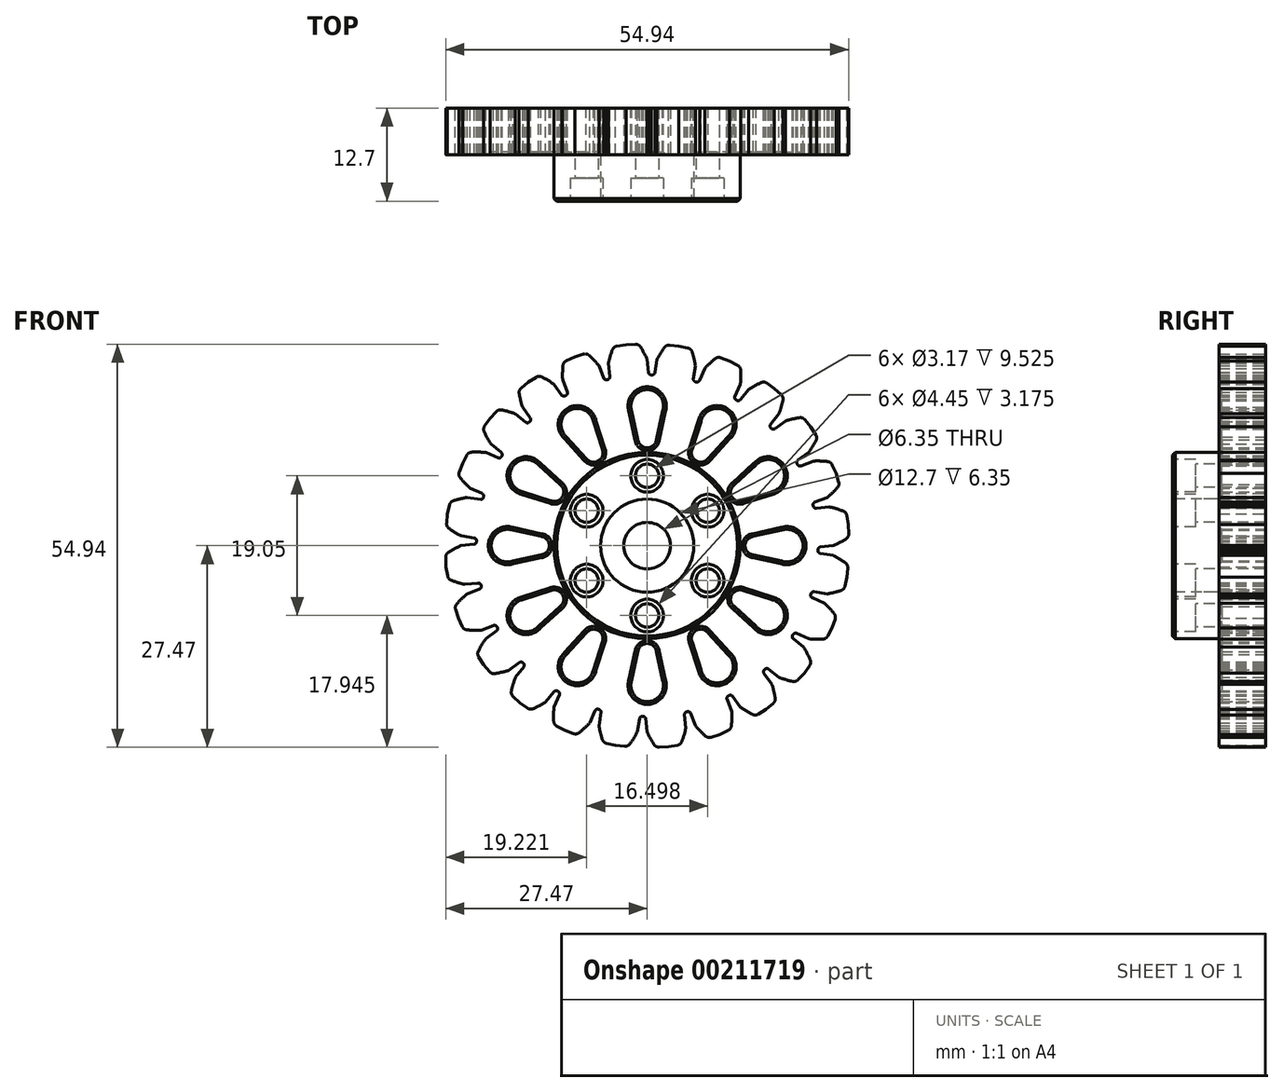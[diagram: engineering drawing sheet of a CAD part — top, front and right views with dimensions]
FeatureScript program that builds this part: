
annotation { "Feature Type Name" : "Feature", "Feature Type Description" : "" }
export const myFeature = defineFeature(function(context is Context, id is Id, definition is map)
    precondition{}
    {
        {
            var Q0;
            Q0=qCreatedBy(makeId("Front.planeOp"),FACE);
            var sketch = newSketch(context, id + "F0", { "sketchPlane" : qUnion([Q0])});
            skArc(sketch, "E0", {"start": v(-5.32, 22.67) * mm, "mid": v(-5.42, 22.64) * mm, "end": v(-5.5, 22.62) * mm});
            skArc(sketch, "E1", {"start": v(0, 25.4) * mm, "mid": v(-0.43, 26.27) * mm, "end": v(-0.93, 27.11) * mm});
            skLineSegment(sketch, "E2", {"start": v(0, 25.4) * mm, "end": v(0.2, 23.55) * mm});
            skLineSegment(sketch, "E3", {"start": v(-1.63, 27.47) * mm, "end": v(-2.88, 27.42) * mm});
            skLineSegment(sketch, "E4.MirrorCS", {"start": v(-4.11, 27.21) * mm, "end": v(-2.88, 27.42) * mm});
            skArc(sketch, "E5.MirrorCS", {"start": v(-5.28, 24.84) * mm, "mid": v(-5.04, 25.79) * mm, "end": v(-4.72, 26.71) * mm});
            skLineSegment(sketch, "E6.MirrorCS", {"start": v(-5.28, 24.84) * mm, "end": v(-5.1, 23.05) * mm});
            skPoint(sketch, "E7.orphan", {"position": v(-4.77, 20.03) * mm});
            skPoint(sketch, "E8.orphan", {"position": v(0.5, 20.58) * mm});
            skPoint(sketch, "E9.visualSharp", {"position": v(-1.19, 27.5) * mm});
            skArc(sketch, "E9.filletArc", {"start": v(-0.93, 27.11) * mm, "mid": v(-1.23, 27.38) * mm, "end": v(-1.63, 27.47) * mm});
            skPoint(sketch, "E10.visualSharp", {"position": v(-4.55, 27.14) * mm});
            skArc(sketch, "E10.filletArc", {"start": v(-4.11, 27.21) * mm, "mid": v(-4.49, 27.04) * mm, "end": v(-4.72, 26.71) * mm});
            skArc(sketch, "E11", {"start": v(-5.47, 22.63) * mm, "mid": v(-5.18, 22.78) * mm, "end": v(-5.1, 23.1) * mm});
            skArc(sketch, "E12", {"start": v(0.18, 23.7) * mm, "mid": v(0.29, 23.4) * mm, "end": v(0.6, 23.28) * mm});
            skArc(sketch, "E13.1.0", {"start": v(-11.14, 20.44) * mm, "mid": v(-10.9, 20.66) * mm, "end": v(-10.9, 20.99) * mm});
            skLineSegment(sketch, "E13.1.1", {"start": v(-11.53, 22.63) * mm, "end": v(-10.88, 20.94) * mm});
            skPoint(sketch, "E13.1.2", {"position": v(-11.42, 25.03) * mm});
            skArc(sketch, "E13.1.3", {"start": v(-11.02, 25.22) * mm, "mid": v(-11.33, 24.96) * mm, "end": v(-11.48, 24.58) * mm});
            skArc(sketch, "E13.1.4", {"start": v(-11.53, 22.63) * mm, "mid": v(-11.54, 23.6) * mm, "end": v(-11.48, 24.58) * mm});
            skLineSegment(sketch, "E13.1.5", {"start": v(-11.02, 25.22) * mm, "end": v(-9.88, 25.74) * mm});
            skLineSegment(sketch, "E13.1.6", {"start": v(-8.69, 26.11) * mm, "end": v(-9.88, 25.74) * mm});
            skArc(sketch, "E13.1.7", {"start": v(-7.92, 25.95) * mm, "mid": v(-8.28, 26.13) * mm, "end": v(-8.69, 26.11) * mm});
            skArc(sketch, "E13.1.8", {"start": v(-6.57, 24.53) * mm, "mid": v(-7.22, 25.27) * mm, "end": v(-7.92, 25.95) * mm});
            skLineSegment(sketch, "E13.1.9", {"start": v(-6.57, 24.53) * mm, "end": v(-5.9, 22.8) * mm});
            skArc(sketch, "E13.1.10", {"start": v(-5.96, 22.95) * mm, "mid": v(-5.78, 22.67) * mm, "end": v(-5.45, 22.64) * mm});
            skArc(sketch, "E13.2.0", {"start": v(-16.06, 16.86) * mm, "mid": v(-15.88, 17.13) * mm, "end": v(-15.96, 17.45) * mm});
            skLineSegment(sketch, "E13.2.1", {"start": v(-17, 18.88) * mm, "end": v(-15.93, 17.41) * mm});
            skPoint(sketch, "E13.2.2", {"position": v(-17.51, 21.23) * mm});
            skArc(sketch, "E13.2.3", {"start": v(-17.17, 21.5) * mm, "mid": v(-17.4, 21.18) * mm, "end": v(-17.45, 20.77) * mm});
            skArc(sketch, "E13.2.4", {"start": v(-17, 18.88) * mm, "mid": v(-17.26, 19.81) * mm, "end": v(-17.45, 20.77) * mm});
            skLineSegment(sketch, "E13.2.5", {"start": v(-17.17, 21.5) * mm, "end": v(-16.2, 22.3) * mm});
            skLineSegment(sketch, "E13.2.6", {"start": v(-15.15, 22.98) * mm, "end": v(-16.2, 22.3) * mm});
            skArc(sketch, "E13.2.7", {"start": v(-14.36, 23.01) * mm, "mid": v(-14.76, 23.1) * mm, "end": v(-15.15, 22.98) * mm});
            skArc(sketch, "E13.2.8", {"start": v(-12.7, 22) * mm, "mid": v(-13.51, 22.54) * mm, "end": v(-14.36, 23.01) * mm});
            skLineSegment(sketch, "E13.2.9", {"start": v(-12.7, 22) * mm, "end": v(-11.6, 20.5) * mm});
            skArc(sketch, "E13.2.10", {"start": v(-11.7, 20.62) * mm, "mid": v(-11.45, 20.4) * mm, "end": v(-11.13, 20.45) * mm});
            skArc(sketch, "E13.3.0", {"start": v(-19.87, 12.13) * mm, "mid": v(-19.77, 12.44) * mm, "end": v(-19.93, 12.72) * mm});
            skLineSegment(sketch, "E13.3.1", {"start": v(-21.3, 13.83) * mm, "end": v(-19.9, 12.7) * mm});
            skPoint(sketch, "E13.3.2", {"position": v(-22.4, 15.97) * mm});
            skArc(sketch, "E13.3.3", {"start": v(-22.15, 16.33) * mm, "mid": v(-22.3, 15.95) * mm, "end": v(-22.23, 15.55) * mm});
            skArc(sketch, "E13.3.4", {"start": v(-21.3, 13.83) * mm, "mid": v(-21.8, 14.67) * mm, "end": v(-22.23, 15.55) * mm});
            skLineSegment(sketch, "E13.3.5", {"start": v(-22.15, 16.33) * mm, "end": v(-21.42, 17.35) * mm});
            skLineSegment(sketch, "E13.3.6", {"start": v(-20.58, 18.27) * mm, "end": v(-21.42, 17.35) * mm});
            skArc(sketch, "E13.3.7", {"start": v(-19.83, 18.51) * mm, "mid": v(-20.24, 18.5) * mm, "end": v(-20.58, 18.27) * mm});
            skArc(sketch, "E13.3.8", {"start": v(-17.96, 17.96) * mm, "mid": v(-18.88, 18.27) * mm, "end": v(-19.83, 18.51) * mm});
            skLineSegment(sketch, "E13.3.9", {"start": v(-17.96, 17.96) * mm, "end": v(-16.52, 16.8) * mm});
            skArc(sketch, "E13.3.10", {"start": v(-16.64, 16.9) * mm, "mid": v(-16.34, 16.75) * mm, "end": v(-16.04, 16.88) * mm});
            skArc(sketch, "E13.4.0", {"start": v(-22.34, 6.58) * mm, "mid": v(-22.32, 6.9) * mm, "end": v(-22.55, 7.13) * mm});
            skLineSegment(sketch, "E13.4.1", {"start": v(-24.16, 7.85) * mm, "end": v(-22.5, 7.11) * mm});
            skPoint(sketch, "E13.4.2", {"position": v(-25.78, 9.63) * mm});
            skArc(sketch, "E13.4.3", {"start": v(-25.62, 10.04) * mm, "mid": v(-25.66, 9.64) * mm, "end": v(-25.5, 9.26) * mm});
            skArc(sketch, "E13.4.4", {"start": v(-24.16, 7.85) * mm, "mid": v(-24.85, 8.53) * mm, "end": v(-25.5, 9.26) * mm});
            skLineSegment(sketch, "E13.4.5", {"start": v(-25.62, 10.04) * mm, "end": v(-25.19, 11.21) * mm});
            skLineSegment(sketch, "E13.4.6", {"start": v(-24.6, 12.32) * mm, "end": v(-25.19, 11.21) * mm});
            skArc(sketch, "E13.4.7", {"start": v(-23.94, 12.75) * mm, "mid": v(-24.33, 12.62) * mm, "end": v(-24.6, 12.32) * mm});
            skArc(sketch, "E13.4.8", {"start": v(-22, 12.7) * mm, "mid": v(-22.97, 12.76) * mm, "end": v(-23.94, 12.75) * mm});
            skLineSegment(sketch, "E13.4.9", {"start": v(-22, 12.7) * mm, "end": v(-20.3, 11.94) * mm});
            skArc(sketch, "E13.4.10", {"start": v(-20.44, 12) * mm, "mid": v(-20.12, 11.95) * mm, "end": v(-19.86, 12.15) * mm});
            skArc(sketch, "E13.5.0", {"start": v(-23.28, 0.57) * mm, "mid": v(-23.34, 0.9) * mm, "end": v(-23.62, 1.05) * mm});
            skLineSegment(sketch, "E13.5.1", {"start": v(-25.37, 1.33) * mm, "end": v(-23.58, 1.05) * mm});
            skPoint(sketch, "E13.5.2", {"position": v(-27.4, 2.63) * mm});
            skArc(sketch, "E13.5.3", {"start": v(-27.35, 3.07) * mm, "mid": v(-27.28, 2.67) * mm, "end": v(-27.02, 2.35) * mm});
            skArc(sketch, "E13.5.4", {"start": v(-25.37, 1.33) * mm, "mid": v(-26.21, 1.8) * mm, "end": v(-27.02, 2.35) * mm});
            skLineSegment(sketch, "E13.5.5", {"start": v(-27.35, 3.07) * mm, "end": v(-27.23, 4.31) * mm});
            skLineSegment(sketch, "E13.5.6", {"start": v(-26.96, 5.53) * mm, "end": v(-27.23, 4.31) * mm});
            skArc(sketch, "E13.5.7", {"start": v(-26.43, 6.12) * mm, "mid": v(-26.77, 5.9) * mm, "end": v(-26.96, 5.53) * mm});
            skArc(sketch, "E13.5.8", {"start": v(-24.53, 6.57) * mm, "mid": v(-25.5, 6.38) * mm, "end": v(-26.43, 6.12) * mm});
            skLineSegment(sketch, "E13.5.9", {"start": v(-24.53, 6.57) * mm, "end": v(-22.7, 6.28) * mm});
            skArc(sketch, "E13.5.10", {"start": v(-22.86, 6.3) * mm, "mid": v(-22.53, 6.33) * mm, "end": v(-22.33, 6.6) * mm});
            skArc(sketch, "E13.6.0", {"start": v(-22.63, -5.47) * mm, "mid": v(-22.78, -5.18) * mm, "end": v(-23.1, -5.1) * mm});
            skLineSegment(sketch, "E13.6.1", {"start": v(-24.84, -5.28) * mm, "end": v(-23.05, -5.1) * mm});
            skPoint(sketch, "E13.6.2", {"position": v(-27.14, -4.55) * mm});
            skArc(sketch, "E13.6.3", {"start": v(-27.21, -4.11) * mm, "mid": v(-27.04, -4.49) * mm, "end": v(-26.71, -4.72) * mm});
            skArc(sketch, "E13.6.4", {"start": v(-24.84, -5.28) * mm, "mid": v(-25.79, -5.04) * mm, "end": v(-26.71, -4.72) * mm});
            skLineSegment(sketch, "E13.6.5", {"start": v(-27.21, -4.11) * mm, "end": v(-27.42, -2.88) * mm});
            skLineSegment(sketch, "E13.6.6", {"start": v(-27.47, -1.63) * mm, "end": v(-27.42, -2.88) * mm});
            skArc(sketch, "E13.6.7", {"start": v(-27.11, -0.93) * mm, "mid": v(-27.38, -1.23) * mm, "end": v(-27.47, -1.63) * mm});
            skArc(sketch, "E13.6.8", {"start": v(-25.4, 0) * mm, "mid": v(-26.27, -0.43) * mm, "end": v(-27.11, -0.93) * mm});
            skLineSegment(sketch, "E13.6.9", {"start": v(-25.4, 0) * mm, "end": v(-23.55, 0.2) * mm});
            skArc(sketch, "E13.6.10", {"start": v(-23.7, 0.18) * mm, "mid": v(-23.4, 0.29) * mm, "end": v(-23.28, 0.6) * mm});
            skArc(sketch, "E13.7.0", {"start": v(-20.44, -11.14) * mm, "mid": v(-20.66, -10.9) * mm, "end": v(-20.99, -10.9) * mm});
            skLineSegment(sketch, "E13.7.1", {"start": v(-22.63, -11.53) * mm, "end": v(-20.94, -10.88) * mm});
            skPoint(sketch, "E13.7.2", {"position": v(-25.03, -11.42) * mm});
            skArc(sketch, "E13.7.3", {"start": v(-25.22, -11.02) * mm, "mid": v(-24.96, -11.33) * mm, "end": v(-24.58, -11.48) * mm});
            skArc(sketch, "E13.7.4", {"start": v(-22.63, -11.53) * mm, "mid": v(-23.6, -11.54) * mm, "end": v(-24.58, -11.48) * mm});
            skLineSegment(sketch, "E13.7.5", {"start": v(-25.22, -11.02) * mm, "end": v(-25.74, -9.88) * mm});
            skLineSegment(sketch, "E13.7.6", {"start": v(-26.11, -8.69) * mm, "end": v(-25.74, -9.88) * mm});
            skArc(sketch, "E13.7.7", {"start": v(-25.95, -7.92) * mm, "mid": v(-26.13, -8.28) * mm, "end": v(-26.11, -8.69) * mm});
            skArc(sketch, "E13.7.8", {"start": v(-24.53, -6.57) * mm, "mid": v(-25.27, -7.22) * mm, "end": v(-25.95, -7.92) * mm});
            skLineSegment(sketch, "E13.7.9", {"start": v(-24.53, -6.57) * mm, "end": v(-22.8, -5.9) * mm});
            skArc(sketch, "E13.7.10", {"start": v(-22.95, -5.96) * mm, "mid": v(-22.67, -5.78) * mm, "end": v(-22.64, -5.45) * mm});
            skArc(sketch, "E13.8.0", {"start": v(-16.86, -16.06) * mm, "mid": v(-17.13, -15.88) * mm, "end": v(-17.45, -15.96) * mm});
            skLineSegment(sketch, "E13.8.1", {"start": v(-18.88, -17) * mm, "end": v(-17.41, -15.93) * mm});
            skPoint(sketch, "E13.8.2", {"position": v(-21.23, -17.51) * mm});
            skArc(sketch, "E13.8.3", {"start": v(-21.5, -17.17) * mm, "mid": v(-21.18, -17.4) * mm, "end": v(-20.77, -17.45) * mm});
            skArc(sketch, "E13.8.4", {"start": v(-18.88, -17) * mm, "mid": v(-19.81, -17.26) * mm, "end": v(-20.77, -17.45) * mm});
            skLineSegment(sketch, "E13.8.5", {"start": v(-21.5, -17.17) * mm, "end": v(-22.3, -16.2) * mm});
            skLineSegment(sketch, "E13.8.6", {"start": v(-22.98, -15.15) * mm, "end": v(-22.3, -16.2) * mm});
            skArc(sketch, "E13.8.7", {"start": v(-23.01, -14.36) * mm, "mid": v(-23.1, -14.76) * mm, "end": v(-22.98, -15.15) * mm});
            skArc(sketch, "E13.8.8", {"start": v(-22, -12.7) * mm, "mid": v(-22.54, -13.51) * mm, "end": v(-23.01, -14.36) * mm});
            skLineSegment(sketch, "E13.8.9", {"start": v(-22, -12.7) * mm, "end": v(-20.5, -11.6) * mm});
            skArc(sketch, "E13.8.10", {"start": v(-20.62, -11.7) * mm, "mid": v(-20.4, -11.45) * mm, "end": v(-20.45, -11.13) * mm});
            skArc(sketch, "E13.9.0", {"start": v(-12.13, -19.87) * mm, "mid": v(-12.44, -19.77) * mm, "end": v(-12.72, -19.93) * mm});
            skLineSegment(sketch, "E13.9.1", {"start": v(-13.83, -21.3) * mm, "end": v(-12.7, -19.9) * mm});
            skPoint(sketch, "E13.9.2", {"position": v(-15.97, -22.4) * mm});
            skArc(sketch, "E13.9.3", {"start": v(-16.33, -22.15) * mm, "mid": v(-15.95, -22.3) * mm, "end": v(-15.55, -22.23) * mm});
            skArc(sketch, "E13.9.4", {"start": v(-13.83, -21.3) * mm, "mid": v(-14.67, -21.8) * mm, "end": v(-15.55, -22.23) * mm});
            skLineSegment(sketch, "E13.9.5", {"start": v(-16.33, -22.15) * mm, "end": v(-17.35, -21.42) * mm});
            skLineSegment(sketch, "E13.9.6", {"start": v(-18.27, -20.58) * mm, "end": v(-17.35, -21.42) * mm});
            skArc(sketch, "E13.9.7", {"start": v(-18.51, -19.83) * mm, "mid": v(-18.5, -20.24) * mm, "end": v(-18.27, -20.58) * mm});
            skArc(sketch, "E13.9.8", {"start": v(-17.96, -17.96) * mm, "mid": v(-18.27, -18.88) * mm, "end": v(-18.51, -19.83) * mm});
            skLineSegment(sketch, "E13.9.9", {"start": v(-17.96, -17.96) * mm, "end": v(-16.8, -16.52) * mm});
            skArc(sketch, "E13.9.10", {"start": v(-16.9, -16.64) * mm, "mid": v(-16.75, -16.34) * mm, "end": v(-16.88, -16.04) * mm});
            skArc(sketch, "E13.10.0", {"start": v(-6.58, -22.34) * mm, "mid": v(-6.9, -22.32) * mm, "end": v(-7.13, -22.55) * mm});
            skLineSegment(sketch, "E13.10.1", {"start": v(-7.85, -24.16) * mm, "end": v(-7.11, -22.5) * mm});
            skPoint(sketch, "E13.10.2", {"position": v(-9.63, -25.78) * mm});
            skArc(sketch, "E13.10.3", {"start": v(-10.04, -25.62) * mm, "mid": v(-9.64, -25.66) * mm, "end": v(-9.26, -25.5) * mm});
            skArc(sketch, "E13.10.4", {"start": v(-7.85, -24.16) * mm, "mid": v(-8.53, -24.85) * mm, "end": v(-9.26, -25.5) * mm});
            skLineSegment(sketch, "E13.10.5", {"start": v(-10.04, -25.62) * mm, "end": v(-11.21, -25.19) * mm});
            skLineSegment(sketch, "E13.10.6", {"start": v(-12.32, -24.6) * mm, "end": v(-11.21, -25.19) * mm});
            skArc(sketch, "E13.10.7", {"start": v(-12.75, -23.94) * mm, "mid": v(-12.62, -24.33) * mm, "end": v(-12.32, -24.6) * mm});
            skArc(sketch, "E13.10.8", {"start": v(-12.7, -22) * mm, "mid": v(-12.76, -22.97) * mm, "end": v(-12.75, -23.94) * mm});
            skLineSegment(sketch, "E13.10.9", {"start": v(-12.7, -22) * mm, "end": v(-11.94, -20.3) * mm});
            skArc(sketch, "E13.10.10", {"start": v(-12, -20.44) * mm, "mid": v(-11.95, -20.12) * mm, "end": v(-12.15, -19.86) * mm});
            skArc(sketch, "E13.11.0", {"start": v(-0.57, -23.28) * mm, "mid": v(-0.9, -23.34) * mm, "end": v(-1.05, -23.62) * mm});
            skLineSegment(sketch, "E13.11.1", {"start": v(-1.33, -25.37) * mm, "end": v(-1.05, -23.58) * mm});
            skPoint(sketch, "E13.11.2", {"position": v(-2.63, -27.4) * mm});
            skArc(sketch, "E13.11.3", {"start": v(-3.07, -27.35) * mm, "mid": v(-2.67, -27.28) * mm, "end": v(-2.35, -27.02) * mm});
            skArc(sketch, "E13.11.4", {"start": v(-1.33, -25.37) * mm, "mid": v(-1.8, -26.21) * mm, "end": v(-2.35, -27.02) * mm});
            skLineSegment(sketch, "E13.11.5", {"start": v(-3.07, -27.35) * mm, "end": v(-4.31, -27.23) * mm});
            skLineSegment(sketch, "E13.11.6", {"start": v(-5.53, -26.96) * mm, "end": v(-4.31, -27.23) * mm});
            skArc(sketch, "E13.11.7", {"start": v(-6.12, -26.43) * mm, "mid": v(-5.9, -26.77) * mm, "end": v(-5.53, -26.96) * mm});
            skArc(sketch, "E13.11.8", {"start": v(-6.57, -24.53) * mm, "mid": v(-6.38, -25.5) * mm, "end": v(-6.12, -26.43) * mm});
            skLineSegment(sketch, "E13.11.9", {"start": v(-6.57, -24.53) * mm, "end": v(-6.28, -22.7) * mm});
            skArc(sketch, "E13.11.10", {"start": v(-6.3, -22.86) * mm, "mid": v(-6.33, -22.53) * mm, "end": v(-6.6, -22.33) * mm});
            skArc(sketch, "E13.12.0", {"start": v(5.47, -22.63) * mm, "mid": v(5.18, -22.78) * mm, "end": v(5.1, -23.1) * mm});
            skLineSegment(sketch, "E13.12.1", {"start": v(5.28, -24.84) * mm, "end": v(5.1, -23.05) * mm});
            skPoint(sketch, "E13.12.2", {"position": v(4.55, -27.14) * mm});
            skArc(sketch, "E13.12.3", {"start": v(4.11, -27.21) * mm, "mid": v(4.49, -27.04) * mm, "end": v(4.72, -26.71) * mm});
            skArc(sketch, "E13.12.4", {"start": v(5.28, -24.84) * mm, "mid": v(5.04, -25.79) * mm, "end": v(4.72, -26.71) * mm});
            skLineSegment(sketch, "E13.12.5", {"start": v(4.11, -27.21) * mm, "end": v(2.88, -27.42) * mm});
            skLineSegment(sketch, "E13.12.6", {"start": v(1.63, -27.47) * mm, "end": v(2.88, -27.42) * mm});
            skArc(sketch, "E13.12.7", {"start": v(0.93, -27.11) * mm, "mid": v(1.23, -27.38) * mm, "end": v(1.63, -27.47) * mm});
            skArc(sketch, "E13.12.8", {"start": v(0, -25.4) * mm, "mid": v(0.43, -26.27) * mm, "end": v(0.93, -27.11) * mm});
            skLineSegment(sketch, "E13.12.9", {"start": v(0, -25.4) * mm, "end": v(-0.2, -23.55) * mm});
            skArc(sketch, "E13.12.10", {"start": v(-0.18, -23.7) * mm, "mid": v(-0.29, -23.4) * mm, "end": v(-0.6, -23.28) * mm});
            skArc(sketch, "E13.13.0", {"start": v(11.14, -20.44) * mm, "mid": v(10.9, -20.66) * mm, "end": v(10.9, -20.99) * mm});
            skLineSegment(sketch, "E13.13.1", {"start": v(11.53, -22.63) * mm, "end": v(10.88, -20.94) * mm});
            skPoint(sketch, "E13.13.2", {"position": v(11.42, -25.03) * mm});
            skArc(sketch, "E13.13.3", {"start": v(11.02, -25.22) * mm, "mid": v(11.33, -24.96) * mm, "end": v(11.48, -24.58) * mm});
            skArc(sketch, "E13.13.4", {"start": v(11.53, -22.63) * mm, "mid": v(11.54, -23.6) * mm, "end": v(11.48, -24.58) * mm});
            skLineSegment(sketch, "E13.13.5", {"start": v(11.02, -25.22) * mm, "end": v(9.88, -25.74) * mm});
            skLineSegment(sketch, "E13.13.6", {"start": v(8.69, -26.11) * mm, "end": v(9.88, -25.74) * mm});
            skArc(sketch, "E13.13.7", {"start": v(7.92, -25.95) * mm, "mid": v(8.28, -26.13) * mm, "end": v(8.69, -26.11) * mm});
            skArc(sketch, "E13.13.8", {"start": v(6.57, -24.53) * mm, "mid": v(7.22, -25.27) * mm, "end": v(7.92, -25.95) * mm});
            skLineSegment(sketch, "E13.13.9", {"start": v(6.57, -24.53) * mm, "end": v(5.9, -22.8) * mm});
            skArc(sketch, "E13.13.10", {"start": v(5.96, -22.95) * mm, "mid": v(5.78, -22.67) * mm, "end": v(5.45, -22.64) * mm});
            skArc(sketch, "E13.14.0", {"start": v(16.06, -16.86) * mm, "mid": v(15.88, -17.13) * mm, "end": v(15.96, -17.45) * mm});
            skLineSegment(sketch, "E13.14.1", {"start": v(17, -18.88) * mm, "end": v(15.93, -17.41) * mm});
            skPoint(sketch, "E13.14.2", {"position": v(17.51, -21.23) * mm});
            skArc(sketch, "E13.14.3", {"start": v(17.17, -21.5) * mm, "mid": v(17.4, -21.18) * mm, "end": v(17.45, -20.77) * mm});
            skArc(sketch, "E13.14.4", {"start": v(17, -18.88) * mm, "mid": v(17.26, -19.81) * mm, "end": v(17.45, -20.77) * mm});
            skLineSegment(sketch, "E13.14.5", {"start": v(17.17, -21.5) * mm, "end": v(16.2, -22.3) * mm});
            skLineSegment(sketch, "E13.14.6", {"start": v(15.15, -22.98) * mm, "end": v(16.2, -22.3) * mm});
            skArc(sketch, "E13.14.7", {"start": v(14.36, -23.01) * mm, "mid": v(14.76, -23.1) * mm, "end": v(15.15, -22.98) * mm});
            skArc(sketch, "E13.14.8", {"start": v(12.7, -22) * mm, "mid": v(13.51, -22.54) * mm, "end": v(14.36, -23.01) * mm});
            skLineSegment(sketch, "E13.14.9", {"start": v(12.7, -22) * mm, "end": v(11.6, -20.5) * mm});
            skArc(sketch, "E13.14.10", {"start": v(11.7, -20.62) * mm, "mid": v(11.45, -20.4) * mm, "end": v(11.13, -20.45) * mm});
            skArc(sketch, "E13.15.0", {"start": v(19.87, -12.13) * mm, "mid": v(19.77, -12.44) * mm, "end": v(19.93, -12.72) * mm});
            skLineSegment(sketch, "E13.15.1", {"start": v(21.3, -13.83) * mm, "end": v(19.9, -12.7) * mm});
            skPoint(sketch, "E13.15.2", {"position": v(22.4, -15.97) * mm});
            skArc(sketch, "E13.15.3", {"start": v(22.15, -16.33) * mm, "mid": v(22.3, -15.95) * mm, "end": v(22.23, -15.55) * mm});
            skArc(sketch, "E13.15.4", {"start": v(21.3, -13.83) * mm, "mid": v(21.8, -14.67) * mm, "end": v(22.23, -15.55) * mm});
            skLineSegment(sketch, "E13.15.5", {"start": v(22.15, -16.33) * mm, "end": v(21.42, -17.35) * mm});
            skLineSegment(sketch, "E13.15.6", {"start": v(20.58, -18.27) * mm, "end": v(21.42, -17.35) * mm});
            skArc(sketch, "E13.15.7", {"start": v(19.83, -18.51) * mm, "mid": v(20.24, -18.5) * mm, "end": v(20.58, -18.27) * mm});
            skArc(sketch, "E13.15.8", {"start": v(17.96, -17.96) * mm, "mid": v(18.88, -18.27) * mm, "end": v(19.83, -18.51) * mm});
            skLineSegment(sketch, "E13.15.9", {"start": v(17.96, -17.96) * mm, "end": v(16.52, -16.8) * mm});
            skArc(sketch, "E13.15.10", {"start": v(16.64, -16.9) * mm, "mid": v(16.34, -16.75) * mm, "end": v(16.04, -16.88) * mm});
            skArc(sketch, "E13.16.0", {"start": v(22.34, -6.58) * mm, "mid": v(22.32, -6.9) * mm, "end": v(22.55, -7.13) * mm});
            skLineSegment(sketch, "E13.16.1", {"start": v(24.16, -7.85) * mm, "end": v(22.5, -7.11) * mm});
            skPoint(sketch, "E13.16.2", {"position": v(25.78, -9.63) * mm});
            skArc(sketch, "E13.16.3", {"start": v(25.62, -10.04) * mm, "mid": v(25.66, -9.64) * mm, "end": v(25.5, -9.26) * mm});
            skArc(sketch, "E13.16.4", {"start": v(24.16, -7.85) * mm, "mid": v(24.85, -8.53) * mm, "end": v(25.5, -9.26) * mm});
            skLineSegment(sketch, "E13.16.5", {"start": v(25.62, -10.04) * mm, "end": v(25.19, -11.21) * mm});
            skLineSegment(sketch, "E13.16.6", {"start": v(24.6, -12.32) * mm, "end": v(25.19, -11.21) * mm});
            skArc(sketch, "E13.16.7", {"start": v(23.94, -12.75) * mm, "mid": v(24.33, -12.62) * mm, "end": v(24.6, -12.32) * mm});
            skArc(sketch, "E13.16.8", {"start": v(22, -12.7) * mm, "mid": v(22.97, -12.76) * mm, "end": v(23.94, -12.75) * mm});
            skLineSegment(sketch, "E13.16.9", {"start": v(22, -12.7) * mm, "end": v(20.3, -11.94) * mm});
            skArc(sketch, "E13.16.10", {"start": v(20.44, -12) * mm, "mid": v(20.12, -11.95) * mm, "end": v(19.86, -12.15) * mm});
            skArc(sketch, "E13.17.0", {"start": v(23.28, -0.57) * mm, "mid": v(23.34, -0.9) * mm, "end": v(23.62, -1.05) * mm});
            skLineSegment(sketch, "E13.17.1", {"start": v(25.37, -1.33) * mm, "end": v(23.58, -1.05) * mm});
            skPoint(sketch, "E13.17.2", {"position": v(27.4, -2.63) * mm});
            skArc(sketch, "E13.17.3", {"start": v(27.35, -3.07) * mm, "mid": v(27.28, -2.67) * mm, "end": v(27.02, -2.35) * mm});
            skArc(sketch, "E13.17.4", {"start": v(25.37, -1.33) * mm, "mid": v(26.21, -1.8) * mm, "end": v(27.02, -2.35) * mm});
            skLineSegment(sketch, "E13.17.5", {"start": v(27.35, -3.07) * mm, "end": v(27.23, -4.31) * mm});
            skLineSegment(sketch, "E13.17.6", {"start": v(26.96, -5.53) * mm, "end": v(27.23, -4.31) * mm});
            skArc(sketch, "E13.17.7", {"start": v(26.43, -6.12) * mm, "mid": v(26.77, -5.9) * mm, "end": v(26.96, -5.53) * mm});
            skArc(sketch, "E13.17.8", {"start": v(24.53, -6.57) * mm, "mid": v(25.5, -6.38) * mm, "end": v(26.43, -6.12) * mm});
            skLineSegment(sketch, "E13.17.9", {"start": v(24.53, -6.57) * mm, "end": v(22.7, -6.28) * mm});
            skArc(sketch, "E13.17.10", {"start": v(22.86, -6.3) * mm, "mid": v(22.53, -6.33) * mm, "end": v(22.33, -6.6) * mm});
            skArc(sketch, "E13.18.0", {"start": v(22.63, 5.47) * mm, "mid": v(22.78, 5.18) * mm, "end": v(23.1, 5.1) * mm});
            skLineSegment(sketch, "E13.18.1", {"start": v(24.84, 5.28) * mm, "end": v(23.05, 5.1) * mm});
            skPoint(sketch, "E13.18.2", {"position": v(27.14, 4.55) * mm});
            skArc(sketch, "E13.18.3", {"start": v(27.21, 4.11) * mm, "mid": v(27.04, 4.49) * mm, "end": v(26.71, 4.72) * mm});
            skArc(sketch, "E13.18.4", {"start": v(24.84, 5.28) * mm, "mid": v(25.79, 5.04) * mm, "end": v(26.71, 4.72) * mm});
            skLineSegment(sketch, "E13.18.5", {"start": v(27.21, 4.11) * mm, "end": v(27.42, 2.88) * mm});
            skLineSegment(sketch, "E13.18.6", {"start": v(27.47, 1.63) * mm, "end": v(27.42, 2.88) * mm});
            skArc(sketch, "E13.18.7", {"start": v(27.11, 0.93) * mm, "mid": v(27.38, 1.23) * mm, "end": v(27.47, 1.63) * mm});
            skArc(sketch, "E13.18.8", {"start": v(25.4, 0) * mm, "mid": v(26.27, 0.43) * mm, "end": v(27.11, 0.93) * mm});
            skLineSegment(sketch, "E13.18.9", {"start": v(25.4, 0) * mm, "end": v(23.55, -0.2) * mm});
            skArc(sketch, "E13.18.10", {"start": v(23.7, -0.18) * mm, "mid": v(23.4, -0.29) * mm, "end": v(23.28, -0.6) * mm});
            skArc(sketch, "E13.19.0", {"start": v(20.44, 11.14) * mm, "mid": v(20.66, 10.9) * mm, "end": v(20.99, 10.9) * mm});
            skLineSegment(sketch, "E13.19.1", {"start": v(22.63, 11.53) * mm, "end": v(20.94, 10.88) * mm});
            skPoint(sketch, "E13.19.2", {"position": v(25.03, 11.42) * mm});
            skArc(sketch, "E13.19.3", {"start": v(25.22, 11.02) * mm, "mid": v(24.96, 11.33) * mm, "end": v(24.58, 11.48) * mm});
            skArc(sketch, "E13.19.4", {"start": v(22.63, 11.53) * mm, "mid": v(23.6, 11.54) * mm, "end": v(24.58, 11.48) * mm});
            skLineSegment(sketch, "E13.19.5", {"start": v(25.22, 11.02) * mm, "end": v(25.74, 9.88) * mm});
            skLineSegment(sketch, "E13.19.6", {"start": v(26.11, 8.69) * mm, "end": v(25.74, 9.88) * mm});
            skArc(sketch, "E13.19.7", {"start": v(25.95, 7.92) * mm, "mid": v(26.13, 8.28) * mm, "end": v(26.11, 8.69) * mm});
            skArc(sketch, "E13.19.8", {"start": v(24.53, 6.57) * mm, "mid": v(25.27, 7.22) * mm, "end": v(25.95, 7.92) * mm});
            skLineSegment(sketch, "E13.19.9", {"start": v(24.53, 6.57) * mm, "end": v(22.8, 5.9) * mm});
            skArc(sketch, "E13.19.10", {"start": v(22.95, 5.96) * mm, "mid": v(22.67, 5.78) * mm, "end": v(22.64, 5.45) * mm});
            skArc(sketch, "E13.20.0", {"start": v(16.86, 16.06) * mm, "mid": v(17.13, 15.88) * mm, "end": v(17.45, 15.96) * mm});
            skLineSegment(sketch, "E13.20.1", {"start": v(18.88, 17) * mm, "end": v(17.41, 15.93) * mm});
            skPoint(sketch, "E13.20.2", {"position": v(21.23, 17.51) * mm});
            skArc(sketch, "E13.20.3", {"start": v(21.5, 17.17) * mm, "mid": v(21.18, 17.4) * mm, "end": v(20.77, 17.45) * mm});
            skArc(sketch, "E13.20.4", {"start": v(18.88, 17) * mm, "mid": v(19.81, 17.26) * mm, "end": v(20.77, 17.45) * mm});
            skLineSegment(sketch, "E13.20.5", {"start": v(21.5, 17.17) * mm, "end": v(22.3, 16.2) * mm});
            skLineSegment(sketch, "E13.20.6", {"start": v(22.98, 15.15) * mm, "end": v(22.3, 16.2) * mm});
            skArc(sketch, "E13.20.7", {"start": v(23.01, 14.36) * mm, "mid": v(23.1, 14.76) * mm, "end": v(22.98, 15.15) * mm});
            skArc(sketch, "E13.20.8", {"start": v(22, 12.7) * mm, "mid": v(22.54, 13.51) * mm, "end": v(23.01, 14.36) * mm});
            skLineSegment(sketch, "E13.20.9", {"start": v(22, 12.7) * mm, "end": v(20.5, 11.6) * mm});
            skArc(sketch, "E13.20.10", {"start": v(20.62, 11.7) * mm, "mid": v(20.4, 11.45) * mm, "end": v(20.45, 11.13) * mm});
            skArc(sketch, "E13.21.0", {"start": v(12.13, 19.87) * mm, "mid": v(12.44, 19.77) * mm, "end": v(12.72, 19.93) * mm});
            skLineSegment(sketch, "E13.21.1", {"start": v(13.83, 21.3) * mm, "end": v(12.7, 19.9) * mm});
            skPoint(sketch, "E13.21.2", {"position": v(15.97, 22.4) * mm});
            skArc(sketch, "E13.21.3", {"start": v(16.33, 22.15) * mm, "mid": v(15.95, 22.3) * mm, "end": v(15.55, 22.23) * mm});
            skArc(sketch, "E13.21.4", {"start": v(13.83, 21.3) * mm, "mid": v(14.67, 21.8) * mm, "end": v(15.55, 22.23) * mm});
            skLineSegment(sketch, "E13.21.5", {"start": v(16.33, 22.15) * mm, "end": v(17.35, 21.42) * mm});
            skLineSegment(sketch, "E13.21.6", {"start": v(18.27, 20.58) * mm, "end": v(17.35, 21.42) * mm});
            skArc(sketch, "E13.21.7", {"start": v(18.51, 19.83) * mm, "mid": v(18.5, 20.24) * mm, "end": v(18.27, 20.58) * mm});
            skArc(sketch, "E13.21.8", {"start": v(17.96, 17.96) * mm, "mid": v(18.27, 18.88) * mm, "end": v(18.51, 19.83) * mm});
            skLineSegment(sketch, "E13.21.9", {"start": v(17.96, 17.96) * mm, "end": v(16.8, 16.52) * mm});
            skArc(sketch, "E13.21.10", {"start": v(16.9, 16.64) * mm, "mid": v(16.75, 16.34) * mm, "end": v(16.88, 16.04) * mm});
            skArc(sketch, "E13.22.0", {"start": v(6.58, 22.34) * mm, "mid": v(6.9, 22.32) * mm, "end": v(7.13, 22.55) * mm});
            skLineSegment(sketch, "E13.22.1", {"start": v(7.85, 24.16) * mm, "end": v(7.11, 22.5) * mm});
            skPoint(sketch, "E13.22.2", {"position": v(9.63, 25.78) * mm});
            skArc(sketch, "E13.22.3", {"start": v(10.04, 25.62) * mm, "mid": v(9.64, 25.66) * mm, "end": v(9.26, 25.5) * mm});
            skArc(sketch, "E13.22.4", {"start": v(7.85, 24.16) * mm, "mid": v(8.53, 24.85) * mm, "end": v(9.26, 25.5) * mm});
            skLineSegment(sketch, "E13.22.5", {"start": v(10.04, 25.62) * mm, "end": v(11.21, 25.19) * mm});
            skLineSegment(sketch, "E13.22.6", {"start": v(12.32, 24.6) * mm, "end": v(11.21, 25.19) * mm});
            skArc(sketch, "E13.22.7", {"start": v(12.75, 23.94) * mm, "mid": v(12.62, 24.33) * mm, "end": v(12.32, 24.6) * mm});
            skArc(sketch, "E13.22.8", {"start": v(12.7, 22) * mm, "mid": v(12.76, 22.97) * mm, "end": v(12.75, 23.94) * mm});
            skLineSegment(sketch, "E13.22.9", {"start": v(12.7, 22) * mm, "end": v(11.94, 20.3) * mm});
            skArc(sketch, "E13.22.10", {"start": v(12, 20.44) * mm, "mid": v(11.95, 20.12) * mm, "end": v(12.15, 19.86) * mm});
            skArc(sketch, "E13.23.0", {"start": v(0.57, 23.28) * mm, "mid": v(0.9, 23.34) * mm, "end": v(1.05, 23.62) * mm});
            skLineSegment(sketch, "E13.23.1", {"start": v(1.33, 25.37) * mm, "end": v(1.05, 23.58) * mm});
            skPoint(sketch, "E13.23.2", {"position": v(2.63, 27.4) * mm});
            skArc(sketch, "E13.23.3", {"start": v(3.07, 27.35) * mm, "mid": v(2.67, 27.28) * mm, "end": v(2.35, 27.02) * mm});
            skArc(sketch, "E13.23.4", {"start": v(1.33, 25.37) * mm, "mid": v(1.8, 26.21) * mm, "end": v(2.35, 27.02) * mm});
            skLineSegment(sketch, "E13.23.5", {"start": v(3.07, 27.35) * mm, "end": v(4.31, 27.23) * mm});
            skLineSegment(sketch, "E13.23.6", {"start": v(5.53, 26.96) * mm, "end": v(4.31, 27.23) * mm});
            skArc(sketch, "E13.23.7", {"start": v(6.12, 26.43) * mm, "mid": v(5.9, 26.77) * mm, "end": v(5.53, 26.96) * mm});
            skArc(sketch, "E13.23.8", {"start": v(6.57, 24.53) * mm, "mid": v(6.38, 25.5) * mm, "end": v(6.12, 26.43) * mm});
            skLineSegment(sketch, "E13.23.9", {"start": v(6.57, 24.53) * mm, "end": v(6.28, 22.7) * mm});
            skArc(sketch, "E13.23.10", {"start": v(6.3, 22.86) * mm, "mid": v(6.33, 22.53) * mm, "end": v(6.6, 22.33) * mm});
            skArc(sketch, "E14.trimOffspring", {"start": v(-11, 20.52) * mm, "mid": v(-11.1, 20.47) * mm, "end": v(-11.18, 20.43) * mm});
            skArc(sketch, "E15.trimOffspring", {"start": v(-19.8, 12.26) * mm, "mid": v(-19.84, 12.18) * mm, "end": v(-19.9, 12.1) * mm});
            skArc(sketch, "E16.trimOffspring", {"start": v(-15.94, 16.97) * mm, "mid": v(-16.01, 16.9) * mm, "end": v(-16.08, 16.84) * mm});
            skArc(sketch, "E17.trimOffspring", {"start": v(0.73, 23.27) * mm, "mid": v(0.63, 23.27) * mm, "end": v(0.53, 23.28) * mm});
            skArc(sketch, "E18.trimOffspring", {"start": v(6.72, 22.3) * mm, "mid": v(6.63, 22.32) * mm, "end": v(6.54, 22.35) * mm});
            skArc(sketch, "E19.trimOffspring", {"start": v(12.26, 19.8) * mm, "mid": v(12.18, 19.84) * mm, "end": v(12.1, 19.9) * mm});
            skArc(sketch, "E20.trimOffspring", {"start": v(16.97, 15.94) * mm, "mid": v(16.9, 16.01) * mm, "end": v(16.84, 16.08) * mm});
            skArc(sketch, "E21.trimOffspring", {"start": v(22.67, 5.32) * mm, "mid": v(22.64, 5.42) * mm, "end": v(22.62, 5.5) * mm});
            skArc(sketch, "E22.trimOffspring", {"start": v(20.52, 11) * mm, "mid": v(20.47, 11.1) * mm, "end": v(20.43, 11.18) * mm});
            skArc(sketch, "E23.trimOffspring", {"start": v(23.27, -0.73) * mm, "mid": v(23.27, -0.63) * mm, "end": v(23.28, -0.53) * mm});
            skArc(sketch, "E24.trimOffspring", {"start": v(22.3, -6.72) * mm, "mid": v(22.32, -6.63) * mm, "end": v(22.35, -6.54) * mm});
            skArc(sketch, "E25.trimOffspring", {"start": v(19.8, -12.26) * mm, "mid": v(19.84, -12.18) * mm, "end": v(19.9, -12.1) * mm});
            skArc(sketch, "E26.trimOffspring", {"start": v(15.94, -16.97) * mm, "mid": v(16.01, -16.9) * mm, "end": v(16.08, -16.84) * mm});
            skArc(sketch, "E27.trimOffspring", {"start": v(11, -20.52) * mm, "mid": v(11.1, -20.47) * mm, "end": v(11.18, -20.43) * mm});
            skArc(sketch, "E28.trimOffspring", {"start": v(5.32, -22.67) * mm, "mid": v(5.42, -22.64) * mm, "end": v(5.5, -22.62) * mm});
            skArc(sketch, "E29.trimOffspring", {"start": v(-0.73, -23.27) * mm, "mid": v(-0.63, -23.27) * mm, "end": v(-0.53, -23.28) * mm});
            skArc(sketch, "E30.trimOffspring", {"start": v(-6.72, -22.3) * mm, "mid": v(-6.63, -22.32) * mm, "end": v(-6.54, -22.35) * mm});
            skArc(sketch, "E31.trimOffspring", {"start": v(-12.26, -19.8) * mm, "mid": v(-12.18, -19.84) * mm, "end": v(-12.1, -19.9) * mm});
            skArc(sketch, "E32.trimOffspring", {"start": v(-16.97, -15.94) * mm, "mid": v(-16.9, -16.01) * mm, "end": v(-16.84, -16.08) * mm});
            skArc(sketch, "E33.trimOffspring", {"start": v(-20.52, -11) * mm, "mid": v(-20.47, -11.1) * mm, "end": v(-20.43, -11.18) * mm});
            skArc(sketch, "E34.trimOffspring", {"start": v(-22.67, -5.32) * mm, "mid": v(-22.64, -5.42) * mm, "end": v(-22.62, -5.5) * mm});
            skArc(sketch, "E35.trimOffspring", {"start": v(-23.27, 0.73) * mm, "mid": v(-23.27, 0.63) * mm, "end": v(-23.28, 0.53) * mm});
            skArc(sketch, "E36.trimOffspring", {"start": v(-22.3, 6.72) * mm, "mid": v(-22.32, 6.63) * mm, "end": v(-22.35, 6.54) * mm});
            skArc(sketch, "E37", {"start": v(2.1, 18.32) * mm, "mid": v(0, 21.27) * mm, "end": v(-2.1, 18.32) * mm});
            skArc(sketch, "E38", {"start": v(-1.26, 14.46) * mm, "mid": v(0, 13.33) * mm, "end": v(1.26, 14.46) * mm});
            skLineSegment(sketch, "E39", {"start": v(2.21, 18.85) * mm, "end": v(1.2, 14.21) * mm});
            skLineSegment(sketch, "E40.MirrorCS", {"start": v(-2.21, 18.85) * mm, "end": v(-1.2, 14.21) * mm});
            skArc(sketch, "E41.1.0", {"start": v(-7.34, 16.91) * mm, "mid": v(-10.64, 18.42) * mm, "end": v(-10.98, 14.82) * mm});
            skLineSegment(sketch, "E41.1.1", {"start": v(-11.34, 15.21) * mm, "end": v(-8.15, 11.7) * mm});
            skArc(sketch, "E41.1.2", {"start": v(-8.32, 11.9) * mm, "mid": v(-6.67, 11.55) * mm, "end": v(-6.14, 13.16) * mm});
            skLineSegment(sketch, "E41.1.3", {"start": v(-7.5, 17.43) * mm, "end": v(-6.06, 12.91) * mm});
            skArc(sketch, "E41.2.0", {"start": v(-14.82, 10.98) * mm, "mid": v(-18.42, 10.64) * mm, "end": v(-16.91, 7.34) * mm});
            skLineSegment(sketch, "E41.2.1", {"start": v(-17.43, 7.5) * mm, "end": v(-12.91, 6.06) * mm});
            skArc(sketch, "E41.2.2", {"start": v(-13.16, 6.14) * mm, "mid": v(-11.55, 6.67) * mm, "end": v(-11.9, 8.32) * mm});
            skLineSegment(sketch, "E41.2.3", {"start": v(-15.21, 11.34) * mm, "end": v(-11.7, 8.15) * mm});
            skArc(sketch, "E41.3.0", {"start": v(-18.32, 2.1) * mm, "mid": v(-21.27, 0) * mm, "end": v(-18.32, -2.1) * mm});
            skLineSegment(sketch, "E41.3.1", {"start": v(-18.85, -2.21) * mm, "end": v(-14.21, -1.2) * mm});
            skArc(sketch, "E41.3.2", {"start": v(-14.46, -1.26) * mm, "mid": v(-13.33, 0) * mm, "end": v(-14.46, 1.26) * mm});
            skLineSegment(sketch, "E41.3.3", {"start": v(-18.85, 2.21) * mm, "end": v(-14.21, 1.2) * mm});
            skArc(sketch, "E41.4.0", {"start": v(-16.91, -7.34) * mm, "mid": v(-18.42, -10.64) * mm, "end": v(-14.82, -10.98) * mm});
            skLineSegment(sketch, "E41.4.1", {"start": v(-15.21, -11.34) * mm, "end": v(-11.7, -8.15) * mm});
            skArc(sketch, "E41.4.2", {"start": v(-11.9, -8.32) * mm, "mid": v(-11.55, -6.67) * mm, "end": v(-13.16, -6.14) * mm});
            skLineSegment(sketch, "E41.4.3", {"start": v(-17.43, -7.5) * mm, "end": v(-12.91, -6.06) * mm});
            skArc(sketch, "E41.5.0", {"start": v(-10.98, -14.82) * mm, "mid": v(-10.64, -18.42) * mm, "end": v(-7.34, -16.91) * mm});
            skLineSegment(sketch, "E41.5.1", {"start": v(-7.5, -17.43) * mm, "end": v(-6.06, -12.91) * mm});
            skArc(sketch, "E41.5.2", {"start": v(-6.14, -13.16) * mm, "mid": v(-6.67, -11.55) * mm, "end": v(-8.32, -11.9) * mm});
            skLineSegment(sketch, "E41.5.3", {"start": v(-11.34, -15.21) * mm, "end": v(-8.15, -11.7) * mm});
            skArc(sketch, "E41.6.0", {"start": v(-2.1, -18.32) * mm, "mid": v(0, -21.27) * mm, "end": v(2.1, -18.32) * mm});
            skLineSegment(sketch, "E41.6.1", {"start": v(2.21, -18.85) * mm, "end": v(1.2, -14.21) * mm});
            skArc(sketch, "E41.6.2", {"start": v(1.26, -14.46) * mm, "mid": v(0, -13.33) * mm, "end": v(-1.26, -14.46) * mm});
            skLineSegment(sketch, "E41.6.3", {"start": v(-2.21, -18.85) * mm, "end": v(-1.2, -14.21) * mm});
            skArc(sketch, "E41.7.0", {"start": v(7.34, -16.91) * mm, "mid": v(10.64, -18.42) * mm, "end": v(10.98, -14.82) * mm});
            skLineSegment(sketch, "E41.7.1", {"start": v(11.34, -15.21) * mm, "end": v(8.15, -11.7) * mm});
            skArc(sketch, "E41.7.2", {"start": v(8.32, -11.9) * mm, "mid": v(6.67, -11.55) * mm, "end": v(6.14, -13.16) * mm});
            skLineSegment(sketch, "E41.7.3", {"start": v(7.5, -17.43) * mm, "end": v(6.06, -12.91) * mm});
            skArc(sketch, "E41.8.0", {"start": v(14.82, -10.98) * mm, "mid": v(18.42, -10.64) * mm, "end": v(16.91, -7.34) * mm});
            skLineSegment(sketch, "E41.8.1", {"start": v(17.43, -7.5) * mm, "end": v(12.91, -6.06) * mm});
            skArc(sketch, "E41.8.2", {"start": v(13.16, -6.14) * mm, "mid": v(11.55, -6.67) * mm, "end": v(11.9, -8.32) * mm});
            skLineSegment(sketch, "E41.8.3", {"start": v(15.21, -11.34) * mm, "end": v(11.7, -8.15) * mm});
            skArc(sketch, "E41.9.0", {"start": v(18.32, -2.1) * mm, "mid": v(21.27, 0) * mm, "end": v(18.32, 2.1) * mm});
            skLineSegment(sketch, "E41.9.1", {"start": v(18.85, 2.21) * mm, "end": v(14.21, 1.2) * mm});
            skArc(sketch, "E41.9.2", {"start": v(14.46, 1.26) * mm, "mid": v(13.33, 0) * mm, "end": v(14.46, -1.26) * mm});
            skLineSegment(sketch, "E41.9.3", {"start": v(18.85, -2.21) * mm, "end": v(14.21, -1.2) * mm});
            skArc(sketch, "E41.10.0", {"start": v(16.91, 7.34) * mm, "mid": v(18.42, 10.64) * mm, "end": v(14.82, 10.98) * mm});
            skLineSegment(sketch, "E41.10.1", {"start": v(15.21, 11.34) * mm, "end": v(11.7, 8.15) * mm});
            skArc(sketch, "E41.10.2", {"start": v(11.9, 8.32) * mm, "mid": v(11.55, 6.67) * mm, "end": v(13.16, 6.14) * mm});
            skLineSegment(sketch, "E41.10.3", {"start": v(17.43, 7.5) * mm, "end": v(12.91, 6.06) * mm});
            skArc(sketch, "E41.11.0", {"start": v(10.98, 14.82) * mm, "mid": v(10.64, 18.42) * mm, "end": v(7.34, 16.91) * mm});
            skLineSegment(sketch, "E41.11.1", {"start": v(7.5, 17.43) * mm, "end": v(6.06, 12.91) * mm});
            skArc(sketch, "E41.11.2", {"start": v(6.14, 13.16) * mm, "mid": v(6.67, 11.55) * mm, "end": v(8.32, 11.9) * mm});
            skLineSegment(sketch, "E41.11.3", {"start": v(11.34, 15.21) * mm, "end": v(8.15, 11.7) * mm});
            skSolve(sketch);
        }
        {
            var Q0;
            {var subQ0=sQuery(id+"F0.wireOp",EDGE,"E12");var subQ1=sQuery(id+"F0.wireOp",EDGE,"E2");var subQ2=makeQuery(id+"F0.imprint","INTERSECT",VERTEX,{"disambiguationData":[OD(0.0)],"derivedFrom":[subQ1,subQ0]});Q0=makeQuery(id+"F0.imprint","IMPRINT",FACE,{"disambiguationData":[TD([[makeQuery(id+"F0.imprint","IMPRINT",EDGE,{"disambiguationData":[TD([[subQ2,1.0]])],"derivedFrom":subQ1}),-1.0]])]});}
            var Q1;
            {var subQ0=sQuery(id+"F0.wireOp",EDGE,"E11");var subQ1=sQuery(id+"F0.wireOp",EDGE,"E6.MirrorCS");var subQ2=makeQuery(id+"F0.imprint","INTERSECT",VERTEX,{"disambiguationData":[OD(0.0)],"derivedFrom":[subQ1,subQ0]});Q1=makeQuery(id+"F0.imprint","IMPRINT",FACE,{"disambiguationData":[TD([[makeQuery(id+"F0.imprint","IMPRINT",EDGE,{"disambiguationData":[TD([[subQ2,1.0]])],"derivedFrom":subQ1}),1.0]])]});}
            var Q2;
            {var subQ0=sQuery(id+"F0.wireOp",EDGE,"E13.1.1");var subQ1=sQuery(id+"F0.wireOp",EDGE,"E13.1.0");var subQ2=makeQuery(id+"F0.imprint","INTERSECT",VERTEX,{"disambiguationData":[OD(0.0)],"derivedFrom":[subQ1,subQ0]});Q2=makeQuery(id+"F0.imprint","IMPRINT",FACE,{"disambiguationData":[TD([[makeQuery(id+"F0.imprint","IMPRINT",EDGE,{"disambiguationData":[TD([[subQ2,1.0]])],"derivedFrom":subQ1}),1.0]])]});}
            var Q3;
            {var subQ0=sQuery(id+"F0.wireOp",EDGE,"E13.1.10");var subQ1=sQuery(id+"F0.wireOp",EDGE,"E13.1.9");var subQ2=makeQuery(id+"F0.imprint","INTERSECT",VERTEX,{"disambiguationData":[OD(0.0)],"derivedFrom":[subQ1,subQ0]});Q3=makeQuery(id+"F0.imprint","IMPRINT",FACE,{"disambiguationData":[TD([[makeQuery(id+"F0.imprint","IMPRINT",EDGE,{"disambiguationData":[TD([[subQ2,1.0]])],"derivedFrom":subQ1}),-1.0]])]});}
            var Q4;
            {var subQ0=sQuery(id+"F0.wireOp",EDGE,"E13.2.1");var subQ1=sQuery(id+"F0.wireOp",EDGE,"E13.2.0");var subQ2=makeQuery(id+"F0.imprint","INTERSECT",VERTEX,{"disambiguationData":[OD(0.0)],"derivedFrom":[subQ1,subQ0]});Q4=makeQuery(id+"F0.imprint","IMPRINT",FACE,{"disambiguationData":[TD([[makeQuery(id+"F0.imprint","IMPRINT",EDGE,{"disambiguationData":[TD([[subQ2,1.0]])],"derivedFrom":subQ1}),1.0]])]});}
            var Q5;
            {var subQ0=sQuery(id+"F0.wireOp",EDGE,"E13.2.10");var subQ1=sQuery(id+"F0.wireOp",EDGE,"E13.2.9");var subQ2=makeQuery(id+"F0.imprint","INTERSECT",VERTEX,{"disambiguationData":[OD(0.0)],"derivedFrom":[subQ1,subQ0]});Q5=makeQuery(id+"F0.imprint","IMPRINT",FACE,{"disambiguationData":[TD([[makeQuery(id+"F0.imprint","IMPRINT",EDGE,{"disambiguationData":[TD([[subQ2,1.0]])],"derivedFrom":subQ1}),-1.0]])]});}
            var Q6;
            {var subQ0=sQuery(id+"F0.wireOp",EDGE,"E13.3.1");var subQ1=sQuery(id+"F0.wireOp",EDGE,"E13.3.0");var subQ2=makeQuery(id+"F0.imprint","INTERSECT",VERTEX,{"disambiguationData":[OD(0.0)],"derivedFrom":[subQ1,subQ0]});Q6=makeQuery(id+"F0.imprint","IMPRINT",FACE,{"disambiguationData":[TD([[makeQuery(id+"F0.imprint","IMPRINT",EDGE,{"disambiguationData":[TD([[subQ2,1.0]])],"derivedFrom":subQ1}),1.0]])]});}
            var Q7;
            {var subQ0=sQuery(id+"F0.wireOp",EDGE,"E13.3.10");var subQ1=sQuery(id+"F0.wireOp",EDGE,"E13.3.9");var subQ2=makeQuery(id+"F0.imprint","INTERSECT",VERTEX,{"disambiguationData":[OD(0.0)],"derivedFrom":[subQ1,subQ0]});Q7=makeQuery(id+"F0.imprint","IMPRINT",FACE,{"disambiguationData":[TD([[makeQuery(id+"F0.imprint","IMPRINT",EDGE,{"disambiguationData":[TD([[subQ2,1.0]])],"derivedFrom":subQ1}),-1.0]])]});}
            var Q8;
            {var subQ0=sQuery(id+"F0.wireOp",EDGE,"E13.4.1");var subQ1=sQuery(id+"F0.wireOp",EDGE,"E13.4.0");var subQ2=makeQuery(id+"F0.imprint","INTERSECT",VERTEX,{"disambiguationData":[OD(0.0)],"derivedFrom":[subQ1,subQ0]});Q8=makeQuery(id+"F0.imprint","IMPRINT",FACE,{"disambiguationData":[TD([[makeQuery(id+"F0.imprint","IMPRINT",EDGE,{"disambiguationData":[TD([[subQ2,1.0]])],"derivedFrom":subQ1}),1.0]])]});}
            var Q9;
            {var subQ0=sQuery(id+"F0.wireOp",EDGE,"E13.4.10");var subQ1=sQuery(id+"F0.wireOp",EDGE,"E13.4.9");var subQ2=makeQuery(id+"F0.imprint","INTERSECT",VERTEX,{"disambiguationData":[OD(0.0)],"derivedFrom":[subQ1,subQ0]});Q9=makeQuery(id+"F0.imprint","IMPRINT",FACE,{"disambiguationData":[TD([[makeQuery(id+"F0.imprint","IMPRINT",EDGE,{"disambiguationData":[TD([[subQ2,1.0]])],"derivedFrom":subQ1}),-1.0]])]});}
            var Q10;
            {var subQ0=sQuery(id+"F0.wireOp",EDGE,"E13.5.1");var subQ1=sQuery(id+"F0.wireOp",EDGE,"E13.5.0");var subQ2=makeQuery(id+"F0.imprint","INTERSECT",VERTEX,{"disambiguationData":[OD(0.0)],"derivedFrom":[subQ1,subQ0]});Q10=makeQuery(id+"F0.imprint","IMPRINT",FACE,{"disambiguationData":[TD([[makeQuery(id+"F0.imprint","IMPRINT",EDGE,{"disambiguationData":[TD([[subQ2,1.0]])],"derivedFrom":subQ1}),1.0]])]});}
            var Q11;
            {var subQ0=sQuery(id+"F0.wireOp",EDGE,"E13.5.10");var subQ1=sQuery(id+"F0.wireOp",EDGE,"E13.5.9");var subQ2=makeQuery(id+"F0.imprint","INTERSECT",VERTEX,{"disambiguationData":[OD(0.0)],"derivedFrom":[subQ1,subQ0]});Q11=makeQuery(id+"F0.imprint","IMPRINT",FACE,{"disambiguationData":[TD([[makeQuery(id+"F0.imprint","IMPRINT",EDGE,{"disambiguationData":[TD([[subQ2,1.0]])],"derivedFrom":subQ1}),-1.0]])]});}
            var Q12;
            {var subQ0=sQuery(id+"F0.wireOp",EDGE,"E13.6.1");var subQ1=sQuery(id+"F0.wireOp",EDGE,"E13.6.0");var subQ2=makeQuery(id+"F0.imprint","INTERSECT",VERTEX,{"disambiguationData":[OD(0.0)],"derivedFrom":[subQ1,subQ0]});Q12=makeQuery(id+"F0.imprint","IMPRINT",FACE,{"disambiguationData":[TD([[makeQuery(id+"F0.imprint","IMPRINT",EDGE,{"disambiguationData":[TD([[subQ2,1.0]])],"derivedFrom":subQ1}),1.0]])]});}
            var Q13;
            {var subQ0=sQuery(id+"F0.wireOp",EDGE,"E13.6.10");var subQ1=sQuery(id+"F0.wireOp",EDGE,"E13.6.9");var subQ2=makeQuery(id+"F0.imprint","INTERSECT",VERTEX,{"disambiguationData":[OD(0.0)],"derivedFrom":[subQ1,subQ0]});Q13=makeQuery(id+"F0.imprint","IMPRINT",FACE,{"disambiguationData":[TD([[makeQuery(id+"F0.imprint","IMPRINT",EDGE,{"disambiguationData":[TD([[subQ2,1.0]])],"derivedFrom":subQ1}),-1.0]])]});}
            var Q14;
            {var subQ0=sQuery(id+"F0.wireOp",EDGE,"E13.7.1");var subQ1=sQuery(id+"F0.wireOp",EDGE,"E13.7.0");var subQ2=makeQuery(id+"F0.imprint","INTERSECT",VERTEX,{"disambiguationData":[OD(0.0)],"derivedFrom":[subQ1,subQ0]});Q14=makeQuery(id+"F0.imprint","IMPRINT",FACE,{"disambiguationData":[TD([[makeQuery(id+"F0.imprint","IMPRINT",EDGE,{"disambiguationData":[TD([[subQ2,1.0]])],"derivedFrom":subQ1}),1.0]])]});}
            var Q15;
            {var subQ0=sQuery(id+"F0.wireOp",EDGE,"E13.7.10");var subQ1=sQuery(id+"F0.wireOp",EDGE,"E13.7.9");var subQ2=makeQuery(id+"F0.imprint","INTERSECT",VERTEX,{"disambiguationData":[OD(0.0)],"derivedFrom":[subQ1,subQ0]});Q15=makeQuery(id+"F0.imprint","IMPRINT",FACE,{"disambiguationData":[TD([[makeQuery(id+"F0.imprint","IMPRINT",EDGE,{"disambiguationData":[TD([[subQ2,1.0]])],"derivedFrom":subQ1}),-1.0]])]});}
            var Q16;
            {var subQ0=sQuery(id+"F0.wireOp",EDGE,"E13.8.1");var subQ1=sQuery(id+"F0.wireOp",EDGE,"E13.8.0");var subQ2=makeQuery(id+"F0.imprint","INTERSECT",VERTEX,{"disambiguationData":[OD(0.0)],"derivedFrom":[subQ1,subQ0]});Q16=makeQuery(id+"F0.imprint","IMPRINT",FACE,{"disambiguationData":[TD([[makeQuery(id+"F0.imprint","IMPRINT",EDGE,{"disambiguationData":[TD([[subQ2,1.0]])],"derivedFrom":subQ1}),1.0]])]});}
            var Q17;
            {var subQ0=sQuery(id+"F0.wireOp",EDGE,"E13.8.10");var subQ1=sQuery(id+"F0.wireOp",EDGE,"E13.8.9");var subQ2=makeQuery(id+"F0.imprint","INTERSECT",VERTEX,{"disambiguationData":[OD(0.0)],"derivedFrom":[subQ1,subQ0]});Q17=makeQuery(id+"F0.imprint","IMPRINT",FACE,{"disambiguationData":[TD([[makeQuery(id+"F0.imprint","IMPRINT",EDGE,{"disambiguationData":[TD([[subQ2,1.0]])],"derivedFrom":subQ1}),-1.0]])]});}
            var Q18;
            {var subQ0=sQuery(id+"F0.wireOp",EDGE,"E13.9.1");var subQ1=sQuery(id+"F0.wireOp",EDGE,"E13.9.0");var subQ2=makeQuery(id+"F0.imprint","INTERSECT",VERTEX,{"disambiguationData":[OD(0.0)],"derivedFrom":[subQ1,subQ0]});Q18=makeQuery(id+"F0.imprint","IMPRINT",FACE,{"disambiguationData":[TD([[makeQuery(id+"F0.imprint","IMPRINT",EDGE,{"disambiguationData":[TD([[subQ2,1.0]])],"derivedFrom":subQ1}),1.0]])]});}
            var Q19;
            {var subQ0=sQuery(id+"F0.wireOp",EDGE,"E13.9.10");var subQ1=sQuery(id+"F0.wireOp",EDGE,"E13.9.9");var subQ2=makeQuery(id+"F0.imprint","INTERSECT",VERTEX,{"disambiguationData":[OD(0.0)],"derivedFrom":[subQ1,subQ0]});Q19=makeQuery(id+"F0.imprint","IMPRINT",FACE,{"disambiguationData":[TD([[makeQuery(id+"F0.imprint","IMPRINT",EDGE,{"disambiguationData":[TD([[subQ2,1.0]])],"derivedFrom":subQ1}),-1.0]])]});}
            var Q20;
            {var subQ0=sQuery(id+"F0.wireOp",EDGE,"E13.10.1");var subQ1=sQuery(id+"F0.wireOp",EDGE,"E13.10.0");var subQ2=makeQuery(id+"F0.imprint","INTERSECT",VERTEX,{"disambiguationData":[OD(0.0)],"derivedFrom":[subQ1,subQ0]});Q20=makeQuery(id+"F0.imprint","IMPRINT",FACE,{"disambiguationData":[TD([[makeQuery(id+"F0.imprint","IMPRINT",EDGE,{"disambiguationData":[TD([[subQ2,1.0]])],"derivedFrom":subQ1}),1.0]])]});}
            var Q21;
            {var subQ0=sQuery(id+"F0.wireOp",EDGE,"E13.10.10");var subQ1=sQuery(id+"F0.wireOp",EDGE,"E13.10.9");var subQ2=makeQuery(id+"F0.imprint","INTERSECT",VERTEX,{"disambiguationData":[OD(0.0)],"derivedFrom":[subQ1,subQ0]});Q21=makeQuery(id+"F0.imprint","IMPRINT",FACE,{"disambiguationData":[TD([[makeQuery(id+"F0.imprint","IMPRINT",EDGE,{"disambiguationData":[TD([[subQ2,1.0]])],"derivedFrom":subQ1}),-1.0]])]});}
            var Q22;
            {var subQ0=sQuery(id+"F0.wireOp",EDGE,"E13.11.1");var subQ1=sQuery(id+"F0.wireOp",EDGE,"E13.11.0");var subQ2=makeQuery(id+"F0.imprint","INTERSECT",VERTEX,{"disambiguationData":[OD(0.0)],"derivedFrom":[subQ1,subQ0]});Q22=makeQuery(id+"F0.imprint","IMPRINT",FACE,{"disambiguationData":[TD([[makeQuery(id+"F0.imprint","IMPRINT",EDGE,{"disambiguationData":[TD([[subQ2,1.0]])],"derivedFrom":subQ1}),1.0]])]});}
            var Q23;
            {var subQ0=sQuery(id+"F0.wireOp",EDGE,"E13.11.10");var subQ1=sQuery(id+"F0.wireOp",EDGE,"E13.11.9");var subQ2=makeQuery(id+"F0.imprint","INTERSECT",VERTEX,{"disambiguationData":[OD(0.0)],"derivedFrom":[subQ1,subQ0]});Q23=makeQuery(id+"F0.imprint","IMPRINT",FACE,{"disambiguationData":[TD([[makeQuery(id+"F0.imprint","IMPRINT",EDGE,{"disambiguationData":[TD([[subQ2,1.0]])],"derivedFrom":subQ1}),-1.0]])]});}
            var Q24;
            {var subQ0=sQuery(id+"F0.wireOp",EDGE,"E13.12.1");var subQ1=sQuery(id+"F0.wireOp",EDGE,"E13.12.0");var subQ2=makeQuery(id+"F0.imprint","INTERSECT",VERTEX,{"disambiguationData":[OD(0.0)],"derivedFrom":[subQ1,subQ0]});Q24=makeQuery(id+"F0.imprint","IMPRINT",FACE,{"disambiguationData":[TD([[makeQuery(id+"F0.imprint","IMPRINT",EDGE,{"disambiguationData":[TD([[subQ2,1.0]])],"derivedFrom":subQ1}),1.0]])]});}
            var Q25;
            {var subQ0=sQuery(id+"F0.wireOp",EDGE,"E13.12.10");var subQ1=sQuery(id+"F0.wireOp",EDGE,"E13.12.9");var subQ2=makeQuery(id+"F0.imprint","INTERSECT",VERTEX,{"disambiguationData":[OD(0.0)],"derivedFrom":[subQ1,subQ0]});Q25=makeQuery(id+"F0.imprint","IMPRINT",FACE,{"disambiguationData":[TD([[makeQuery(id+"F0.imprint","IMPRINT",EDGE,{"disambiguationData":[TD([[subQ2,1.0]])],"derivedFrom":subQ1}),-1.0]])]});}
            var Q26;
            {var subQ0=sQuery(id+"F0.wireOp",EDGE,"E13.13.1");var subQ1=sQuery(id+"F0.wireOp",EDGE,"E13.13.0");var subQ2=makeQuery(id+"F0.imprint","INTERSECT",VERTEX,{"disambiguationData":[OD(0.0)],"derivedFrom":[subQ1,subQ0]});Q26=makeQuery(id+"F0.imprint","IMPRINT",FACE,{"disambiguationData":[TD([[makeQuery(id+"F0.imprint","IMPRINT",EDGE,{"disambiguationData":[TD([[subQ2,1.0]])],"derivedFrom":subQ1}),1.0]])]});}
            var Q27;
            {var subQ0=sQuery(id+"F0.wireOp",EDGE,"E13.13.10");var subQ1=sQuery(id+"F0.wireOp",EDGE,"E13.13.9");var subQ2=makeQuery(id+"F0.imprint","INTERSECT",VERTEX,{"disambiguationData":[OD(0.0)],"derivedFrom":[subQ1,subQ0]});Q27=makeQuery(id+"F0.imprint","IMPRINT",FACE,{"disambiguationData":[TD([[makeQuery(id+"F0.imprint","IMPRINT",EDGE,{"disambiguationData":[TD([[subQ2,1.0]])],"derivedFrom":subQ1}),-1.0]])]});}
            var Q28;
            {var subQ0=sQuery(id+"F0.wireOp",EDGE,"E13.14.1");var subQ1=sQuery(id+"F0.wireOp",EDGE,"E13.14.0");var subQ2=makeQuery(id+"F0.imprint","INTERSECT",VERTEX,{"disambiguationData":[OD(0.0)],"derivedFrom":[subQ1,subQ0]});Q28=makeQuery(id+"F0.imprint","IMPRINT",FACE,{"disambiguationData":[TD([[makeQuery(id+"F0.imprint","IMPRINT",EDGE,{"disambiguationData":[TD([[subQ2,1.0]])],"derivedFrom":subQ1}),1.0]])]});}
            var Q29;
            {var subQ0=sQuery(id+"F0.wireOp",EDGE,"E13.14.10");var subQ1=sQuery(id+"F0.wireOp",EDGE,"E13.14.9");var subQ2=makeQuery(id+"F0.imprint","INTERSECT",VERTEX,{"disambiguationData":[OD(0.0)],"derivedFrom":[subQ1,subQ0]});Q29=makeQuery(id+"F0.imprint","IMPRINT",FACE,{"disambiguationData":[TD([[makeQuery(id+"F0.imprint","IMPRINT",EDGE,{"disambiguationData":[TD([[subQ2,1.0]])],"derivedFrom":subQ1}),-1.0]])]});}
            var Q30;
            {var subQ0=sQuery(id+"F0.wireOp",EDGE,"E13.15.1");var subQ1=sQuery(id+"F0.wireOp",EDGE,"E13.15.0");var subQ2=makeQuery(id+"F0.imprint","INTERSECT",VERTEX,{"disambiguationData":[OD(0.0)],"derivedFrom":[subQ1,subQ0]});Q30=makeQuery(id+"F0.imprint","IMPRINT",FACE,{"disambiguationData":[TD([[makeQuery(id+"F0.imprint","IMPRINT",EDGE,{"disambiguationData":[TD([[subQ2,1.0]])],"derivedFrom":subQ1}),1.0]])]});}
            var Q31;
            {var subQ0=sQuery(id+"F0.wireOp",EDGE,"E13.15.10");var subQ1=sQuery(id+"F0.wireOp",EDGE,"E13.15.9");var subQ2=makeQuery(id+"F0.imprint","INTERSECT",VERTEX,{"disambiguationData":[OD(0.0)],"derivedFrom":[subQ1,subQ0]});Q31=makeQuery(id+"F0.imprint","IMPRINT",FACE,{"disambiguationData":[TD([[makeQuery(id+"F0.imprint","IMPRINT",EDGE,{"disambiguationData":[TD([[subQ2,1.0]])],"derivedFrom":subQ1}),-1.0]])]});}
            var Q32;
            {var subQ0=sQuery(id+"F0.wireOp",EDGE,"E13.16.1");var subQ1=sQuery(id+"F0.wireOp",EDGE,"E13.16.0");var subQ2=makeQuery(id+"F0.imprint","INTERSECT",VERTEX,{"disambiguationData":[OD(0.0)],"derivedFrom":[subQ1,subQ0]});Q32=makeQuery(id+"F0.imprint","IMPRINT",FACE,{"disambiguationData":[TD([[makeQuery(id+"F0.imprint","IMPRINT",EDGE,{"disambiguationData":[TD([[subQ2,1.0]])],"derivedFrom":subQ1}),1.0]])]});}
            var Q33;
            {var subQ0=sQuery(id+"F0.wireOp",EDGE,"E13.16.10");var subQ1=sQuery(id+"F0.wireOp",EDGE,"E13.16.9");var subQ2=makeQuery(id+"F0.imprint","INTERSECT",VERTEX,{"disambiguationData":[OD(0.0)],"derivedFrom":[subQ1,subQ0]});Q33=makeQuery(id+"F0.imprint","IMPRINT",FACE,{"disambiguationData":[TD([[makeQuery(id+"F0.imprint","IMPRINT",EDGE,{"disambiguationData":[TD([[subQ2,1.0]])],"derivedFrom":subQ1}),-1.0]])]});}
            var Q34;
            {var subQ0=sQuery(id+"F0.wireOp",EDGE,"E13.17.1");var subQ1=sQuery(id+"F0.wireOp",EDGE,"E13.17.0");var subQ2=makeQuery(id+"F0.imprint","INTERSECT",VERTEX,{"disambiguationData":[OD(0.0)],"derivedFrom":[subQ1,subQ0]});Q34=makeQuery(id+"F0.imprint","IMPRINT",FACE,{"disambiguationData":[TD([[makeQuery(id+"F0.imprint","IMPRINT",EDGE,{"disambiguationData":[TD([[subQ2,1.0]])],"derivedFrom":subQ1}),1.0]])]});}
            var Q35;
            {var subQ0=sQuery(id+"F0.wireOp",EDGE,"E13.17.10");var subQ1=sQuery(id+"F0.wireOp",EDGE,"E13.17.9");var subQ2=makeQuery(id+"F0.imprint","INTERSECT",VERTEX,{"disambiguationData":[OD(0.0)],"derivedFrom":[subQ1,subQ0]});Q35=makeQuery(id+"F0.imprint","IMPRINT",FACE,{"disambiguationData":[TD([[makeQuery(id+"F0.imprint","IMPRINT",EDGE,{"disambiguationData":[TD([[subQ2,1.0]])],"derivedFrom":subQ1}),-1.0]])]});}
            var Q36;
            {var subQ0=sQuery(id+"F0.wireOp",EDGE,"E13.18.1");var subQ1=sQuery(id+"F0.wireOp",EDGE,"E13.18.0");var subQ2=makeQuery(id+"F0.imprint","INTERSECT",VERTEX,{"disambiguationData":[OD(0.0)],"derivedFrom":[subQ1,subQ0]});Q36=makeQuery(id+"F0.imprint","IMPRINT",FACE,{"disambiguationData":[TD([[makeQuery(id+"F0.imprint","IMPRINT",EDGE,{"disambiguationData":[TD([[subQ2,1.0]])],"derivedFrom":subQ1}),1.0]])]});}
            var Q37;
            {var subQ0=sQuery(id+"F0.wireOp",EDGE,"E13.18.10");var subQ1=sQuery(id+"F0.wireOp",EDGE,"E13.18.9");var subQ2=makeQuery(id+"F0.imprint","INTERSECT",VERTEX,{"disambiguationData":[OD(0.0)],"derivedFrom":[subQ1,subQ0]});Q37=makeQuery(id+"F0.imprint","IMPRINT",FACE,{"disambiguationData":[TD([[makeQuery(id+"F0.imprint","IMPRINT",EDGE,{"disambiguationData":[TD([[subQ2,1.0]])],"derivedFrom":subQ1}),-1.0]])]});}
            var Q38;
            {var subQ0=sQuery(id+"F0.wireOp",EDGE,"E13.19.1");var subQ1=sQuery(id+"F0.wireOp",EDGE,"E13.19.0");var subQ2=makeQuery(id+"F0.imprint","INTERSECT",VERTEX,{"disambiguationData":[OD(0.0)],"derivedFrom":[subQ1,subQ0]});Q38=makeQuery(id+"F0.imprint","IMPRINT",FACE,{"disambiguationData":[TD([[makeQuery(id+"F0.imprint","IMPRINT",EDGE,{"disambiguationData":[TD([[subQ2,1.0]])],"derivedFrom":subQ1}),1.0]])]});}
            var Q39;
            {var subQ0=sQuery(id+"F0.wireOp",EDGE,"E13.19.10");var subQ1=sQuery(id+"F0.wireOp",EDGE,"E13.19.9");var subQ2=makeQuery(id+"F0.imprint","INTERSECT",VERTEX,{"disambiguationData":[OD(0.0)],"derivedFrom":[subQ1,subQ0]});Q39=makeQuery(id+"F0.imprint","IMPRINT",FACE,{"disambiguationData":[TD([[makeQuery(id+"F0.imprint","IMPRINT",EDGE,{"disambiguationData":[TD([[subQ2,1.0]])],"derivedFrom":subQ1}),-1.0]])]});}
            var Q40;
            {var subQ0=sQuery(id+"F0.wireOp",EDGE,"E13.20.1");var subQ1=sQuery(id+"F0.wireOp",EDGE,"E13.20.0");var subQ2=makeQuery(id+"F0.imprint","INTERSECT",VERTEX,{"disambiguationData":[OD(0.0)],"derivedFrom":[subQ1,subQ0]});Q40=makeQuery(id+"F0.imprint","IMPRINT",FACE,{"disambiguationData":[TD([[makeQuery(id+"F0.imprint","IMPRINT",EDGE,{"disambiguationData":[TD([[subQ2,1.0]])],"derivedFrom":subQ1}),1.0]])]});}
            var Q41;
            {var subQ0=sQuery(id+"F0.wireOp",EDGE,"E13.20.10");var subQ1=sQuery(id+"F0.wireOp",EDGE,"E13.20.9");var subQ2=makeQuery(id+"F0.imprint","INTERSECT",VERTEX,{"disambiguationData":[OD(0.0)],"derivedFrom":[subQ1,subQ0]});Q41=makeQuery(id+"F0.imprint","IMPRINT",FACE,{"disambiguationData":[TD([[makeQuery(id+"F0.imprint","IMPRINT",EDGE,{"disambiguationData":[TD([[subQ2,1.0]])],"derivedFrom":subQ1}),-1.0]])]});}
            var Q42;
            {var subQ0=sQuery(id+"F0.wireOp",EDGE,"E13.21.1");var subQ1=sQuery(id+"F0.wireOp",EDGE,"E13.21.0");var subQ2=makeQuery(id+"F0.imprint","INTERSECT",VERTEX,{"disambiguationData":[OD(0.0)],"derivedFrom":[subQ1,subQ0]});Q42=makeQuery(id+"F0.imprint","IMPRINT",FACE,{"disambiguationData":[TD([[makeQuery(id+"F0.imprint","IMPRINT",EDGE,{"disambiguationData":[TD([[subQ2,1.0]])],"derivedFrom":subQ1}),1.0]])]});}
            var Q43;
            {var subQ0=sQuery(id+"F0.wireOp",EDGE,"E13.21.10");var subQ1=sQuery(id+"F0.wireOp",EDGE,"E13.21.9");var subQ2=makeQuery(id+"F0.imprint","INTERSECT",VERTEX,{"disambiguationData":[OD(0.0)],"derivedFrom":[subQ1,subQ0]});Q43=makeQuery(id+"F0.imprint","IMPRINT",FACE,{"disambiguationData":[TD([[makeQuery(id+"F0.imprint","IMPRINT",EDGE,{"disambiguationData":[TD([[subQ2,1.0]])],"derivedFrom":subQ1}),-1.0]])]});}
            var Q44;
            {var subQ0=sQuery(id+"F0.wireOp",EDGE,"E13.22.1");var subQ1=sQuery(id+"F0.wireOp",EDGE,"E13.22.0");var subQ2=makeQuery(id+"F0.imprint","INTERSECT",VERTEX,{"disambiguationData":[OD(0.0)],"derivedFrom":[subQ1,subQ0]});Q44=makeQuery(id+"F0.imprint","IMPRINT",FACE,{"disambiguationData":[TD([[makeQuery(id+"F0.imprint","IMPRINT",EDGE,{"disambiguationData":[TD([[subQ2,1.0]])],"derivedFrom":subQ1}),1.0]])]});}
            var Q45;
            {var subQ0=sQuery(id+"F0.wireOp",EDGE,"E13.22.10");var subQ1=sQuery(id+"F0.wireOp",EDGE,"E13.22.9");var subQ2=makeQuery(id+"F0.imprint","INTERSECT",VERTEX,{"disambiguationData":[OD(0.0)],"derivedFrom":[subQ1,subQ0]});Q45=makeQuery(id+"F0.imprint","IMPRINT",FACE,{"disambiguationData":[TD([[makeQuery(id+"F0.imprint","IMPRINT",EDGE,{"disambiguationData":[TD([[subQ2,1.0]])],"derivedFrom":subQ1}),-1.0]])]});}
            var Q46;
            {var subQ0=sQuery(id+"F0.wireOp",EDGE,"E13.23.1");var subQ1=sQuery(id+"F0.wireOp",EDGE,"E13.23.0");var subQ2=makeQuery(id+"F0.imprint","INTERSECT",VERTEX,{"disambiguationData":[OD(0.0)],"derivedFrom":[subQ1,subQ0]});Q46=makeQuery(id+"F0.imprint","IMPRINT",FACE,{"disambiguationData":[TD([[makeQuery(id+"F0.imprint","IMPRINT",EDGE,{"disambiguationData":[TD([[subQ2,1.0]])],"derivedFrom":subQ1}),1.0]])]});}
            var Q47;
            {var subQ0=sQuery(id+"F0.wireOp",EDGE,"E13.23.10");var subQ1=sQuery(id+"F0.wireOp",EDGE,"E13.23.9");var subQ2=makeQuery(id+"F0.imprint","INTERSECT",VERTEX,{"disambiguationData":[OD(0.0)],"derivedFrom":[subQ1,subQ0]});Q47=makeQuery(id+"F0.imprint","IMPRINT",FACE,{"disambiguationData":[TD([[makeQuery(id+"F0.imprint","IMPRINT",EDGE,{"disambiguationData":[TD([[subQ2,1.0]])],"derivedFrom":subQ1}),-1.0]])]});}
            var Q48;
            {var subQ0=sQuery(id+"F0.wireOp",EDGE,"E11");var subQ1=sQuery(id+"F0.wireOp",EDGE,"E0");var subQ2=makeQuery(id+"F0.imprint","INTERSECT",VERTEX,{"disambiguationData":[OD(0.0)],"derivedFrom":[subQ1,subQ0]});Q48=makeQuery(id+"F0.imprint","IMPRINT",FACE,{"disambiguationData":[TD([[makeQuery(id+"F0.imprint","IMPRINT",EDGE,{"disambiguationData":[TD([[subQ2,-1.0]])],"derivedFrom":subQ1}),1.0]])]});}
            var Q49;
            {var subQ0=sQuery(id+"F0.wireOp",EDGE,"E11");var subQ1=sQuery(id+"F0.wireOp",EDGE,"E0");var subQ2=makeQuery(id+"F0.imprint","INTERSECT",VERTEX,{"disambiguationData":[OD(1.0)],"derivedFrom":[subQ1,subQ0]});Q49=makeQuery(id+"F0.imprint","IMPRINT",FACE,{"disambiguationData":[TD([[makeQuery(id+"F0.imprint","IMPRINT",EDGE,{"disambiguationData":[TD([[subQ2,1.0]])],"derivedFrom":subQ1}),1.0]])]});}
            var Q50;
            {var subQ0=sQuery(id+"F0.wireOp",EDGE,"E13.1.10");var subQ1=sQuery(id+"F0.wireOp",EDGE,"E0");var subQ2=makeQuery(id+"F0.imprint","INTERSECT",VERTEX,{"disambiguationData":[OD(0.0)],"derivedFrom":[subQ1,subQ0]});Q50=makeQuery(id+"F0.imprint","IMPRINT",FACE,{"disambiguationData":[TD([[makeQuery(id+"F0.imprint","IMPRINT",EDGE,{"disambiguationData":[TD([[subQ2,1.0]])],"derivedFrom":subQ1}),1.0]])]});}
            var Q51;
            {var subQ0=sQuery(id+"F0.wireOp",EDGE,"E17.trimOffspring");var subQ1=sQuery(id+"F0.wireOp",EDGE,"E12");var subQ2=makeQuery(id+"F0.imprint","INTERSECT",VERTEX,{"disambiguationData":[OD(1.0)],"derivedFrom":[subQ1,subQ0]});Q51=makeQuery(id+"F0.imprint","IMPRINT",FACE,{"disambiguationData":[TD([[makeQuery(id+"F0.imprint","IMPRINT",EDGE,{"disambiguationData":[TD([[subQ2,-1.0]])],"derivedFrom":subQ1}),1.0]])]});}
            var Q52;
            {var subQ0=sQuery(id+"F0.wireOp",EDGE,"E17.trimOffspring");var subQ1=sQuery(id+"F0.wireOp",EDGE,"E12");var subQ2=makeQuery(id+"F0.imprint","INTERSECT",VERTEX,{"disambiguationData":[OD(0.0)],"derivedFrom":[subQ1,subQ0]});Q52=makeQuery(id+"F0.imprint","IMPRINT",FACE,{"disambiguationData":[TD([[makeQuery(id+"F0.imprint","IMPRINT",EDGE,{"disambiguationData":[TD([[subQ2,1.0]])],"derivedFrom":subQ1}),1.0]])]});}
            var Q53;
            {var subQ0=sQuery(id+"F0.wireOp",EDGE,"E17.trimOffspring");var subQ1=sQuery(id+"F0.wireOp",EDGE,"E12");var subQ2=makeQuery(id+"F0.imprint","INTERSECT",VERTEX,{"disambiguationData":[OD(0.0)],"derivedFrom":[subQ1,subQ0]});Q53=makeQuery(id+"F0.imprint","IMPRINT",FACE,{"disambiguationData":[TD([[makeQuery(id+"F0.imprint","IMPRINT",EDGE,{"disambiguationData":[TD([[subQ2,1.0]])],"derivedFrom":subQ1}),-1.0]])]});}
            var Q54;
            {var subQ0=sQuery(id+"F0.wireOp",EDGE,"E14.trimOffspring");var subQ1=sQuery(id+"F0.wireOp",EDGE,"E13.1.0");var subQ2=makeQuery(id+"F0.imprint","INTERSECT",VERTEX,{"disambiguationData":[OD(0.0)],"derivedFrom":[subQ1,subQ0]});Q54=makeQuery(id+"F0.imprint","IMPRINT",FACE,{"disambiguationData":[TD([[makeQuery(id+"F0.imprint","IMPRINT",EDGE,{"disambiguationData":[TD([[subQ2,-1.0]])],"derivedFrom":subQ1}),-1.0]])]});}
            var Q55;
            {var subQ0=sQuery(id+"F0.wireOp",EDGE,"E14.trimOffspring");var subQ1=sQuery(id+"F0.wireOp",EDGE,"E13.1.0");var subQ2=makeQuery(id+"F0.imprint","INTERSECT",VERTEX,{"disambiguationData":[OD(0.0)],"derivedFrom":[subQ1,subQ0]});Q55=makeQuery(id+"F0.imprint","IMPRINT",FACE,{"disambiguationData":[TD([[makeQuery(id+"F0.imprint","IMPRINT",EDGE,{"disambiguationData":[TD([[subQ2,-1.0]])],"derivedFrom":subQ1}),1.0]])]});}
            var Q56;
            {var subQ0=sQuery(id+"F0.wireOp",EDGE,"E14.trimOffspring");var subQ1=sQuery(id+"F0.wireOp",EDGE,"E13.1.0");var subQ2=makeQuery(id+"F0.imprint","INTERSECT",VERTEX,{"disambiguationData":[OD(1.0)],"derivedFrom":[subQ1,subQ0]});Q56=makeQuery(id+"F0.imprint","IMPRINT",FACE,{"disambiguationData":[TD([[makeQuery(id+"F0.imprint","IMPRINT",EDGE,{"disambiguationData":[TD([[subQ2,1.0]])],"derivedFrom":subQ1}),1.0]])]});}
            var Q57;
            {var subQ0=sQuery(id+"F0.wireOp",EDGE,"E16.trimOffspring");var subQ1=sQuery(id+"F0.wireOp",EDGE,"E13.2.0");var subQ2=makeQuery(id+"F0.imprint","INTERSECT",VERTEX,{"disambiguationData":[OD(0.0)],"derivedFrom":[subQ1,subQ0]});Q57=makeQuery(id+"F0.imprint","IMPRINT",FACE,{"disambiguationData":[TD([[makeQuery(id+"F0.imprint","IMPRINT",EDGE,{"disambiguationData":[TD([[subQ2,-1.0]])],"derivedFrom":subQ1}),-1.0]])]});}
            var Q58;
            {var subQ0=sQuery(id+"F0.wireOp",EDGE,"E16.trimOffspring");var subQ1=sQuery(id+"F0.wireOp",EDGE,"E13.2.0");var subQ2=makeQuery(id+"F0.imprint","INTERSECT",VERTEX,{"disambiguationData":[OD(0.0)],"derivedFrom":[subQ1,subQ0]});Q58=makeQuery(id+"F0.imprint","IMPRINT",FACE,{"disambiguationData":[TD([[makeQuery(id+"F0.imprint","IMPRINT",EDGE,{"disambiguationData":[TD([[subQ2,-1.0]])],"derivedFrom":subQ1}),1.0]])]});}
            var Q59;
            {var subQ0=sQuery(id+"F0.wireOp",EDGE,"E16.trimOffspring");var subQ1=sQuery(id+"F0.wireOp",EDGE,"E13.2.0");var subQ2=makeQuery(id+"F0.imprint","INTERSECT",VERTEX,{"disambiguationData":[OD(1.0)],"derivedFrom":[subQ1,subQ0]});Q59=makeQuery(id+"F0.imprint","IMPRINT",FACE,{"disambiguationData":[TD([[makeQuery(id+"F0.imprint","IMPRINT",EDGE,{"disambiguationData":[TD([[subQ2,1.0]])],"derivedFrom":subQ1}),1.0]])]});}
            var Q60;
            {var subQ0=sQuery(id+"F0.wireOp",EDGE,"E15.trimOffspring");var subQ1=sQuery(id+"F0.wireOp",EDGE,"E13.3.0");var subQ2=makeQuery(id+"F0.imprint","INTERSECT",VERTEX,{"disambiguationData":[OD(0.0)],"derivedFrom":[subQ1,subQ0]});Q60=makeQuery(id+"F0.imprint","IMPRINT",FACE,{"disambiguationData":[TD([[makeQuery(id+"F0.imprint","IMPRINT",EDGE,{"disambiguationData":[TD([[subQ2,-1.0]])],"derivedFrom":subQ1}),-1.0]])]});}
            var Q61;
            {var subQ0=sQuery(id+"F0.wireOp",EDGE,"E15.trimOffspring");var subQ1=sQuery(id+"F0.wireOp",EDGE,"E13.3.0");var subQ2=makeQuery(id+"F0.imprint","INTERSECT",VERTEX,{"disambiguationData":[OD(0.0)],"derivedFrom":[subQ1,subQ0]});Q61=makeQuery(id+"F0.imprint","IMPRINT",FACE,{"disambiguationData":[TD([[makeQuery(id+"F0.imprint","IMPRINT",EDGE,{"disambiguationData":[TD([[subQ2,-1.0]])],"derivedFrom":subQ1}),1.0]])]});}
            var Q62;
            {var subQ0=sQuery(id+"F0.wireOp",EDGE,"E15.trimOffspring");var subQ1=sQuery(id+"F0.wireOp",EDGE,"E13.3.0");var subQ2=makeQuery(id+"F0.imprint","INTERSECT",VERTEX,{"disambiguationData":[OD(1.0)],"derivedFrom":[subQ1,subQ0]});Q62=makeQuery(id+"F0.imprint","IMPRINT",FACE,{"disambiguationData":[TD([[makeQuery(id+"F0.imprint","IMPRINT",EDGE,{"disambiguationData":[TD([[subQ2,1.0]])],"derivedFrom":subQ1}),1.0]])]});}
            var Q63;
            {var subQ0=sQuery(id+"F0.wireOp",EDGE,"E36.trimOffspring");var subQ1=sQuery(id+"F0.wireOp",EDGE,"E13.4.0");var subQ2=makeQuery(id+"F0.imprint","INTERSECT",VERTEX,{"disambiguationData":[OD(0.0)],"derivedFrom":[subQ1,subQ0]});Q63=makeQuery(id+"F0.imprint","IMPRINT",FACE,{"disambiguationData":[TD([[makeQuery(id+"F0.imprint","IMPRINT",EDGE,{"disambiguationData":[TD([[subQ2,-1.0]])],"derivedFrom":subQ1}),-1.0]])]});}
            var Q64;
            {var subQ0=sQuery(id+"F0.wireOp",EDGE,"E36.trimOffspring");var subQ1=sQuery(id+"F0.wireOp",EDGE,"E13.4.0");var subQ2=makeQuery(id+"F0.imprint","INTERSECT",VERTEX,{"disambiguationData":[OD(0.0)],"derivedFrom":[subQ1,subQ0]});Q64=makeQuery(id+"F0.imprint","IMPRINT",FACE,{"disambiguationData":[TD([[makeQuery(id+"F0.imprint","IMPRINT",EDGE,{"disambiguationData":[TD([[subQ2,-1.0]])],"derivedFrom":subQ1}),1.0]])]});}
            var Q65;
            {var subQ0=sQuery(id+"F0.wireOp",EDGE,"E36.trimOffspring");var subQ1=sQuery(id+"F0.wireOp",EDGE,"E13.4.0");var subQ2=makeQuery(id+"F0.imprint","INTERSECT",VERTEX,{"disambiguationData":[OD(1.0)],"derivedFrom":[subQ1,subQ0]});Q65=makeQuery(id+"F0.imprint","IMPRINT",FACE,{"disambiguationData":[TD([[makeQuery(id+"F0.imprint","IMPRINT",EDGE,{"disambiguationData":[TD([[subQ2,1.0]])],"derivedFrom":subQ1}),1.0]])]});}
            var Q66;
            {var subQ0=sQuery(id+"F0.wireOp",EDGE,"E35.trimOffspring");var subQ1=sQuery(id+"F0.wireOp",EDGE,"E13.5.0");var subQ2=makeQuery(id+"F0.imprint","INTERSECT",VERTEX,{"disambiguationData":[OD(0.0)],"derivedFrom":[subQ1,subQ0]});Q66=makeQuery(id+"F0.imprint","IMPRINT",FACE,{"disambiguationData":[TD([[makeQuery(id+"F0.imprint","IMPRINT",EDGE,{"disambiguationData":[TD([[subQ2,-1.0]])],"derivedFrom":subQ1}),-1.0]])]});}
            var Q67;
            {var subQ0=sQuery(id+"F0.wireOp",EDGE,"E35.trimOffspring");var subQ1=sQuery(id+"F0.wireOp",EDGE,"E13.5.0");var subQ2=makeQuery(id+"F0.imprint","INTERSECT",VERTEX,{"disambiguationData":[OD(0.0)],"derivedFrom":[subQ1,subQ0]});Q67=makeQuery(id+"F0.imprint","IMPRINT",FACE,{"disambiguationData":[TD([[makeQuery(id+"F0.imprint","IMPRINT",EDGE,{"disambiguationData":[TD([[subQ2,-1.0]])],"derivedFrom":subQ1}),1.0]])]});}
            var Q68;
            {var subQ0=sQuery(id+"F0.wireOp",EDGE,"E35.trimOffspring");var subQ1=sQuery(id+"F0.wireOp",EDGE,"E13.5.0");var subQ2=makeQuery(id+"F0.imprint","INTERSECT",VERTEX,{"disambiguationData":[OD(1.0)],"derivedFrom":[subQ1,subQ0]});Q68=makeQuery(id+"F0.imprint","IMPRINT",FACE,{"disambiguationData":[TD([[makeQuery(id+"F0.imprint","IMPRINT",EDGE,{"disambiguationData":[TD([[subQ2,1.0]])],"derivedFrom":subQ1}),1.0]])]});}
            var Q69;
            {var subQ0=sQuery(id+"F0.wireOp",EDGE,"E34.trimOffspring");var subQ1=sQuery(id+"F0.wireOp",EDGE,"E13.6.0");var subQ2=makeQuery(id+"F0.imprint","INTERSECT",VERTEX,{"disambiguationData":[OD(0.0)],"derivedFrom":[subQ1,subQ0]});Q69=makeQuery(id+"F0.imprint","IMPRINT",FACE,{"disambiguationData":[TD([[makeQuery(id+"F0.imprint","IMPRINT",EDGE,{"disambiguationData":[TD([[subQ2,-1.0]])],"derivedFrom":subQ1}),-1.0]])]});}
            var Q70;
            {var subQ0=sQuery(id+"F0.wireOp",EDGE,"E34.trimOffspring");var subQ1=sQuery(id+"F0.wireOp",EDGE,"E13.6.0");var subQ2=makeQuery(id+"F0.imprint","INTERSECT",VERTEX,{"disambiguationData":[OD(0.0)],"derivedFrom":[subQ1,subQ0]});Q70=makeQuery(id+"F0.imprint","IMPRINT",FACE,{"disambiguationData":[TD([[makeQuery(id+"F0.imprint","IMPRINT",EDGE,{"disambiguationData":[TD([[subQ2,-1.0]])],"derivedFrom":subQ1}),1.0]])]});}
            var Q71;
            {var subQ0=sQuery(id+"F0.wireOp",EDGE,"E34.trimOffspring");var subQ1=sQuery(id+"F0.wireOp",EDGE,"E13.6.0");var subQ2=makeQuery(id+"F0.imprint","INTERSECT",VERTEX,{"disambiguationData":[OD(1.0)],"derivedFrom":[subQ1,subQ0]});Q71=makeQuery(id+"F0.imprint","IMPRINT",FACE,{"disambiguationData":[TD([[makeQuery(id+"F0.imprint","IMPRINT",EDGE,{"disambiguationData":[TD([[subQ2,1.0]])],"derivedFrom":subQ1}),1.0]])]});}
            var Q72;
            {var subQ0=sQuery(id+"F0.wireOp",EDGE,"E33.trimOffspring");var subQ1=sQuery(id+"F0.wireOp",EDGE,"E13.7.0");var subQ2=makeQuery(id+"F0.imprint","INTERSECT",VERTEX,{"disambiguationData":[OD(0.0)],"derivedFrom":[subQ1,subQ0]});Q72=makeQuery(id+"F0.imprint","IMPRINT",FACE,{"disambiguationData":[TD([[makeQuery(id+"F0.imprint","IMPRINT",EDGE,{"disambiguationData":[TD([[subQ2,-1.0]])],"derivedFrom":subQ1}),-1.0]])]});}
            var Q73;
            {var subQ0=sQuery(id+"F0.wireOp",EDGE,"E33.trimOffspring");var subQ1=sQuery(id+"F0.wireOp",EDGE,"E13.7.0");var subQ2=makeQuery(id+"F0.imprint","INTERSECT",VERTEX,{"disambiguationData":[OD(0.0)],"derivedFrom":[subQ1,subQ0]});Q73=makeQuery(id+"F0.imprint","IMPRINT",FACE,{"disambiguationData":[TD([[makeQuery(id+"F0.imprint","IMPRINT",EDGE,{"disambiguationData":[TD([[subQ2,-1.0]])],"derivedFrom":subQ1}),1.0]])]});}
            var Q74;
            {var subQ0=sQuery(id+"F0.wireOp",EDGE,"E33.trimOffspring");var subQ1=sQuery(id+"F0.wireOp",EDGE,"E13.7.0");var subQ2=makeQuery(id+"F0.imprint","INTERSECT",VERTEX,{"disambiguationData":[OD(1.0)],"derivedFrom":[subQ1,subQ0]});Q74=makeQuery(id+"F0.imprint","IMPRINT",FACE,{"disambiguationData":[TD([[makeQuery(id+"F0.imprint","IMPRINT",EDGE,{"disambiguationData":[TD([[subQ2,1.0]])],"derivedFrom":subQ1}),1.0]])]});}
            var Q75;
            {var subQ0=sQuery(id+"F0.wireOp",EDGE,"E32.trimOffspring");var subQ1=sQuery(id+"F0.wireOp",EDGE,"E13.8.0");var subQ2=makeQuery(id+"F0.imprint","INTERSECT",VERTEX,{"disambiguationData":[OD(0.0)],"derivedFrom":[subQ1,subQ0]});Q75=makeQuery(id+"F0.imprint","IMPRINT",FACE,{"disambiguationData":[TD([[makeQuery(id+"F0.imprint","IMPRINT",EDGE,{"disambiguationData":[TD([[subQ2,-1.0]])],"derivedFrom":subQ1}),-1.0]])]});}
            var Q76;
            {var subQ0=sQuery(id+"F0.wireOp",EDGE,"E32.trimOffspring");var subQ1=sQuery(id+"F0.wireOp",EDGE,"E13.8.0");var subQ2=makeQuery(id+"F0.imprint","INTERSECT",VERTEX,{"disambiguationData":[OD(0.0)],"derivedFrom":[subQ1,subQ0]});Q76=makeQuery(id+"F0.imprint","IMPRINT",FACE,{"disambiguationData":[TD([[makeQuery(id+"F0.imprint","IMPRINT",EDGE,{"disambiguationData":[TD([[subQ2,-1.0]])],"derivedFrom":subQ1}),1.0]])]});}
            var Q77;
            {var subQ0=sQuery(id+"F0.wireOp",EDGE,"E32.trimOffspring");var subQ1=sQuery(id+"F0.wireOp",EDGE,"E13.8.0");var subQ2=makeQuery(id+"F0.imprint","INTERSECT",VERTEX,{"disambiguationData":[OD(1.0)],"derivedFrom":[subQ1,subQ0]});Q77=makeQuery(id+"F0.imprint","IMPRINT",FACE,{"disambiguationData":[TD([[makeQuery(id+"F0.imprint","IMPRINT",EDGE,{"disambiguationData":[TD([[subQ2,1.0]])],"derivedFrom":subQ1}),1.0]])]});}
            var Q78;
            {var subQ0=sQuery(id+"F0.wireOp",EDGE,"E31.trimOffspring");var subQ1=sQuery(id+"F0.wireOp",EDGE,"E13.9.0");var subQ2=makeQuery(id+"F0.imprint","INTERSECT",VERTEX,{"disambiguationData":[OD(0.0)],"derivedFrom":[subQ1,subQ0]});Q78=makeQuery(id+"F0.imprint","IMPRINT",FACE,{"disambiguationData":[TD([[makeQuery(id+"F0.imprint","IMPRINT",EDGE,{"disambiguationData":[TD([[subQ2,-1.0]])],"derivedFrom":subQ1}),-1.0]])]});}
            var Q79;
            {var subQ0=sQuery(id+"F0.wireOp",EDGE,"E31.trimOffspring");var subQ1=sQuery(id+"F0.wireOp",EDGE,"E13.9.0");var subQ2=makeQuery(id+"F0.imprint","INTERSECT",VERTEX,{"disambiguationData":[OD(0.0)],"derivedFrom":[subQ1,subQ0]});Q79=makeQuery(id+"F0.imprint","IMPRINT",FACE,{"disambiguationData":[TD([[makeQuery(id+"F0.imprint","IMPRINT",EDGE,{"disambiguationData":[TD([[subQ2,-1.0]])],"derivedFrom":subQ1}),1.0]])]});}
            var Q80;
            {var subQ0=sQuery(id+"F0.wireOp",EDGE,"E31.trimOffspring");var subQ1=sQuery(id+"F0.wireOp",EDGE,"E13.9.0");var subQ2=makeQuery(id+"F0.imprint","INTERSECT",VERTEX,{"disambiguationData":[OD(1.0)],"derivedFrom":[subQ1,subQ0]});Q80=makeQuery(id+"F0.imprint","IMPRINT",FACE,{"disambiguationData":[TD([[makeQuery(id+"F0.imprint","IMPRINT",EDGE,{"disambiguationData":[TD([[subQ2,1.0]])],"derivedFrom":subQ1}),1.0]])]});}
            var Q81;
            {var subQ0=sQuery(id+"F0.wireOp",EDGE,"E30.trimOffspring");var subQ1=sQuery(id+"F0.wireOp",EDGE,"E13.10.0");var subQ2=makeQuery(id+"F0.imprint","INTERSECT",VERTEX,{"disambiguationData":[OD(0.0)],"derivedFrom":[subQ1,subQ0]});Q81=makeQuery(id+"F0.imprint","IMPRINT",FACE,{"disambiguationData":[TD([[makeQuery(id+"F0.imprint","IMPRINT",EDGE,{"disambiguationData":[TD([[subQ2,-1.0]])],"derivedFrom":subQ1}),-1.0]])]});}
            var Q82;
            {var subQ0=sQuery(id+"F0.wireOp",EDGE,"E30.trimOffspring");var subQ1=sQuery(id+"F0.wireOp",EDGE,"E13.10.0");var subQ2=makeQuery(id+"F0.imprint","INTERSECT",VERTEX,{"disambiguationData":[OD(0.0)],"derivedFrom":[subQ1,subQ0]});Q82=makeQuery(id+"F0.imprint","IMPRINT",FACE,{"disambiguationData":[TD([[makeQuery(id+"F0.imprint","IMPRINT",EDGE,{"disambiguationData":[TD([[subQ2,-1.0]])],"derivedFrom":subQ1}),1.0]])]});}
            var Q83;
            {var subQ0=sQuery(id+"F0.wireOp",EDGE,"E30.trimOffspring");var subQ1=sQuery(id+"F0.wireOp",EDGE,"E13.10.0");var subQ2=makeQuery(id+"F0.imprint","INTERSECT",VERTEX,{"disambiguationData":[OD(1.0)],"derivedFrom":[subQ1,subQ0]});Q83=makeQuery(id+"F0.imprint","IMPRINT",FACE,{"disambiguationData":[TD([[makeQuery(id+"F0.imprint","IMPRINT",EDGE,{"disambiguationData":[TD([[subQ2,1.0]])],"derivedFrom":subQ1}),1.0]])]});}
            var Q84;
            {var subQ0=sQuery(id+"F0.wireOp",EDGE,"E29.trimOffspring");var subQ1=sQuery(id+"F0.wireOp",EDGE,"E13.11.0");var subQ2=makeQuery(id+"F0.imprint","INTERSECT",VERTEX,{"disambiguationData":[OD(0.0)],"derivedFrom":[subQ1,subQ0]});Q84=makeQuery(id+"F0.imprint","IMPRINT",FACE,{"disambiguationData":[TD([[makeQuery(id+"F0.imprint","IMPRINT",EDGE,{"disambiguationData":[TD([[subQ2,-1.0]])],"derivedFrom":subQ1}),-1.0]])]});}
            var Q85;
            {var subQ0=sQuery(id+"F0.wireOp",EDGE,"E29.trimOffspring");var subQ1=sQuery(id+"F0.wireOp",EDGE,"E13.11.0");var subQ2=makeQuery(id+"F0.imprint","INTERSECT",VERTEX,{"disambiguationData":[OD(0.0)],"derivedFrom":[subQ1,subQ0]});Q85=makeQuery(id+"F0.imprint","IMPRINT",FACE,{"disambiguationData":[TD([[makeQuery(id+"F0.imprint","IMPRINT",EDGE,{"disambiguationData":[TD([[subQ2,-1.0]])],"derivedFrom":subQ1}),1.0]])]});}
            var Q86;
            {var subQ0=sQuery(id+"F0.wireOp",EDGE,"E29.trimOffspring");var subQ1=sQuery(id+"F0.wireOp",EDGE,"E13.11.0");var subQ2=makeQuery(id+"F0.imprint","INTERSECT",VERTEX,{"disambiguationData":[OD(1.0)],"derivedFrom":[subQ1,subQ0]});Q86=makeQuery(id+"F0.imprint","IMPRINT",FACE,{"disambiguationData":[TD([[makeQuery(id+"F0.imprint","IMPRINT",EDGE,{"disambiguationData":[TD([[subQ2,1.0]])],"derivedFrom":subQ1}),1.0]])]});}
            var Q87;
            {var subQ0=sQuery(id+"F0.wireOp",EDGE,"E28.trimOffspring");var subQ1=sQuery(id+"F0.wireOp",EDGE,"E13.12.0");var subQ2=makeQuery(id+"F0.imprint","INTERSECT",VERTEX,{"disambiguationData":[OD(0.0)],"derivedFrom":[subQ1,subQ0]});Q87=makeQuery(id+"F0.imprint","IMPRINT",FACE,{"disambiguationData":[TD([[makeQuery(id+"F0.imprint","IMPRINT",EDGE,{"disambiguationData":[TD([[subQ2,-1.0]])],"derivedFrom":subQ1}),-1.0]])]});}
            var Q88;
            {var subQ0=sQuery(id+"F0.wireOp",EDGE,"E28.trimOffspring");var subQ1=sQuery(id+"F0.wireOp",EDGE,"E13.12.0");var subQ2=makeQuery(id+"F0.imprint","INTERSECT",VERTEX,{"disambiguationData":[OD(0.0)],"derivedFrom":[subQ1,subQ0]});Q88=makeQuery(id+"F0.imprint","IMPRINT",FACE,{"disambiguationData":[TD([[makeQuery(id+"F0.imprint","IMPRINT",EDGE,{"disambiguationData":[TD([[subQ2,-1.0]])],"derivedFrom":subQ1}),1.0]])]});}
            var Q89;
            {var subQ0=sQuery(id+"F0.wireOp",EDGE,"E28.trimOffspring");var subQ1=sQuery(id+"F0.wireOp",EDGE,"E13.12.0");var subQ2=makeQuery(id+"F0.imprint","INTERSECT",VERTEX,{"disambiguationData":[OD(1.0)],"derivedFrom":[subQ1,subQ0]});Q89=makeQuery(id+"F0.imprint","IMPRINT",FACE,{"disambiguationData":[TD([[makeQuery(id+"F0.imprint","IMPRINT",EDGE,{"disambiguationData":[TD([[subQ2,1.0]])],"derivedFrom":subQ1}),1.0]])]});}
            var Q90;
            {var subQ0=sQuery(id+"F0.wireOp",EDGE,"E27.trimOffspring");var subQ1=sQuery(id+"F0.wireOp",EDGE,"E13.13.0");var subQ2=makeQuery(id+"F0.imprint","INTERSECT",VERTEX,{"disambiguationData":[OD(0.0)],"derivedFrom":[subQ1,subQ0]});Q90=makeQuery(id+"F0.imprint","IMPRINT",FACE,{"disambiguationData":[TD([[makeQuery(id+"F0.imprint","IMPRINT",EDGE,{"disambiguationData":[TD([[subQ2,-1.0]])],"derivedFrom":subQ1}),-1.0]])]});}
            var Q91;
            {var subQ0=sQuery(id+"F0.wireOp",EDGE,"E27.trimOffspring");var subQ1=sQuery(id+"F0.wireOp",EDGE,"E13.13.0");var subQ2=makeQuery(id+"F0.imprint","INTERSECT",VERTEX,{"disambiguationData":[OD(0.0)],"derivedFrom":[subQ1,subQ0]});Q91=makeQuery(id+"F0.imprint","IMPRINT",FACE,{"disambiguationData":[TD([[makeQuery(id+"F0.imprint","IMPRINT",EDGE,{"disambiguationData":[TD([[subQ2,-1.0]])],"derivedFrom":subQ1}),1.0]])]});}
            var Q92;
            {var subQ0=sQuery(id+"F0.wireOp",EDGE,"E27.trimOffspring");var subQ1=sQuery(id+"F0.wireOp",EDGE,"E13.13.0");var subQ2=makeQuery(id+"F0.imprint","INTERSECT",VERTEX,{"disambiguationData":[OD(1.0)],"derivedFrom":[subQ1,subQ0]});Q92=makeQuery(id+"F0.imprint","IMPRINT",FACE,{"disambiguationData":[TD([[makeQuery(id+"F0.imprint","IMPRINT",EDGE,{"disambiguationData":[TD([[subQ2,1.0]])],"derivedFrom":subQ1}),1.0]])]});}
            var Q93;
            {var subQ0=sQuery(id+"F0.wireOp",EDGE,"E26.trimOffspring");var subQ1=sQuery(id+"F0.wireOp",EDGE,"E13.14.0");var subQ2=makeQuery(id+"F0.imprint","INTERSECT",VERTEX,{"disambiguationData":[OD(0.0)],"derivedFrom":[subQ1,subQ0]});Q93=makeQuery(id+"F0.imprint","IMPRINT",FACE,{"disambiguationData":[TD([[makeQuery(id+"F0.imprint","IMPRINT",EDGE,{"disambiguationData":[TD([[subQ2,-1.0]])],"derivedFrom":subQ1}),-1.0]])]});}
            var Q94;
            {var subQ0=sQuery(id+"F0.wireOp",EDGE,"E26.trimOffspring");var subQ1=sQuery(id+"F0.wireOp",EDGE,"E13.14.0");var subQ2=makeQuery(id+"F0.imprint","INTERSECT",VERTEX,{"disambiguationData":[OD(0.0)],"derivedFrom":[subQ1,subQ0]});Q94=makeQuery(id+"F0.imprint","IMPRINT",FACE,{"disambiguationData":[TD([[makeQuery(id+"F0.imprint","IMPRINT",EDGE,{"disambiguationData":[TD([[subQ2,-1.0]])],"derivedFrom":subQ1}),1.0]])]});}
            var Q95;
            {var subQ0=sQuery(id+"F0.wireOp",EDGE,"E26.trimOffspring");var subQ1=sQuery(id+"F0.wireOp",EDGE,"E13.14.0");var subQ2=makeQuery(id+"F0.imprint","INTERSECT",VERTEX,{"disambiguationData":[OD(1.0)],"derivedFrom":[subQ1,subQ0]});Q95=makeQuery(id+"F0.imprint","IMPRINT",FACE,{"disambiguationData":[TD([[makeQuery(id+"F0.imprint","IMPRINT",EDGE,{"disambiguationData":[TD([[subQ2,1.0]])],"derivedFrom":subQ1}),1.0]])]});}
            var Q96;
            {var subQ0=sQuery(id+"F0.wireOp",EDGE,"E25.trimOffspring");var subQ1=sQuery(id+"F0.wireOp",EDGE,"E13.15.0");var subQ2=makeQuery(id+"F0.imprint","INTERSECT",VERTEX,{"disambiguationData":[OD(0.0)],"derivedFrom":[subQ1,subQ0]});Q96=makeQuery(id+"F0.imprint","IMPRINT",FACE,{"disambiguationData":[TD([[makeQuery(id+"F0.imprint","IMPRINT",EDGE,{"disambiguationData":[TD([[subQ2,-1.0]])],"derivedFrom":subQ1}),-1.0]])]});}
            var Q97;
            {var subQ0=sQuery(id+"F0.wireOp",EDGE,"E25.trimOffspring");var subQ1=sQuery(id+"F0.wireOp",EDGE,"E13.15.0");var subQ2=makeQuery(id+"F0.imprint","INTERSECT",VERTEX,{"disambiguationData":[OD(0.0)],"derivedFrom":[subQ1,subQ0]});Q97=makeQuery(id+"F0.imprint","IMPRINT",FACE,{"disambiguationData":[TD([[makeQuery(id+"F0.imprint","IMPRINT",EDGE,{"disambiguationData":[TD([[subQ2,-1.0]])],"derivedFrom":subQ1}),1.0]])]});}
            var Q98;
            {var subQ0=sQuery(id+"F0.wireOp",EDGE,"E25.trimOffspring");var subQ1=sQuery(id+"F0.wireOp",EDGE,"E13.15.0");var subQ2=makeQuery(id+"F0.imprint","INTERSECT",VERTEX,{"disambiguationData":[OD(1.0)],"derivedFrom":[subQ1,subQ0]});Q98=makeQuery(id+"F0.imprint","IMPRINT",FACE,{"disambiguationData":[TD([[makeQuery(id+"F0.imprint","IMPRINT",EDGE,{"disambiguationData":[TD([[subQ2,1.0]])],"derivedFrom":subQ1}),1.0]])]});}
            var Q99;
            {var subQ0=sQuery(id+"F0.wireOp",EDGE,"E24.trimOffspring");var subQ1=sQuery(id+"F0.wireOp",EDGE,"E13.16.0");var subQ2=makeQuery(id+"F0.imprint","INTERSECT",VERTEX,{"disambiguationData":[OD(0.0)],"derivedFrom":[subQ1,subQ0]});Q99=makeQuery(id+"F0.imprint","IMPRINT",FACE,{"disambiguationData":[TD([[makeQuery(id+"F0.imprint","IMPRINT",EDGE,{"disambiguationData":[TD([[subQ2,-1.0]])],"derivedFrom":subQ1}),-1.0]])]});}
            var Q100;
            {var subQ0=sQuery(id+"F0.wireOp",EDGE,"E24.trimOffspring");var subQ1=sQuery(id+"F0.wireOp",EDGE,"E13.16.0");var subQ2=makeQuery(id+"F0.imprint","INTERSECT",VERTEX,{"disambiguationData":[OD(0.0)],"derivedFrom":[subQ1,subQ0]});Q100=makeQuery(id+"F0.imprint","IMPRINT",FACE,{"disambiguationData":[TD([[makeQuery(id+"F0.imprint","IMPRINT",EDGE,{"disambiguationData":[TD([[subQ2,-1.0]])],"derivedFrom":subQ1}),1.0]])]});}
            var Q101;
            {var subQ0=sQuery(id+"F0.wireOp",EDGE,"E24.trimOffspring");var subQ1=sQuery(id+"F0.wireOp",EDGE,"E13.16.0");var subQ2=makeQuery(id+"F0.imprint","INTERSECT",VERTEX,{"disambiguationData":[OD(1.0)],"derivedFrom":[subQ1,subQ0]});Q101=makeQuery(id+"F0.imprint","IMPRINT",FACE,{"disambiguationData":[TD([[makeQuery(id+"F0.imprint","IMPRINT",EDGE,{"disambiguationData":[TD([[subQ2,1.0]])],"derivedFrom":subQ1}),1.0]])]});}
            var Q102;
            {var subQ0=sQuery(id+"F0.wireOp",EDGE,"E23.trimOffspring");var subQ1=sQuery(id+"F0.wireOp",EDGE,"E13.17.0");var subQ2=makeQuery(id+"F0.imprint","INTERSECT",VERTEX,{"disambiguationData":[OD(0.0)],"derivedFrom":[subQ1,subQ0]});Q102=makeQuery(id+"F0.imprint","IMPRINT",FACE,{"disambiguationData":[TD([[makeQuery(id+"F0.imprint","IMPRINT",EDGE,{"disambiguationData":[TD([[subQ2,-1.0]])],"derivedFrom":subQ1}),-1.0]])]});}
            var Q103;
            {var subQ0=sQuery(id+"F0.wireOp",EDGE,"E23.trimOffspring");var subQ1=sQuery(id+"F0.wireOp",EDGE,"E13.17.0");var subQ2=makeQuery(id+"F0.imprint","INTERSECT",VERTEX,{"disambiguationData":[OD(0.0)],"derivedFrom":[subQ1,subQ0]});Q103=makeQuery(id+"F0.imprint","IMPRINT",FACE,{"disambiguationData":[TD([[makeQuery(id+"F0.imprint","IMPRINT",EDGE,{"disambiguationData":[TD([[subQ2,-1.0]])],"derivedFrom":subQ1}),1.0]])]});}
            var Q104;
            {var subQ0=sQuery(id+"F0.wireOp",EDGE,"E23.trimOffspring");var subQ1=sQuery(id+"F0.wireOp",EDGE,"E13.17.0");var subQ2=makeQuery(id+"F0.imprint","INTERSECT",VERTEX,{"disambiguationData":[OD(1.0)],"derivedFrom":[subQ1,subQ0]});Q104=makeQuery(id+"F0.imprint","IMPRINT",FACE,{"disambiguationData":[TD([[makeQuery(id+"F0.imprint","IMPRINT",EDGE,{"disambiguationData":[TD([[subQ2,1.0]])],"derivedFrom":subQ1}),1.0]])]});}
            var Q105;
            {var subQ0=sQuery(id+"F0.wireOp",EDGE,"E21.trimOffspring");var subQ1=sQuery(id+"F0.wireOp",EDGE,"E13.18.0");var subQ2=makeQuery(id+"F0.imprint","INTERSECT",VERTEX,{"disambiguationData":[OD(0.0)],"derivedFrom":[subQ1,subQ0]});Q105=makeQuery(id+"F0.imprint","IMPRINT",FACE,{"disambiguationData":[TD([[makeQuery(id+"F0.imprint","IMPRINT",EDGE,{"disambiguationData":[TD([[subQ2,-1.0]])],"derivedFrom":subQ1}),-1.0]])]});}
            var Q106;
            {var subQ0=sQuery(id+"F0.wireOp",EDGE,"E21.trimOffspring");var subQ1=sQuery(id+"F0.wireOp",EDGE,"E13.18.0");var subQ2=makeQuery(id+"F0.imprint","INTERSECT",VERTEX,{"disambiguationData":[OD(0.0)],"derivedFrom":[subQ1,subQ0]});Q106=makeQuery(id+"F0.imprint","IMPRINT",FACE,{"disambiguationData":[TD([[makeQuery(id+"F0.imprint","IMPRINT",EDGE,{"disambiguationData":[TD([[subQ2,-1.0]])],"derivedFrom":subQ1}),1.0]])]});}
            var Q107;
            {var subQ0=sQuery(id+"F0.wireOp",EDGE,"E21.trimOffspring");var subQ1=sQuery(id+"F0.wireOp",EDGE,"E13.18.0");var subQ2=makeQuery(id+"F0.imprint","INTERSECT",VERTEX,{"disambiguationData":[OD(1.0)],"derivedFrom":[subQ1,subQ0]});Q107=makeQuery(id+"F0.imprint","IMPRINT",FACE,{"disambiguationData":[TD([[makeQuery(id+"F0.imprint","IMPRINT",EDGE,{"disambiguationData":[TD([[subQ2,1.0]])],"derivedFrom":subQ1}),1.0]])]});}
            var Q108;
            {var subQ0=sQuery(id+"F0.wireOp",EDGE,"E22.trimOffspring");var subQ1=sQuery(id+"F0.wireOp",EDGE,"E13.19.0");var subQ2=makeQuery(id+"F0.imprint","INTERSECT",VERTEX,{"disambiguationData":[OD(0.0)],"derivedFrom":[subQ1,subQ0]});Q108=makeQuery(id+"F0.imprint","IMPRINT",FACE,{"disambiguationData":[TD([[makeQuery(id+"F0.imprint","IMPRINT",EDGE,{"disambiguationData":[TD([[subQ2,-1.0]])],"derivedFrom":subQ1}),-1.0]])]});}
            var Q109;
            {var subQ0=sQuery(id+"F0.wireOp",EDGE,"E22.trimOffspring");var subQ1=sQuery(id+"F0.wireOp",EDGE,"E13.19.0");var subQ2=makeQuery(id+"F0.imprint","INTERSECT",VERTEX,{"disambiguationData":[OD(0.0)],"derivedFrom":[subQ1,subQ0]});Q109=makeQuery(id+"F0.imprint","IMPRINT",FACE,{"disambiguationData":[TD([[makeQuery(id+"F0.imprint","IMPRINT",EDGE,{"disambiguationData":[TD([[subQ2,-1.0]])],"derivedFrom":subQ1}),1.0]])]});}
            var Q110;
            {var subQ0=sQuery(id+"F0.wireOp",EDGE,"E22.trimOffspring");var subQ1=sQuery(id+"F0.wireOp",EDGE,"E13.19.0");var subQ2=makeQuery(id+"F0.imprint","INTERSECT",VERTEX,{"disambiguationData":[OD(1.0)],"derivedFrom":[subQ1,subQ0]});Q110=makeQuery(id+"F0.imprint","IMPRINT",FACE,{"disambiguationData":[TD([[makeQuery(id+"F0.imprint","IMPRINT",EDGE,{"disambiguationData":[TD([[subQ2,1.0]])],"derivedFrom":subQ1}),1.0]])]});}
            var Q111;
            {var subQ0=sQuery(id+"F0.wireOp",EDGE,"E20.trimOffspring");var subQ1=sQuery(id+"F0.wireOp",EDGE,"E13.20.0");var subQ2=makeQuery(id+"F0.imprint","INTERSECT",VERTEX,{"disambiguationData":[OD(0.0)],"derivedFrom":[subQ1,subQ0]});Q111=makeQuery(id+"F0.imprint","IMPRINT",FACE,{"disambiguationData":[TD([[makeQuery(id+"F0.imprint","IMPRINT",EDGE,{"disambiguationData":[TD([[subQ2,-1.0]])],"derivedFrom":subQ1}),-1.0]])]});}
            var Q112;
            {var subQ0=sQuery(id+"F0.wireOp",EDGE,"E20.trimOffspring");var subQ1=sQuery(id+"F0.wireOp",EDGE,"E13.20.0");var subQ2=makeQuery(id+"F0.imprint","INTERSECT",VERTEX,{"disambiguationData":[OD(0.0)],"derivedFrom":[subQ1,subQ0]});Q112=makeQuery(id+"F0.imprint","IMPRINT",FACE,{"disambiguationData":[TD([[makeQuery(id+"F0.imprint","IMPRINT",EDGE,{"disambiguationData":[TD([[subQ2,-1.0]])],"derivedFrom":subQ1}),1.0]])]});}
            var Q113;
            {var subQ0=sQuery(id+"F0.wireOp",EDGE,"E20.trimOffspring");var subQ1=sQuery(id+"F0.wireOp",EDGE,"E13.20.0");var subQ2=makeQuery(id+"F0.imprint","INTERSECT",VERTEX,{"disambiguationData":[OD(1.0)],"derivedFrom":[subQ1,subQ0]});Q113=makeQuery(id+"F0.imprint","IMPRINT",FACE,{"disambiguationData":[TD([[makeQuery(id+"F0.imprint","IMPRINT",EDGE,{"disambiguationData":[TD([[subQ2,1.0]])],"derivedFrom":subQ1}),1.0]])]});}
            var Q114;
            {var subQ0=sQuery(id+"F0.wireOp",EDGE,"E19.trimOffspring");var subQ1=sQuery(id+"F0.wireOp",EDGE,"E13.21.0");var subQ2=makeQuery(id+"F0.imprint","INTERSECT",VERTEX,{"disambiguationData":[OD(0.0)],"derivedFrom":[subQ1,subQ0]});Q114=makeQuery(id+"F0.imprint","IMPRINT",FACE,{"disambiguationData":[TD([[makeQuery(id+"F0.imprint","IMPRINT",EDGE,{"disambiguationData":[TD([[subQ2,-1.0]])],"derivedFrom":subQ1}),-1.0]])]});}
            var Q115;
            {var subQ0=sQuery(id+"F0.wireOp",EDGE,"E19.trimOffspring");var subQ1=sQuery(id+"F0.wireOp",EDGE,"E13.21.0");var subQ2=makeQuery(id+"F0.imprint","INTERSECT",VERTEX,{"disambiguationData":[OD(0.0)],"derivedFrom":[subQ1,subQ0]});Q115=makeQuery(id+"F0.imprint","IMPRINT",FACE,{"disambiguationData":[TD([[makeQuery(id+"F0.imprint","IMPRINT",EDGE,{"disambiguationData":[TD([[subQ2,-1.0]])],"derivedFrom":subQ1}),1.0]])]});}
            var Q116;
            {var subQ0=sQuery(id+"F0.wireOp",EDGE,"E19.trimOffspring");var subQ1=sQuery(id+"F0.wireOp",EDGE,"E13.21.0");var subQ2=makeQuery(id+"F0.imprint","INTERSECT",VERTEX,{"disambiguationData":[OD(1.0)],"derivedFrom":[subQ1,subQ0]});Q116=makeQuery(id+"F0.imprint","IMPRINT",FACE,{"disambiguationData":[TD([[makeQuery(id+"F0.imprint","IMPRINT",EDGE,{"disambiguationData":[TD([[subQ2,1.0]])],"derivedFrom":subQ1}),1.0]])]});}
            var Q117;
            {var subQ0=sQuery(id+"F0.wireOp",EDGE,"E18.trimOffspring");var subQ1=sQuery(id+"F0.wireOp",EDGE,"E13.22.0");var subQ2=makeQuery(id+"F0.imprint","INTERSECT",VERTEX,{"disambiguationData":[OD(0.0)],"derivedFrom":[subQ1,subQ0]});Q117=makeQuery(id+"F0.imprint","IMPRINT",FACE,{"disambiguationData":[TD([[makeQuery(id+"F0.imprint","IMPRINT",EDGE,{"disambiguationData":[TD([[subQ2,-1.0]])],"derivedFrom":subQ1}),-1.0]])]});}
            var Q118;
            {var subQ0=sQuery(id+"F0.wireOp",EDGE,"E18.trimOffspring");var subQ1=sQuery(id+"F0.wireOp",EDGE,"E13.22.0");var subQ2=makeQuery(id+"F0.imprint","INTERSECT",VERTEX,{"disambiguationData":[OD(0.0)],"derivedFrom":[subQ1,subQ0]});Q118=makeQuery(id+"F0.imprint","IMPRINT",FACE,{"disambiguationData":[TD([[makeQuery(id+"F0.imprint","IMPRINT",EDGE,{"disambiguationData":[TD([[subQ2,-1.0]])],"derivedFrom":subQ1}),1.0]])]});}
            var Q119;
            {var subQ0=sQuery(id+"F0.wireOp",EDGE,"E18.trimOffspring");var subQ1=sQuery(id+"F0.wireOp",EDGE,"E13.22.0");var subQ2=makeQuery(id+"F0.imprint","INTERSECT",VERTEX,{"disambiguationData":[OD(1.0)],"derivedFrom":[subQ1,subQ0]});Q119=makeQuery(id+"F0.imprint","IMPRINT",FACE,{"disambiguationData":[TD([[makeQuery(id+"F0.imprint","IMPRINT",EDGE,{"disambiguationData":[TD([[subQ2,1.0]])],"derivedFrom":subQ1}),1.0]])]});}
            var Q120;
            {var subQ0=sQuery(id+"F0.wireOp",EDGE,"E12");var subQ1=sQuery(id+"F0.wireOp",EDGE,"E2");var subQ2=makeQuery(id+"F0.imprint","INTERSECT",VERTEX,{"disambiguationData":[OD(0.0)],"derivedFrom":[subQ1,subQ0]});Q120=makeQuery(id+"F0.imprint","IMPRINT",FACE,{"disambiguationData":[TD([[makeQuery(id+"F0.imprint","IMPRINT",EDGE,{"disambiguationData":[TD([[subQ2,1.0]])],"derivedFrom":subQ1}),-1.0]])]});}
            var Q121;
            {var subQ0=sQuery(id+"F0.wireOp",EDGE,"E11");var subQ1=sQuery(id+"F0.wireOp",EDGE,"E6.MirrorCS");var subQ2=makeQuery(id+"F0.imprint","INTERSECT",VERTEX,{"disambiguationData":[OD(0.0)],"derivedFrom":[subQ1,subQ0]});Q121=makeQuery(id+"F0.imprint","IMPRINT",FACE,{"disambiguationData":[TD([[makeQuery(id+"F0.imprint","IMPRINT",EDGE,{"disambiguationData":[TD([[subQ2,1.0]])],"derivedFrom":subQ1}),1.0]])]});}
            var Q122;
            {var subQ0=sQuery(id+"F0.wireOp",EDGE,"E13.1.1");var subQ1=sQuery(id+"F0.wireOp",EDGE,"E13.1.0");var subQ2=makeQuery(id+"F0.imprint","INTERSECT",VERTEX,{"disambiguationData":[OD(0.0)],"derivedFrom":[subQ1,subQ0]});Q122=makeQuery(id+"F0.imprint","IMPRINT",FACE,{"disambiguationData":[TD([[makeQuery(id+"F0.imprint","IMPRINT",EDGE,{"disambiguationData":[TD([[subQ2,1.0]])],"derivedFrom":subQ1}),1.0]])]});}
            var Q123;
            {var subQ0=sQuery(id+"F0.wireOp",EDGE,"E13.1.10");var subQ1=sQuery(id+"F0.wireOp",EDGE,"E13.1.9");var subQ2=makeQuery(id+"F0.imprint","INTERSECT",VERTEX,{"disambiguationData":[OD(0.0)],"derivedFrom":[subQ1,subQ0]});Q123=makeQuery(id+"F0.imprint","IMPRINT",FACE,{"disambiguationData":[TD([[makeQuery(id+"F0.imprint","IMPRINT",EDGE,{"disambiguationData":[TD([[subQ2,1.0]])],"derivedFrom":subQ1}),-1.0]])]});}
            var Q124;
            {var subQ0=sQuery(id+"F0.wireOp",EDGE,"E13.2.1");var subQ1=sQuery(id+"F0.wireOp",EDGE,"E13.2.0");var subQ2=makeQuery(id+"F0.imprint","INTERSECT",VERTEX,{"disambiguationData":[OD(0.0)],"derivedFrom":[subQ1,subQ0]});Q124=makeQuery(id+"F0.imprint","IMPRINT",FACE,{"disambiguationData":[TD([[makeQuery(id+"F0.imprint","IMPRINT",EDGE,{"disambiguationData":[TD([[subQ2,1.0]])],"derivedFrom":subQ1}),1.0]])]});}
            var Q125;
            {var subQ0=sQuery(id+"F0.wireOp",EDGE,"E13.2.10");var subQ1=sQuery(id+"F0.wireOp",EDGE,"E13.2.9");var subQ2=makeQuery(id+"F0.imprint","INTERSECT",VERTEX,{"disambiguationData":[OD(0.0)],"derivedFrom":[subQ1,subQ0]});Q125=makeQuery(id+"F0.imprint","IMPRINT",FACE,{"disambiguationData":[TD([[makeQuery(id+"F0.imprint","IMPRINT",EDGE,{"disambiguationData":[TD([[subQ2,1.0]])],"derivedFrom":subQ1}),-1.0]])]});}
            var Q126;
            {var subQ0=sQuery(id+"F0.wireOp",EDGE,"E13.3.1");var subQ1=sQuery(id+"F0.wireOp",EDGE,"E13.3.0");var subQ2=makeQuery(id+"F0.imprint","INTERSECT",VERTEX,{"disambiguationData":[OD(0.0)],"derivedFrom":[subQ1,subQ0]});Q126=makeQuery(id+"F0.imprint","IMPRINT",FACE,{"disambiguationData":[TD([[makeQuery(id+"F0.imprint","IMPRINT",EDGE,{"disambiguationData":[TD([[subQ2,1.0]])],"derivedFrom":subQ1}),1.0]])]});}
            var Q127;
            {var subQ0=sQuery(id+"F0.wireOp",EDGE,"E13.3.10");var subQ1=sQuery(id+"F0.wireOp",EDGE,"E13.3.9");var subQ2=makeQuery(id+"F0.imprint","INTERSECT",VERTEX,{"disambiguationData":[OD(0.0)],"derivedFrom":[subQ1,subQ0]});Q127=makeQuery(id+"F0.imprint","IMPRINT",FACE,{"disambiguationData":[TD([[makeQuery(id+"F0.imprint","IMPRINT",EDGE,{"disambiguationData":[TD([[subQ2,1.0]])],"derivedFrom":subQ1}),-1.0]])]});}
            var Q128;
            {var subQ0=sQuery(id+"F0.wireOp",EDGE,"E13.4.1");var subQ1=sQuery(id+"F0.wireOp",EDGE,"E13.4.0");var subQ2=makeQuery(id+"F0.imprint","INTERSECT",VERTEX,{"disambiguationData":[OD(0.0)],"derivedFrom":[subQ1,subQ0]});Q128=makeQuery(id+"F0.imprint","IMPRINT",FACE,{"disambiguationData":[TD([[makeQuery(id+"F0.imprint","IMPRINT",EDGE,{"disambiguationData":[TD([[subQ2,1.0]])],"derivedFrom":subQ1}),1.0]])]});}
            var Q129;
            {var subQ0=sQuery(id+"F0.wireOp",EDGE,"E13.4.10");var subQ1=sQuery(id+"F0.wireOp",EDGE,"E13.4.9");var subQ2=makeQuery(id+"F0.imprint","INTERSECT",VERTEX,{"disambiguationData":[OD(0.0)],"derivedFrom":[subQ1,subQ0]});Q129=makeQuery(id+"F0.imprint","IMPRINT",FACE,{"disambiguationData":[TD([[makeQuery(id+"F0.imprint","IMPRINT",EDGE,{"disambiguationData":[TD([[subQ2,1.0]])],"derivedFrom":subQ1}),-1.0]])]});}
            var Q130;
            {var subQ0=sQuery(id+"F0.wireOp",EDGE,"E13.5.1");var subQ1=sQuery(id+"F0.wireOp",EDGE,"E13.5.0");var subQ2=makeQuery(id+"F0.imprint","INTERSECT",VERTEX,{"disambiguationData":[OD(0.0)],"derivedFrom":[subQ1,subQ0]});Q130=makeQuery(id+"F0.imprint","IMPRINT",FACE,{"disambiguationData":[TD([[makeQuery(id+"F0.imprint","IMPRINT",EDGE,{"disambiguationData":[TD([[subQ2,1.0]])],"derivedFrom":subQ1}),1.0]])]});}
            var Q131;
            {var subQ0=sQuery(id+"F0.wireOp",EDGE,"E13.5.10");var subQ1=sQuery(id+"F0.wireOp",EDGE,"E13.5.9");var subQ2=makeQuery(id+"F0.imprint","INTERSECT",VERTEX,{"disambiguationData":[OD(0.0)],"derivedFrom":[subQ1,subQ0]});Q131=makeQuery(id+"F0.imprint","IMPRINT",FACE,{"disambiguationData":[TD([[makeQuery(id+"F0.imprint","IMPRINT",EDGE,{"disambiguationData":[TD([[subQ2,1.0]])],"derivedFrom":subQ1}),-1.0]])]});}
            var Q132;
            {var subQ0=sQuery(id+"F0.wireOp",EDGE,"E13.6.1");var subQ1=sQuery(id+"F0.wireOp",EDGE,"E13.6.0");var subQ2=makeQuery(id+"F0.imprint","INTERSECT",VERTEX,{"disambiguationData":[OD(0.0)],"derivedFrom":[subQ1,subQ0]});Q132=makeQuery(id+"F0.imprint","IMPRINT",FACE,{"disambiguationData":[TD([[makeQuery(id+"F0.imprint","IMPRINT",EDGE,{"disambiguationData":[TD([[subQ2,1.0]])],"derivedFrom":subQ1}),1.0]])]});}
            var Q133;
            {var subQ0=sQuery(id+"F0.wireOp",EDGE,"E13.6.10");var subQ1=sQuery(id+"F0.wireOp",EDGE,"E13.6.9");var subQ2=makeQuery(id+"F0.imprint","INTERSECT",VERTEX,{"disambiguationData":[OD(0.0)],"derivedFrom":[subQ1,subQ0]});Q133=makeQuery(id+"F0.imprint","IMPRINT",FACE,{"disambiguationData":[TD([[makeQuery(id+"F0.imprint","IMPRINT",EDGE,{"disambiguationData":[TD([[subQ2,1.0]])],"derivedFrom":subQ1}),-1.0]])]});}
            var Q134;
            {var subQ0=sQuery(id+"F0.wireOp",EDGE,"E13.7.1");var subQ1=sQuery(id+"F0.wireOp",EDGE,"E13.7.0");var subQ2=makeQuery(id+"F0.imprint","INTERSECT",VERTEX,{"disambiguationData":[OD(0.0)],"derivedFrom":[subQ1,subQ0]});Q134=makeQuery(id+"F0.imprint","IMPRINT",FACE,{"disambiguationData":[TD([[makeQuery(id+"F0.imprint","IMPRINT",EDGE,{"disambiguationData":[TD([[subQ2,1.0]])],"derivedFrom":subQ1}),1.0]])]});}
            var Q135;
            {var subQ0=sQuery(id+"F0.wireOp",EDGE,"E13.7.10");var subQ1=sQuery(id+"F0.wireOp",EDGE,"E13.7.9");var subQ2=makeQuery(id+"F0.imprint","INTERSECT",VERTEX,{"disambiguationData":[OD(0.0)],"derivedFrom":[subQ1,subQ0]});Q135=makeQuery(id+"F0.imprint","IMPRINT",FACE,{"disambiguationData":[TD([[makeQuery(id+"F0.imprint","IMPRINT",EDGE,{"disambiguationData":[TD([[subQ2,1.0]])],"derivedFrom":subQ1}),-1.0]])]});}
            var Q136;
            {var subQ0=sQuery(id+"F0.wireOp",EDGE,"E13.8.1");var subQ1=sQuery(id+"F0.wireOp",EDGE,"E13.8.0");var subQ2=makeQuery(id+"F0.imprint","INTERSECT",VERTEX,{"disambiguationData":[OD(0.0)],"derivedFrom":[subQ1,subQ0]});Q136=makeQuery(id+"F0.imprint","IMPRINT",FACE,{"disambiguationData":[TD([[makeQuery(id+"F0.imprint","IMPRINT",EDGE,{"disambiguationData":[TD([[subQ2,1.0]])],"derivedFrom":subQ1}),1.0]])]});}
            var Q137;
            {var subQ0=sQuery(id+"F0.wireOp",EDGE,"E13.8.10");var subQ1=sQuery(id+"F0.wireOp",EDGE,"E13.8.9");var subQ2=makeQuery(id+"F0.imprint","INTERSECT",VERTEX,{"disambiguationData":[OD(0.0)],"derivedFrom":[subQ1,subQ0]});Q137=makeQuery(id+"F0.imprint","IMPRINT",FACE,{"disambiguationData":[TD([[makeQuery(id+"F0.imprint","IMPRINT",EDGE,{"disambiguationData":[TD([[subQ2,1.0]])],"derivedFrom":subQ1}),-1.0]])]});}
            var Q138;
            {var subQ0=sQuery(id+"F0.wireOp",EDGE,"E13.9.1");var subQ1=sQuery(id+"F0.wireOp",EDGE,"E13.9.0");var subQ2=makeQuery(id+"F0.imprint","INTERSECT",VERTEX,{"disambiguationData":[OD(0.0)],"derivedFrom":[subQ1,subQ0]});Q138=makeQuery(id+"F0.imprint","IMPRINT",FACE,{"disambiguationData":[TD([[makeQuery(id+"F0.imprint","IMPRINT",EDGE,{"disambiguationData":[TD([[subQ2,1.0]])],"derivedFrom":subQ1}),1.0]])]});}
            var Q139;
            {var subQ0=sQuery(id+"F0.wireOp",EDGE,"E13.9.10");var subQ1=sQuery(id+"F0.wireOp",EDGE,"E13.9.9");var subQ2=makeQuery(id+"F0.imprint","INTERSECT",VERTEX,{"disambiguationData":[OD(0.0)],"derivedFrom":[subQ1,subQ0]});Q139=makeQuery(id+"F0.imprint","IMPRINT",FACE,{"disambiguationData":[TD([[makeQuery(id+"F0.imprint","IMPRINT",EDGE,{"disambiguationData":[TD([[subQ2,1.0]])],"derivedFrom":subQ1}),-1.0]])]});}
            var Q140;
            {var subQ0=sQuery(id+"F0.wireOp",EDGE,"E13.10.1");var subQ1=sQuery(id+"F0.wireOp",EDGE,"E13.10.0");var subQ2=makeQuery(id+"F0.imprint","INTERSECT",VERTEX,{"disambiguationData":[OD(0.0)],"derivedFrom":[subQ1,subQ0]});Q140=makeQuery(id+"F0.imprint","IMPRINT",FACE,{"disambiguationData":[TD([[makeQuery(id+"F0.imprint","IMPRINT",EDGE,{"disambiguationData":[TD([[subQ2,1.0]])],"derivedFrom":subQ1}),1.0]])]});}
            var Q141;
            {var subQ0=sQuery(id+"F0.wireOp",EDGE,"E13.10.10");var subQ1=sQuery(id+"F0.wireOp",EDGE,"E13.10.9");var subQ2=makeQuery(id+"F0.imprint","INTERSECT",VERTEX,{"disambiguationData":[OD(0.0)],"derivedFrom":[subQ1,subQ0]});Q141=makeQuery(id+"F0.imprint","IMPRINT",FACE,{"disambiguationData":[TD([[makeQuery(id+"F0.imprint","IMPRINT",EDGE,{"disambiguationData":[TD([[subQ2,1.0]])],"derivedFrom":subQ1}),-1.0]])]});}
            var Q142;
            {var subQ0=sQuery(id+"F0.wireOp",EDGE,"E13.11.1");var subQ1=sQuery(id+"F0.wireOp",EDGE,"E13.11.0");var subQ2=makeQuery(id+"F0.imprint","INTERSECT",VERTEX,{"disambiguationData":[OD(0.0)],"derivedFrom":[subQ1,subQ0]});Q142=makeQuery(id+"F0.imprint","IMPRINT",FACE,{"disambiguationData":[TD([[makeQuery(id+"F0.imprint","IMPRINT",EDGE,{"disambiguationData":[TD([[subQ2,1.0]])],"derivedFrom":subQ1}),1.0]])]});}
            var Q143;
            {var subQ0=sQuery(id+"F0.wireOp",EDGE,"E13.11.10");var subQ1=sQuery(id+"F0.wireOp",EDGE,"E13.11.9");var subQ2=makeQuery(id+"F0.imprint","INTERSECT",VERTEX,{"disambiguationData":[OD(0.0)],"derivedFrom":[subQ1,subQ0]});Q143=makeQuery(id+"F0.imprint","IMPRINT",FACE,{"disambiguationData":[TD([[makeQuery(id+"F0.imprint","IMPRINT",EDGE,{"disambiguationData":[TD([[subQ2,1.0]])],"derivedFrom":subQ1}),-1.0]])]});}
            var Q144;
            {var subQ0=sQuery(id+"F0.wireOp",EDGE,"E13.12.1");var subQ1=sQuery(id+"F0.wireOp",EDGE,"E13.12.0");var subQ2=makeQuery(id+"F0.imprint","INTERSECT",VERTEX,{"disambiguationData":[OD(0.0)],"derivedFrom":[subQ1,subQ0]});Q144=makeQuery(id+"F0.imprint","IMPRINT",FACE,{"disambiguationData":[TD([[makeQuery(id+"F0.imprint","IMPRINT",EDGE,{"disambiguationData":[TD([[subQ2,1.0]])],"derivedFrom":subQ1}),1.0]])]});}
            var Q145;
            {var subQ0=sQuery(id+"F0.wireOp",EDGE,"E13.12.10");var subQ1=sQuery(id+"F0.wireOp",EDGE,"E13.12.9");var subQ2=makeQuery(id+"F0.imprint","INTERSECT",VERTEX,{"disambiguationData":[OD(0.0)],"derivedFrom":[subQ1,subQ0]});Q145=makeQuery(id+"F0.imprint","IMPRINT",FACE,{"disambiguationData":[TD([[makeQuery(id+"F0.imprint","IMPRINT",EDGE,{"disambiguationData":[TD([[subQ2,1.0]])],"derivedFrom":subQ1}),-1.0]])]});}
            var Q146;
            {var subQ0=sQuery(id+"F0.wireOp",EDGE,"E13.13.1");var subQ1=sQuery(id+"F0.wireOp",EDGE,"E13.13.0");var subQ2=makeQuery(id+"F0.imprint","INTERSECT",VERTEX,{"disambiguationData":[OD(0.0)],"derivedFrom":[subQ1,subQ0]});Q146=makeQuery(id+"F0.imprint","IMPRINT",FACE,{"disambiguationData":[TD([[makeQuery(id+"F0.imprint","IMPRINT",EDGE,{"disambiguationData":[TD([[subQ2,1.0]])],"derivedFrom":subQ1}),1.0]])]});}
            var Q147;
            {var subQ0=sQuery(id+"F0.wireOp",EDGE,"E13.13.10");var subQ1=sQuery(id+"F0.wireOp",EDGE,"E13.13.9");var subQ2=makeQuery(id+"F0.imprint","INTERSECT",VERTEX,{"disambiguationData":[OD(0.0)],"derivedFrom":[subQ1,subQ0]});Q147=makeQuery(id+"F0.imprint","IMPRINT",FACE,{"disambiguationData":[TD([[makeQuery(id+"F0.imprint","IMPRINT",EDGE,{"disambiguationData":[TD([[subQ2,1.0]])],"derivedFrom":subQ1}),-1.0]])]});}
            var Q148;
            {var subQ0=sQuery(id+"F0.wireOp",EDGE,"E13.14.1");var subQ1=sQuery(id+"F0.wireOp",EDGE,"E13.14.0");var subQ2=makeQuery(id+"F0.imprint","INTERSECT",VERTEX,{"disambiguationData":[OD(0.0)],"derivedFrom":[subQ1,subQ0]});Q148=makeQuery(id+"F0.imprint","IMPRINT",FACE,{"disambiguationData":[TD([[makeQuery(id+"F0.imprint","IMPRINT",EDGE,{"disambiguationData":[TD([[subQ2,1.0]])],"derivedFrom":subQ1}),1.0]])]});}
            var Q149;
            {var subQ0=sQuery(id+"F0.wireOp",EDGE,"E13.14.10");var subQ1=sQuery(id+"F0.wireOp",EDGE,"E13.14.9");var subQ2=makeQuery(id+"F0.imprint","INTERSECT",VERTEX,{"disambiguationData":[OD(0.0)],"derivedFrom":[subQ1,subQ0]});Q149=makeQuery(id+"F0.imprint","IMPRINT",FACE,{"disambiguationData":[TD([[makeQuery(id+"F0.imprint","IMPRINT",EDGE,{"disambiguationData":[TD([[subQ2,1.0]])],"derivedFrom":subQ1}),-1.0]])]});}
            var Q150;
            {var subQ0=sQuery(id+"F0.wireOp",EDGE,"E13.15.1");var subQ1=sQuery(id+"F0.wireOp",EDGE,"E13.15.0");var subQ2=makeQuery(id+"F0.imprint","INTERSECT",VERTEX,{"disambiguationData":[OD(0.0)],"derivedFrom":[subQ1,subQ0]});Q150=makeQuery(id+"F0.imprint","IMPRINT",FACE,{"disambiguationData":[TD([[makeQuery(id+"F0.imprint","IMPRINT",EDGE,{"disambiguationData":[TD([[subQ2,1.0]])],"derivedFrom":subQ1}),1.0]])]});}
            var Q151;
            {var subQ0=sQuery(id+"F0.wireOp",EDGE,"E13.15.10");var subQ1=sQuery(id+"F0.wireOp",EDGE,"E13.15.9");var subQ2=makeQuery(id+"F0.imprint","INTERSECT",VERTEX,{"disambiguationData":[OD(0.0)],"derivedFrom":[subQ1,subQ0]});Q151=makeQuery(id+"F0.imprint","IMPRINT",FACE,{"disambiguationData":[TD([[makeQuery(id+"F0.imprint","IMPRINT",EDGE,{"disambiguationData":[TD([[subQ2,1.0]])],"derivedFrom":subQ1}),-1.0]])]});}
            var Q152;
            {var subQ0=sQuery(id+"F0.wireOp",EDGE,"E13.16.1");var subQ1=sQuery(id+"F0.wireOp",EDGE,"E13.16.0");var subQ2=makeQuery(id+"F0.imprint","INTERSECT",VERTEX,{"disambiguationData":[OD(0.0)],"derivedFrom":[subQ1,subQ0]});Q152=makeQuery(id+"F0.imprint","IMPRINT",FACE,{"disambiguationData":[TD([[makeQuery(id+"F0.imprint","IMPRINT",EDGE,{"disambiguationData":[TD([[subQ2,1.0]])],"derivedFrom":subQ1}),1.0]])]});}
            var Q153;
            {var subQ0=sQuery(id+"F0.wireOp",EDGE,"E13.16.10");var subQ1=sQuery(id+"F0.wireOp",EDGE,"E13.16.9");var subQ2=makeQuery(id+"F0.imprint","INTERSECT",VERTEX,{"disambiguationData":[OD(0.0)],"derivedFrom":[subQ1,subQ0]});Q153=makeQuery(id+"F0.imprint","IMPRINT",FACE,{"disambiguationData":[TD([[makeQuery(id+"F0.imprint","IMPRINT",EDGE,{"disambiguationData":[TD([[subQ2,1.0]])],"derivedFrom":subQ1}),-1.0]])]});}
            var Q154;
            {var subQ0=sQuery(id+"F0.wireOp",EDGE,"E13.17.1");var subQ1=sQuery(id+"F0.wireOp",EDGE,"E13.17.0");var subQ2=makeQuery(id+"F0.imprint","INTERSECT",VERTEX,{"disambiguationData":[OD(0.0)],"derivedFrom":[subQ1,subQ0]});Q154=makeQuery(id+"F0.imprint","IMPRINT",FACE,{"disambiguationData":[TD([[makeQuery(id+"F0.imprint","IMPRINT",EDGE,{"disambiguationData":[TD([[subQ2,1.0]])],"derivedFrom":subQ1}),1.0]])]});}
            var Q155;
            {var subQ0=sQuery(id+"F0.wireOp",EDGE,"E13.17.10");var subQ1=sQuery(id+"F0.wireOp",EDGE,"E13.17.9");var subQ2=makeQuery(id+"F0.imprint","INTERSECT",VERTEX,{"disambiguationData":[OD(0.0)],"derivedFrom":[subQ1,subQ0]});Q155=makeQuery(id+"F0.imprint","IMPRINT",FACE,{"disambiguationData":[TD([[makeQuery(id+"F0.imprint","IMPRINT",EDGE,{"disambiguationData":[TD([[subQ2,1.0]])],"derivedFrom":subQ1}),-1.0]])]});}
            var Q156;
            {var subQ0=sQuery(id+"F0.wireOp",EDGE,"E13.18.1");var subQ1=sQuery(id+"F0.wireOp",EDGE,"E13.18.0");var subQ2=makeQuery(id+"F0.imprint","INTERSECT",VERTEX,{"disambiguationData":[OD(0.0)],"derivedFrom":[subQ1,subQ0]});Q156=makeQuery(id+"F0.imprint","IMPRINT",FACE,{"disambiguationData":[TD([[makeQuery(id+"F0.imprint","IMPRINT",EDGE,{"disambiguationData":[TD([[subQ2,1.0]])],"derivedFrom":subQ1}),1.0]])]});}
            var Q157;
            {var subQ0=sQuery(id+"F0.wireOp",EDGE,"E13.18.10");var subQ1=sQuery(id+"F0.wireOp",EDGE,"E13.18.9");var subQ2=makeQuery(id+"F0.imprint","INTERSECT",VERTEX,{"disambiguationData":[OD(0.0)],"derivedFrom":[subQ1,subQ0]});Q157=makeQuery(id+"F0.imprint","IMPRINT",FACE,{"disambiguationData":[TD([[makeQuery(id+"F0.imprint","IMPRINT",EDGE,{"disambiguationData":[TD([[subQ2,1.0]])],"derivedFrom":subQ1}),-1.0]])]});}
            var Q158;
            {var subQ0=sQuery(id+"F0.wireOp",EDGE,"E13.19.1");var subQ1=sQuery(id+"F0.wireOp",EDGE,"E13.19.0");var subQ2=makeQuery(id+"F0.imprint","INTERSECT",VERTEX,{"disambiguationData":[OD(0.0)],"derivedFrom":[subQ1,subQ0]});Q158=makeQuery(id+"F0.imprint","IMPRINT",FACE,{"disambiguationData":[TD([[makeQuery(id+"F0.imprint","IMPRINT",EDGE,{"disambiguationData":[TD([[subQ2,1.0]])],"derivedFrom":subQ1}),1.0]])]});}
            var Q159;
            {var subQ0=sQuery(id+"F0.wireOp",EDGE,"E13.19.10");var subQ1=sQuery(id+"F0.wireOp",EDGE,"E13.19.9");var subQ2=makeQuery(id+"F0.imprint","INTERSECT",VERTEX,{"disambiguationData":[OD(0.0)],"derivedFrom":[subQ1,subQ0]});Q159=makeQuery(id+"F0.imprint","IMPRINT",FACE,{"disambiguationData":[TD([[makeQuery(id+"F0.imprint","IMPRINT",EDGE,{"disambiguationData":[TD([[subQ2,1.0]])],"derivedFrom":subQ1}),-1.0]])]});}
            var Q160;
            {var subQ0=sQuery(id+"F0.wireOp",EDGE,"E13.20.1");var subQ1=sQuery(id+"F0.wireOp",EDGE,"E13.20.0");var subQ2=makeQuery(id+"F0.imprint","INTERSECT",VERTEX,{"disambiguationData":[OD(0.0)],"derivedFrom":[subQ1,subQ0]});Q160=makeQuery(id+"F0.imprint","IMPRINT",FACE,{"disambiguationData":[TD([[makeQuery(id+"F0.imprint","IMPRINT",EDGE,{"disambiguationData":[TD([[subQ2,1.0]])],"derivedFrom":subQ1}),1.0]])]});}
            var Q161;
            {var subQ0=sQuery(id+"F0.wireOp",EDGE,"E13.20.10");var subQ1=sQuery(id+"F0.wireOp",EDGE,"E13.20.9");var subQ2=makeQuery(id+"F0.imprint","INTERSECT",VERTEX,{"disambiguationData":[OD(0.0)],"derivedFrom":[subQ1,subQ0]});Q161=makeQuery(id+"F0.imprint","IMPRINT",FACE,{"disambiguationData":[TD([[makeQuery(id+"F0.imprint","IMPRINT",EDGE,{"disambiguationData":[TD([[subQ2,1.0]])],"derivedFrom":subQ1}),-1.0]])]});}
            var Q162;
            {var subQ0=sQuery(id+"F0.wireOp",EDGE,"E13.21.1");var subQ1=sQuery(id+"F0.wireOp",EDGE,"E13.21.0");var subQ2=makeQuery(id+"F0.imprint","INTERSECT",VERTEX,{"disambiguationData":[OD(0.0)],"derivedFrom":[subQ1,subQ0]});Q162=makeQuery(id+"F0.imprint","IMPRINT",FACE,{"disambiguationData":[TD([[makeQuery(id+"F0.imprint","IMPRINT",EDGE,{"disambiguationData":[TD([[subQ2,1.0]])],"derivedFrom":subQ1}),1.0]])]});}
            var Q163;
            {var subQ0=sQuery(id+"F0.wireOp",EDGE,"E13.21.10");var subQ1=sQuery(id+"F0.wireOp",EDGE,"E13.21.9");var subQ2=makeQuery(id+"F0.imprint","INTERSECT",VERTEX,{"disambiguationData":[OD(0.0)],"derivedFrom":[subQ1,subQ0]});Q163=makeQuery(id+"F0.imprint","IMPRINT",FACE,{"disambiguationData":[TD([[makeQuery(id+"F0.imprint","IMPRINT",EDGE,{"disambiguationData":[TD([[subQ2,1.0]])],"derivedFrom":subQ1}),-1.0]])]});}
            var Q164;
            {var subQ0=sQuery(id+"F0.wireOp",EDGE,"E13.22.1");var subQ1=sQuery(id+"F0.wireOp",EDGE,"E13.22.0");var subQ2=makeQuery(id+"F0.imprint","INTERSECT",VERTEX,{"disambiguationData":[OD(0.0)],"derivedFrom":[subQ1,subQ0]});Q164=makeQuery(id+"F0.imprint","IMPRINT",FACE,{"disambiguationData":[TD([[makeQuery(id+"F0.imprint","IMPRINT",EDGE,{"disambiguationData":[TD([[subQ2,1.0]])],"derivedFrom":subQ1}),1.0]])]});}
            var Q165;
            {var subQ0=sQuery(id+"F0.wireOp",EDGE,"E13.22.10");var subQ1=sQuery(id+"F0.wireOp",EDGE,"E13.22.9");var subQ2=makeQuery(id+"F0.imprint","INTERSECT",VERTEX,{"disambiguationData":[OD(0.0)],"derivedFrom":[subQ1,subQ0]});Q165=makeQuery(id+"F0.imprint","IMPRINT",FACE,{"disambiguationData":[TD([[makeQuery(id+"F0.imprint","IMPRINT",EDGE,{"disambiguationData":[TD([[subQ2,1.0]])],"derivedFrom":subQ1}),-1.0]])]});}
            var Q166;
            {var subQ0=sQuery(id+"F0.wireOp",EDGE,"E13.23.1");var subQ1=sQuery(id+"F0.wireOp",EDGE,"E13.23.0");var subQ2=makeQuery(id+"F0.imprint","INTERSECT",VERTEX,{"disambiguationData":[OD(0.0)],"derivedFrom":[subQ1,subQ0]});Q166=makeQuery(id+"F0.imprint","IMPRINT",FACE,{"disambiguationData":[TD([[makeQuery(id+"F0.imprint","IMPRINT",EDGE,{"disambiguationData":[TD([[subQ2,1.0]])],"derivedFrom":subQ1}),1.0]])]});}
            var Q167;
            {var subQ0=sQuery(id+"F0.wireOp",EDGE,"E13.23.10");var subQ1=sQuery(id+"F0.wireOp",EDGE,"E13.23.9");var subQ2=makeQuery(id+"F0.imprint","INTERSECT",VERTEX,{"disambiguationData":[OD(0.0)],"derivedFrom":[subQ1,subQ0]});Q167=makeQuery(id+"F0.imprint","IMPRINT",FACE,{"disambiguationData":[TD([[makeQuery(id+"F0.imprint","IMPRINT",EDGE,{"disambiguationData":[TD([[subQ2,1.0]])],"derivedFrom":subQ1}),-1.0]])]});}
            var Q168;
            {var subQ0=sQuery(id+"F0.wireOp",EDGE,"E11");var subQ1=sQuery(id+"F0.wireOp",EDGE,"E0");var subQ2=makeQuery(id+"F0.imprint","INTERSECT",VERTEX,{"disambiguationData":[OD(0.0)],"derivedFrom":[subQ1,subQ0]});Q168=makeQuery(id+"F0.imprint","IMPRINT",FACE,{"disambiguationData":[TD([[makeQuery(id+"F0.imprint","IMPRINT",EDGE,{"disambiguationData":[TD([[subQ2,-1.0]])],"derivedFrom":subQ1}),1.0]])]});}
            var Q169;
            {var subQ0=sQuery(id+"F0.wireOp",EDGE,"E11");var subQ1=sQuery(id+"F0.wireOp",EDGE,"E0");var subQ2=makeQuery(id+"F0.imprint","INTERSECT",VERTEX,{"disambiguationData":[OD(1.0)],"derivedFrom":[subQ1,subQ0]});Q169=makeQuery(id+"F0.imprint","IMPRINT",FACE,{"disambiguationData":[TD([[makeQuery(id+"F0.imprint","IMPRINT",EDGE,{"disambiguationData":[TD([[subQ2,1.0]])],"derivedFrom":subQ1}),1.0]])]});}
            var Q170;
            {var subQ0=sQuery(id+"F0.wireOp",EDGE,"E13.1.10");var subQ1=sQuery(id+"F0.wireOp",EDGE,"E0");var subQ2=makeQuery(id+"F0.imprint","INTERSECT",VERTEX,{"disambiguationData":[OD(0.0)],"derivedFrom":[subQ1,subQ0]});Q170=makeQuery(id+"F0.imprint","IMPRINT",FACE,{"disambiguationData":[TD([[makeQuery(id+"F0.imprint","IMPRINT",EDGE,{"disambiguationData":[TD([[subQ2,1.0]])],"derivedFrom":subQ1}),1.0]])]});}
            var Q171;
            {var subQ0=sQuery(id+"F0.wireOp",EDGE,"E17.trimOffspring");var subQ1=sQuery(id+"F0.wireOp",EDGE,"E12");var subQ2=makeQuery(id+"F0.imprint","INTERSECT",VERTEX,{"disambiguationData":[OD(1.0)],"derivedFrom":[subQ1,subQ0]});Q171=makeQuery(id+"F0.imprint","IMPRINT",FACE,{"disambiguationData":[TD([[makeQuery(id+"F0.imprint","IMPRINT",EDGE,{"disambiguationData":[TD([[subQ2,-1.0]])],"derivedFrom":subQ1}),1.0]])]});}
            var Q172;
            {var subQ0=sQuery(id+"F0.wireOp",EDGE,"E17.trimOffspring");var subQ1=sQuery(id+"F0.wireOp",EDGE,"E12");var subQ2=makeQuery(id+"F0.imprint","INTERSECT",VERTEX,{"disambiguationData":[OD(0.0)],"derivedFrom":[subQ1,subQ0]});Q172=makeQuery(id+"F0.imprint","IMPRINT",FACE,{"disambiguationData":[TD([[makeQuery(id+"F0.imprint","IMPRINT",EDGE,{"disambiguationData":[TD([[subQ2,1.0]])],"derivedFrom":subQ1}),1.0]])]});}
            var Q173;
            {var subQ0=sQuery(id+"F0.wireOp",EDGE,"E17.trimOffspring");var subQ1=sQuery(id+"F0.wireOp",EDGE,"E12");var subQ2=makeQuery(id+"F0.imprint","INTERSECT",VERTEX,{"disambiguationData":[OD(0.0)],"derivedFrom":[subQ1,subQ0]});Q173=makeQuery(id+"F0.imprint","IMPRINT",FACE,{"disambiguationData":[TD([[makeQuery(id+"F0.imprint","IMPRINT",EDGE,{"disambiguationData":[TD([[subQ2,1.0]])],"derivedFrom":subQ1}),-1.0]])]});}
            var Q174;
            {var subQ0=sQuery(id+"F0.wireOp",EDGE,"E14.trimOffspring");var subQ1=sQuery(id+"F0.wireOp",EDGE,"E13.1.0");var subQ2=makeQuery(id+"F0.imprint","INTERSECT",VERTEX,{"disambiguationData":[OD(0.0)],"derivedFrom":[subQ1,subQ0]});Q174=makeQuery(id+"F0.imprint","IMPRINT",FACE,{"disambiguationData":[TD([[makeQuery(id+"F0.imprint","IMPRINT",EDGE,{"disambiguationData":[TD([[subQ2,-1.0]])],"derivedFrom":subQ1}),-1.0]])]});}
            var Q175;
            {var subQ0=sQuery(id+"F0.wireOp",EDGE,"E14.trimOffspring");var subQ1=sQuery(id+"F0.wireOp",EDGE,"E13.1.0");var subQ2=makeQuery(id+"F0.imprint","INTERSECT",VERTEX,{"disambiguationData":[OD(0.0)],"derivedFrom":[subQ1,subQ0]});Q175=makeQuery(id+"F0.imprint","IMPRINT",FACE,{"disambiguationData":[TD([[makeQuery(id+"F0.imprint","IMPRINT",EDGE,{"disambiguationData":[TD([[subQ2,-1.0]])],"derivedFrom":subQ1}),1.0]])]});}
            var Q176;
            {var subQ0=sQuery(id+"F0.wireOp",EDGE,"E14.trimOffspring");var subQ1=sQuery(id+"F0.wireOp",EDGE,"E13.1.0");var subQ2=makeQuery(id+"F0.imprint","INTERSECT",VERTEX,{"disambiguationData":[OD(1.0)],"derivedFrom":[subQ1,subQ0]});Q176=makeQuery(id+"F0.imprint","IMPRINT",FACE,{"disambiguationData":[TD([[makeQuery(id+"F0.imprint","IMPRINT",EDGE,{"disambiguationData":[TD([[subQ2,1.0]])],"derivedFrom":subQ1}),1.0]])]});}
            var Q177;
            {var subQ0=sQuery(id+"F0.wireOp",EDGE,"E16.trimOffspring");var subQ1=sQuery(id+"F0.wireOp",EDGE,"E13.2.0");var subQ2=makeQuery(id+"F0.imprint","INTERSECT",VERTEX,{"disambiguationData":[OD(0.0)],"derivedFrom":[subQ1,subQ0]});Q177=makeQuery(id+"F0.imprint","IMPRINT",FACE,{"disambiguationData":[TD([[makeQuery(id+"F0.imprint","IMPRINT",EDGE,{"disambiguationData":[TD([[subQ2,-1.0]])],"derivedFrom":subQ1}),-1.0]])]});}
            var Q178;
            {var subQ0=sQuery(id+"F0.wireOp",EDGE,"E16.trimOffspring");var subQ1=sQuery(id+"F0.wireOp",EDGE,"E13.2.0");var subQ2=makeQuery(id+"F0.imprint","INTERSECT",VERTEX,{"disambiguationData":[OD(0.0)],"derivedFrom":[subQ1,subQ0]});Q178=makeQuery(id+"F0.imprint","IMPRINT",FACE,{"disambiguationData":[TD([[makeQuery(id+"F0.imprint","IMPRINT",EDGE,{"disambiguationData":[TD([[subQ2,-1.0]])],"derivedFrom":subQ1}),1.0]])]});}
            var Q179;
            {var subQ0=sQuery(id+"F0.wireOp",EDGE,"E16.trimOffspring");var subQ1=sQuery(id+"F0.wireOp",EDGE,"E13.2.0");var subQ2=makeQuery(id+"F0.imprint","INTERSECT",VERTEX,{"disambiguationData":[OD(1.0)],"derivedFrom":[subQ1,subQ0]});Q179=makeQuery(id+"F0.imprint","IMPRINT",FACE,{"disambiguationData":[TD([[makeQuery(id+"F0.imprint","IMPRINT",EDGE,{"disambiguationData":[TD([[subQ2,1.0]])],"derivedFrom":subQ1}),1.0]])]});}
            var Q180;
            {var subQ0=sQuery(id+"F0.wireOp",EDGE,"E15.trimOffspring");var subQ1=sQuery(id+"F0.wireOp",EDGE,"E13.3.0");var subQ2=makeQuery(id+"F0.imprint","INTERSECT",VERTEX,{"disambiguationData":[OD(0.0)],"derivedFrom":[subQ1,subQ0]});Q180=makeQuery(id+"F0.imprint","IMPRINT",FACE,{"disambiguationData":[TD([[makeQuery(id+"F0.imprint","IMPRINT",EDGE,{"disambiguationData":[TD([[subQ2,-1.0]])],"derivedFrom":subQ1}),-1.0]])]});}
            var Q181;
            {var subQ0=sQuery(id+"F0.wireOp",EDGE,"E15.trimOffspring");var subQ1=sQuery(id+"F0.wireOp",EDGE,"E13.3.0");var subQ2=makeQuery(id+"F0.imprint","INTERSECT",VERTEX,{"disambiguationData":[OD(0.0)],"derivedFrom":[subQ1,subQ0]});Q181=makeQuery(id+"F0.imprint","IMPRINT",FACE,{"disambiguationData":[TD([[makeQuery(id+"F0.imprint","IMPRINT",EDGE,{"disambiguationData":[TD([[subQ2,-1.0]])],"derivedFrom":subQ1}),1.0]])]});}
            var Q182;
            {var subQ0=sQuery(id+"F0.wireOp",EDGE,"E15.trimOffspring");var subQ1=sQuery(id+"F0.wireOp",EDGE,"E13.3.0");var subQ2=makeQuery(id+"F0.imprint","INTERSECT",VERTEX,{"disambiguationData":[OD(1.0)],"derivedFrom":[subQ1,subQ0]});Q182=makeQuery(id+"F0.imprint","IMPRINT",FACE,{"disambiguationData":[TD([[makeQuery(id+"F0.imprint","IMPRINT",EDGE,{"disambiguationData":[TD([[subQ2,1.0]])],"derivedFrom":subQ1}),1.0]])]});}
            var Q183;
            {var subQ0=sQuery(id+"F0.wireOp",EDGE,"E36.trimOffspring");var subQ1=sQuery(id+"F0.wireOp",EDGE,"E13.4.0");var subQ2=makeQuery(id+"F0.imprint","INTERSECT",VERTEX,{"disambiguationData":[OD(0.0)],"derivedFrom":[subQ1,subQ0]});Q183=makeQuery(id+"F0.imprint","IMPRINT",FACE,{"disambiguationData":[TD([[makeQuery(id+"F0.imprint","IMPRINT",EDGE,{"disambiguationData":[TD([[subQ2,-1.0]])],"derivedFrom":subQ1}),-1.0]])]});}
            var Q184;
            {var subQ0=sQuery(id+"F0.wireOp",EDGE,"E36.trimOffspring");var subQ1=sQuery(id+"F0.wireOp",EDGE,"E13.4.0");var subQ2=makeQuery(id+"F0.imprint","INTERSECT",VERTEX,{"disambiguationData":[OD(0.0)],"derivedFrom":[subQ1,subQ0]});Q184=makeQuery(id+"F0.imprint","IMPRINT",FACE,{"disambiguationData":[TD([[makeQuery(id+"F0.imprint","IMPRINT",EDGE,{"disambiguationData":[TD([[subQ2,-1.0]])],"derivedFrom":subQ1}),1.0]])]});}
            var Q185;
            {var subQ0=sQuery(id+"F0.wireOp",EDGE,"E36.trimOffspring");var subQ1=sQuery(id+"F0.wireOp",EDGE,"E13.4.0");var subQ2=makeQuery(id+"F0.imprint","INTERSECT",VERTEX,{"disambiguationData":[OD(1.0)],"derivedFrom":[subQ1,subQ0]});Q185=makeQuery(id+"F0.imprint","IMPRINT",FACE,{"disambiguationData":[TD([[makeQuery(id+"F0.imprint","IMPRINT",EDGE,{"disambiguationData":[TD([[subQ2,1.0]])],"derivedFrom":subQ1}),1.0]])]});}
            var Q186;
            {var subQ0=sQuery(id+"F0.wireOp",EDGE,"E35.trimOffspring");var subQ1=sQuery(id+"F0.wireOp",EDGE,"E13.5.0");var subQ2=makeQuery(id+"F0.imprint","INTERSECT",VERTEX,{"disambiguationData":[OD(0.0)],"derivedFrom":[subQ1,subQ0]});Q186=makeQuery(id+"F0.imprint","IMPRINT",FACE,{"disambiguationData":[TD([[makeQuery(id+"F0.imprint","IMPRINT",EDGE,{"disambiguationData":[TD([[subQ2,-1.0]])],"derivedFrom":subQ1}),-1.0]])]});}
            var Q187;
            {var subQ0=sQuery(id+"F0.wireOp",EDGE,"E35.trimOffspring");var subQ1=sQuery(id+"F0.wireOp",EDGE,"E13.5.0");var subQ2=makeQuery(id+"F0.imprint","INTERSECT",VERTEX,{"disambiguationData":[OD(0.0)],"derivedFrom":[subQ1,subQ0]});Q187=makeQuery(id+"F0.imprint","IMPRINT",FACE,{"disambiguationData":[TD([[makeQuery(id+"F0.imprint","IMPRINT",EDGE,{"disambiguationData":[TD([[subQ2,-1.0]])],"derivedFrom":subQ1}),1.0]])]});}
            var Q188;
            {var subQ0=sQuery(id+"F0.wireOp",EDGE,"E35.trimOffspring");var subQ1=sQuery(id+"F0.wireOp",EDGE,"E13.5.0");var subQ2=makeQuery(id+"F0.imprint","INTERSECT",VERTEX,{"disambiguationData":[OD(1.0)],"derivedFrom":[subQ1,subQ0]});Q188=makeQuery(id+"F0.imprint","IMPRINT",FACE,{"disambiguationData":[TD([[makeQuery(id+"F0.imprint","IMPRINT",EDGE,{"disambiguationData":[TD([[subQ2,1.0]])],"derivedFrom":subQ1}),1.0]])]});}
            var Q189;
            {var subQ0=sQuery(id+"F0.wireOp",EDGE,"E34.trimOffspring");var subQ1=sQuery(id+"F0.wireOp",EDGE,"E13.6.0");var subQ2=makeQuery(id+"F0.imprint","INTERSECT",VERTEX,{"disambiguationData":[OD(0.0)],"derivedFrom":[subQ1,subQ0]});Q189=makeQuery(id+"F0.imprint","IMPRINT",FACE,{"disambiguationData":[TD([[makeQuery(id+"F0.imprint","IMPRINT",EDGE,{"disambiguationData":[TD([[subQ2,-1.0]])],"derivedFrom":subQ1}),-1.0]])]});}
            var Q190;
            {var subQ0=sQuery(id+"F0.wireOp",EDGE,"E34.trimOffspring");var subQ1=sQuery(id+"F0.wireOp",EDGE,"E13.6.0");var subQ2=makeQuery(id+"F0.imprint","INTERSECT",VERTEX,{"disambiguationData":[OD(0.0)],"derivedFrom":[subQ1,subQ0]});Q190=makeQuery(id+"F0.imprint","IMPRINT",FACE,{"disambiguationData":[TD([[makeQuery(id+"F0.imprint","IMPRINT",EDGE,{"disambiguationData":[TD([[subQ2,-1.0]])],"derivedFrom":subQ1}),1.0]])]});}
            var Q191;
            {var subQ0=sQuery(id+"F0.wireOp",EDGE,"E34.trimOffspring");var subQ1=sQuery(id+"F0.wireOp",EDGE,"E13.6.0");var subQ2=makeQuery(id+"F0.imprint","INTERSECT",VERTEX,{"disambiguationData":[OD(1.0)],"derivedFrom":[subQ1,subQ0]});Q191=makeQuery(id+"F0.imprint","IMPRINT",FACE,{"disambiguationData":[TD([[makeQuery(id+"F0.imprint","IMPRINT",EDGE,{"disambiguationData":[TD([[subQ2,1.0]])],"derivedFrom":subQ1}),1.0]])]});}
            var Q192;
            {var subQ0=sQuery(id+"F0.wireOp",EDGE,"E33.trimOffspring");var subQ1=sQuery(id+"F0.wireOp",EDGE,"E13.7.0");var subQ2=makeQuery(id+"F0.imprint","INTERSECT",VERTEX,{"disambiguationData":[OD(0.0)],"derivedFrom":[subQ1,subQ0]});Q192=makeQuery(id+"F0.imprint","IMPRINT",FACE,{"disambiguationData":[TD([[makeQuery(id+"F0.imprint","IMPRINT",EDGE,{"disambiguationData":[TD([[subQ2,-1.0]])],"derivedFrom":subQ1}),-1.0]])]});}
            var Q193;
            {var subQ0=sQuery(id+"F0.wireOp",EDGE,"E33.trimOffspring");var subQ1=sQuery(id+"F0.wireOp",EDGE,"E13.7.0");var subQ2=makeQuery(id+"F0.imprint","INTERSECT",VERTEX,{"disambiguationData":[OD(0.0)],"derivedFrom":[subQ1,subQ0]});Q193=makeQuery(id+"F0.imprint","IMPRINT",FACE,{"disambiguationData":[TD([[makeQuery(id+"F0.imprint","IMPRINT",EDGE,{"disambiguationData":[TD([[subQ2,-1.0]])],"derivedFrom":subQ1}),1.0]])]});}
            var Q194;
            {var subQ0=sQuery(id+"F0.wireOp",EDGE,"E33.trimOffspring");var subQ1=sQuery(id+"F0.wireOp",EDGE,"E13.7.0");var subQ2=makeQuery(id+"F0.imprint","INTERSECT",VERTEX,{"disambiguationData":[OD(1.0)],"derivedFrom":[subQ1,subQ0]});Q194=makeQuery(id+"F0.imprint","IMPRINT",FACE,{"disambiguationData":[TD([[makeQuery(id+"F0.imprint","IMPRINT",EDGE,{"disambiguationData":[TD([[subQ2,1.0]])],"derivedFrom":subQ1}),1.0]])]});}
            var Q195;
            {var subQ0=sQuery(id+"F0.wireOp",EDGE,"E32.trimOffspring");var subQ1=sQuery(id+"F0.wireOp",EDGE,"E13.8.0");var subQ2=makeQuery(id+"F0.imprint","INTERSECT",VERTEX,{"disambiguationData":[OD(0.0)],"derivedFrom":[subQ1,subQ0]});Q195=makeQuery(id+"F0.imprint","IMPRINT",FACE,{"disambiguationData":[TD([[makeQuery(id+"F0.imprint","IMPRINT",EDGE,{"disambiguationData":[TD([[subQ2,-1.0]])],"derivedFrom":subQ1}),-1.0]])]});}
            var Q196;
            {var subQ0=sQuery(id+"F0.wireOp",EDGE,"E32.trimOffspring");var subQ1=sQuery(id+"F0.wireOp",EDGE,"E13.8.0");var subQ2=makeQuery(id+"F0.imprint","INTERSECT",VERTEX,{"disambiguationData":[OD(0.0)],"derivedFrom":[subQ1,subQ0]});Q196=makeQuery(id+"F0.imprint","IMPRINT",FACE,{"disambiguationData":[TD([[makeQuery(id+"F0.imprint","IMPRINT",EDGE,{"disambiguationData":[TD([[subQ2,-1.0]])],"derivedFrom":subQ1}),1.0]])]});}
            var Q197;
            {var subQ0=sQuery(id+"F0.wireOp",EDGE,"E32.trimOffspring");var subQ1=sQuery(id+"F0.wireOp",EDGE,"E13.8.0");var subQ2=makeQuery(id+"F0.imprint","INTERSECT",VERTEX,{"disambiguationData":[OD(1.0)],"derivedFrom":[subQ1,subQ0]});Q197=makeQuery(id+"F0.imprint","IMPRINT",FACE,{"disambiguationData":[TD([[makeQuery(id+"F0.imprint","IMPRINT",EDGE,{"disambiguationData":[TD([[subQ2,1.0]])],"derivedFrom":subQ1}),1.0]])]});}
            var Q198;
            {var subQ0=sQuery(id+"F0.wireOp",EDGE,"E31.trimOffspring");var subQ1=sQuery(id+"F0.wireOp",EDGE,"E13.9.0");var subQ2=makeQuery(id+"F0.imprint","INTERSECT",VERTEX,{"disambiguationData":[OD(0.0)],"derivedFrom":[subQ1,subQ0]});Q198=makeQuery(id+"F0.imprint","IMPRINT",FACE,{"disambiguationData":[TD([[makeQuery(id+"F0.imprint","IMPRINT",EDGE,{"disambiguationData":[TD([[subQ2,-1.0]])],"derivedFrom":subQ1}),-1.0]])]});}
            var Q199;
            {var subQ0=sQuery(id+"F0.wireOp",EDGE,"E31.trimOffspring");var subQ1=sQuery(id+"F0.wireOp",EDGE,"E13.9.0");var subQ2=makeQuery(id+"F0.imprint","INTERSECT",VERTEX,{"disambiguationData":[OD(0.0)],"derivedFrom":[subQ1,subQ0]});Q199=makeQuery(id+"F0.imprint","IMPRINT",FACE,{"disambiguationData":[TD([[makeQuery(id+"F0.imprint","IMPRINT",EDGE,{"disambiguationData":[TD([[subQ2,-1.0]])],"derivedFrom":subQ1}),1.0]])]});}
            var Q200;
            {var subQ0=sQuery(id+"F0.wireOp",EDGE,"E31.trimOffspring");var subQ1=sQuery(id+"F0.wireOp",EDGE,"E13.9.0");var subQ2=makeQuery(id+"F0.imprint","INTERSECT",VERTEX,{"disambiguationData":[OD(1.0)],"derivedFrom":[subQ1,subQ0]});Q200=makeQuery(id+"F0.imprint","IMPRINT",FACE,{"disambiguationData":[TD([[makeQuery(id+"F0.imprint","IMPRINT",EDGE,{"disambiguationData":[TD([[subQ2,1.0]])],"derivedFrom":subQ1}),1.0]])]});}
            var Q201;
            {var subQ0=sQuery(id+"F0.wireOp",EDGE,"E30.trimOffspring");var subQ1=sQuery(id+"F0.wireOp",EDGE,"E13.10.0");var subQ2=makeQuery(id+"F0.imprint","INTERSECT",VERTEX,{"disambiguationData":[OD(0.0)],"derivedFrom":[subQ1,subQ0]});Q201=makeQuery(id+"F0.imprint","IMPRINT",FACE,{"disambiguationData":[TD([[makeQuery(id+"F0.imprint","IMPRINT",EDGE,{"disambiguationData":[TD([[subQ2,-1.0]])],"derivedFrom":subQ1}),-1.0]])]});}
            var Q202;
            {var subQ0=sQuery(id+"F0.wireOp",EDGE,"E30.trimOffspring");var subQ1=sQuery(id+"F0.wireOp",EDGE,"E13.10.0");var subQ2=makeQuery(id+"F0.imprint","INTERSECT",VERTEX,{"disambiguationData":[OD(0.0)],"derivedFrom":[subQ1,subQ0]});Q202=makeQuery(id+"F0.imprint","IMPRINT",FACE,{"disambiguationData":[TD([[makeQuery(id+"F0.imprint","IMPRINT",EDGE,{"disambiguationData":[TD([[subQ2,-1.0]])],"derivedFrom":subQ1}),1.0]])]});}
            var Q203;
            {var subQ0=sQuery(id+"F0.wireOp",EDGE,"E30.trimOffspring");var subQ1=sQuery(id+"F0.wireOp",EDGE,"E13.10.0");var subQ2=makeQuery(id+"F0.imprint","INTERSECT",VERTEX,{"disambiguationData":[OD(1.0)],"derivedFrom":[subQ1,subQ0]});Q203=makeQuery(id+"F0.imprint","IMPRINT",FACE,{"disambiguationData":[TD([[makeQuery(id+"F0.imprint","IMPRINT",EDGE,{"disambiguationData":[TD([[subQ2,1.0]])],"derivedFrom":subQ1}),1.0]])]});}
            var Q204;
            {var subQ0=sQuery(id+"F0.wireOp",EDGE,"E29.trimOffspring");var subQ1=sQuery(id+"F0.wireOp",EDGE,"E13.11.0");var subQ2=makeQuery(id+"F0.imprint","INTERSECT",VERTEX,{"disambiguationData":[OD(0.0)],"derivedFrom":[subQ1,subQ0]});Q204=makeQuery(id+"F0.imprint","IMPRINT",FACE,{"disambiguationData":[TD([[makeQuery(id+"F0.imprint","IMPRINT",EDGE,{"disambiguationData":[TD([[subQ2,-1.0]])],"derivedFrom":subQ1}),-1.0]])]});}
            var Q205;
            {var subQ0=sQuery(id+"F0.wireOp",EDGE,"E29.trimOffspring");var subQ1=sQuery(id+"F0.wireOp",EDGE,"E13.11.0");var subQ2=makeQuery(id+"F0.imprint","INTERSECT",VERTEX,{"disambiguationData":[OD(0.0)],"derivedFrom":[subQ1,subQ0]});Q205=makeQuery(id+"F0.imprint","IMPRINT",FACE,{"disambiguationData":[TD([[makeQuery(id+"F0.imprint","IMPRINT",EDGE,{"disambiguationData":[TD([[subQ2,-1.0]])],"derivedFrom":subQ1}),1.0]])]});}
            var Q206;
            {var subQ0=sQuery(id+"F0.wireOp",EDGE,"E29.trimOffspring");var subQ1=sQuery(id+"F0.wireOp",EDGE,"E13.11.0");var subQ2=makeQuery(id+"F0.imprint","INTERSECT",VERTEX,{"disambiguationData":[OD(1.0)],"derivedFrom":[subQ1,subQ0]});Q206=makeQuery(id+"F0.imprint","IMPRINT",FACE,{"disambiguationData":[TD([[makeQuery(id+"F0.imprint","IMPRINT",EDGE,{"disambiguationData":[TD([[subQ2,1.0]])],"derivedFrom":subQ1}),1.0]])]});}
            var Q207;
            {var subQ0=sQuery(id+"F0.wireOp",EDGE,"E28.trimOffspring");var subQ1=sQuery(id+"F0.wireOp",EDGE,"E13.12.0");var subQ2=makeQuery(id+"F0.imprint","INTERSECT",VERTEX,{"disambiguationData":[OD(0.0)],"derivedFrom":[subQ1,subQ0]});Q207=makeQuery(id+"F0.imprint","IMPRINT",FACE,{"disambiguationData":[TD([[makeQuery(id+"F0.imprint","IMPRINT",EDGE,{"disambiguationData":[TD([[subQ2,-1.0]])],"derivedFrom":subQ1}),-1.0]])]});}
            var Q208;
            {var subQ0=sQuery(id+"F0.wireOp",EDGE,"E28.trimOffspring");var subQ1=sQuery(id+"F0.wireOp",EDGE,"E13.12.0");var subQ2=makeQuery(id+"F0.imprint","INTERSECT",VERTEX,{"disambiguationData":[OD(0.0)],"derivedFrom":[subQ1,subQ0]});Q208=makeQuery(id+"F0.imprint","IMPRINT",FACE,{"disambiguationData":[TD([[makeQuery(id+"F0.imprint","IMPRINT",EDGE,{"disambiguationData":[TD([[subQ2,-1.0]])],"derivedFrom":subQ1}),1.0]])]});}
            var Q209;
            {var subQ0=sQuery(id+"F0.wireOp",EDGE,"E28.trimOffspring");var subQ1=sQuery(id+"F0.wireOp",EDGE,"E13.12.0");var subQ2=makeQuery(id+"F0.imprint","INTERSECT",VERTEX,{"disambiguationData":[OD(1.0)],"derivedFrom":[subQ1,subQ0]});Q209=makeQuery(id+"F0.imprint","IMPRINT",FACE,{"disambiguationData":[TD([[makeQuery(id+"F0.imprint","IMPRINT",EDGE,{"disambiguationData":[TD([[subQ2,1.0]])],"derivedFrom":subQ1}),1.0]])]});}
            var Q210;
            {var subQ0=sQuery(id+"F0.wireOp",EDGE,"E27.trimOffspring");var subQ1=sQuery(id+"F0.wireOp",EDGE,"E13.13.0");var subQ2=makeQuery(id+"F0.imprint","INTERSECT",VERTEX,{"disambiguationData":[OD(0.0)],"derivedFrom":[subQ1,subQ0]});Q210=makeQuery(id+"F0.imprint","IMPRINT",FACE,{"disambiguationData":[TD([[makeQuery(id+"F0.imprint","IMPRINT",EDGE,{"disambiguationData":[TD([[subQ2,-1.0]])],"derivedFrom":subQ1}),-1.0]])]});}
            var Q211;
            {var subQ0=sQuery(id+"F0.wireOp",EDGE,"E27.trimOffspring");var subQ1=sQuery(id+"F0.wireOp",EDGE,"E13.13.0");var subQ2=makeQuery(id+"F0.imprint","INTERSECT",VERTEX,{"disambiguationData":[OD(0.0)],"derivedFrom":[subQ1,subQ0]});Q211=makeQuery(id+"F0.imprint","IMPRINT",FACE,{"disambiguationData":[TD([[makeQuery(id+"F0.imprint","IMPRINT",EDGE,{"disambiguationData":[TD([[subQ2,-1.0]])],"derivedFrom":subQ1}),1.0]])]});}
            var Q212;
            {var subQ0=sQuery(id+"F0.wireOp",EDGE,"E27.trimOffspring");var subQ1=sQuery(id+"F0.wireOp",EDGE,"E13.13.0");var subQ2=makeQuery(id+"F0.imprint","INTERSECT",VERTEX,{"disambiguationData":[OD(1.0)],"derivedFrom":[subQ1,subQ0]});Q212=makeQuery(id+"F0.imprint","IMPRINT",FACE,{"disambiguationData":[TD([[makeQuery(id+"F0.imprint","IMPRINT",EDGE,{"disambiguationData":[TD([[subQ2,1.0]])],"derivedFrom":subQ1}),1.0]])]});}
            var Q213;
            {var subQ0=sQuery(id+"F0.wireOp",EDGE,"E26.trimOffspring");var subQ1=sQuery(id+"F0.wireOp",EDGE,"E13.14.0");var subQ2=makeQuery(id+"F0.imprint","INTERSECT",VERTEX,{"disambiguationData":[OD(0.0)],"derivedFrom":[subQ1,subQ0]});Q213=makeQuery(id+"F0.imprint","IMPRINT",FACE,{"disambiguationData":[TD([[makeQuery(id+"F0.imprint","IMPRINT",EDGE,{"disambiguationData":[TD([[subQ2,-1.0]])],"derivedFrom":subQ1}),-1.0]])]});}
            var Q214;
            {var subQ0=sQuery(id+"F0.wireOp",EDGE,"E26.trimOffspring");var subQ1=sQuery(id+"F0.wireOp",EDGE,"E13.14.0");var subQ2=makeQuery(id+"F0.imprint","INTERSECT",VERTEX,{"disambiguationData":[OD(0.0)],"derivedFrom":[subQ1,subQ0]});Q214=makeQuery(id+"F0.imprint","IMPRINT",FACE,{"disambiguationData":[TD([[makeQuery(id+"F0.imprint","IMPRINT",EDGE,{"disambiguationData":[TD([[subQ2,-1.0]])],"derivedFrom":subQ1}),1.0]])]});}
            var Q215;
            {var subQ0=sQuery(id+"F0.wireOp",EDGE,"E26.trimOffspring");var subQ1=sQuery(id+"F0.wireOp",EDGE,"E13.14.0");var subQ2=makeQuery(id+"F0.imprint","INTERSECT",VERTEX,{"disambiguationData":[OD(1.0)],"derivedFrom":[subQ1,subQ0]});Q215=makeQuery(id+"F0.imprint","IMPRINT",FACE,{"disambiguationData":[TD([[makeQuery(id+"F0.imprint","IMPRINT",EDGE,{"disambiguationData":[TD([[subQ2,1.0]])],"derivedFrom":subQ1}),1.0]])]});}
            var Q216;
            {var subQ0=sQuery(id+"F0.wireOp",EDGE,"E25.trimOffspring");var subQ1=sQuery(id+"F0.wireOp",EDGE,"E13.15.0");var subQ2=makeQuery(id+"F0.imprint","INTERSECT",VERTEX,{"disambiguationData":[OD(0.0)],"derivedFrom":[subQ1,subQ0]});Q216=makeQuery(id+"F0.imprint","IMPRINT",FACE,{"disambiguationData":[TD([[makeQuery(id+"F0.imprint","IMPRINT",EDGE,{"disambiguationData":[TD([[subQ2,-1.0]])],"derivedFrom":subQ1}),-1.0]])]});}
            var Q217;
            {var subQ0=sQuery(id+"F0.wireOp",EDGE,"E25.trimOffspring");var subQ1=sQuery(id+"F0.wireOp",EDGE,"E13.15.0");var subQ2=makeQuery(id+"F0.imprint","INTERSECT",VERTEX,{"disambiguationData":[OD(0.0)],"derivedFrom":[subQ1,subQ0]});Q217=makeQuery(id+"F0.imprint","IMPRINT",FACE,{"disambiguationData":[TD([[makeQuery(id+"F0.imprint","IMPRINT",EDGE,{"disambiguationData":[TD([[subQ2,-1.0]])],"derivedFrom":subQ1}),1.0]])]});}
            var Q218;
            {var subQ0=sQuery(id+"F0.wireOp",EDGE,"E25.trimOffspring");var subQ1=sQuery(id+"F0.wireOp",EDGE,"E13.15.0");var subQ2=makeQuery(id+"F0.imprint","INTERSECT",VERTEX,{"disambiguationData":[OD(1.0)],"derivedFrom":[subQ1,subQ0]});Q218=makeQuery(id+"F0.imprint","IMPRINT",FACE,{"disambiguationData":[TD([[makeQuery(id+"F0.imprint","IMPRINT",EDGE,{"disambiguationData":[TD([[subQ2,1.0]])],"derivedFrom":subQ1}),1.0]])]});}
            var Q219;
            {var subQ0=sQuery(id+"F0.wireOp",EDGE,"E24.trimOffspring");var subQ1=sQuery(id+"F0.wireOp",EDGE,"E13.16.0");var subQ2=makeQuery(id+"F0.imprint","INTERSECT",VERTEX,{"disambiguationData":[OD(0.0)],"derivedFrom":[subQ1,subQ0]});Q219=makeQuery(id+"F0.imprint","IMPRINT",FACE,{"disambiguationData":[TD([[makeQuery(id+"F0.imprint","IMPRINT",EDGE,{"disambiguationData":[TD([[subQ2,-1.0]])],"derivedFrom":subQ1}),-1.0]])]});}
            var Q220;
            {var subQ0=sQuery(id+"F0.wireOp",EDGE,"E24.trimOffspring");var subQ1=sQuery(id+"F0.wireOp",EDGE,"E13.16.0");var subQ2=makeQuery(id+"F0.imprint","INTERSECT",VERTEX,{"disambiguationData":[OD(0.0)],"derivedFrom":[subQ1,subQ0]});Q220=makeQuery(id+"F0.imprint","IMPRINT",FACE,{"disambiguationData":[TD([[makeQuery(id+"F0.imprint","IMPRINT",EDGE,{"disambiguationData":[TD([[subQ2,-1.0]])],"derivedFrom":subQ1}),1.0]])]});}
            var Q221;
            {var subQ0=sQuery(id+"F0.wireOp",EDGE,"E24.trimOffspring");var subQ1=sQuery(id+"F0.wireOp",EDGE,"E13.16.0");var subQ2=makeQuery(id+"F0.imprint","INTERSECT",VERTEX,{"disambiguationData":[OD(1.0)],"derivedFrom":[subQ1,subQ0]});Q221=makeQuery(id+"F0.imprint","IMPRINT",FACE,{"disambiguationData":[TD([[makeQuery(id+"F0.imprint","IMPRINT",EDGE,{"disambiguationData":[TD([[subQ2,1.0]])],"derivedFrom":subQ1}),1.0]])]});}
            var Q222;
            {var subQ0=sQuery(id+"F0.wireOp",EDGE,"E23.trimOffspring");var subQ1=sQuery(id+"F0.wireOp",EDGE,"E13.17.0");var subQ2=makeQuery(id+"F0.imprint","INTERSECT",VERTEX,{"disambiguationData":[OD(0.0)],"derivedFrom":[subQ1,subQ0]});Q222=makeQuery(id+"F0.imprint","IMPRINT",FACE,{"disambiguationData":[TD([[makeQuery(id+"F0.imprint","IMPRINT",EDGE,{"disambiguationData":[TD([[subQ2,-1.0]])],"derivedFrom":subQ1}),-1.0]])]});}
            var Q223;
            {var subQ0=sQuery(id+"F0.wireOp",EDGE,"E23.trimOffspring");var subQ1=sQuery(id+"F0.wireOp",EDGE,"E13.17.0");var subQ2=makeQuery(id+"F0.imprint","INTERSECT",VERTEX,{"disambiguationData":[OD(0.0)],"derivedFrom":[subQ1,subQ0]});Q223=makeQuery(id+"F0.imprint","IMPRINT",FACE,{"disambiguationData":[TD([[makeQuery(id+"F0.imprint","IMPRINT",EDGE,{"disambiguationData":[TD([[subQ2,-1.0]])],"derivedFrom":subQ1}),1.0]])]});}
            var Q224;
            {var subQ0=sQuery(id+"F0.wireOp",EDGE,"E23.trimOffspring");var subQ1=sQuery(id+"F0.wireOp",EDGE,"E13.17.0");var subQ2=makeQuery(id+"F0.imprint","INTERSECT",VERTEX,{"disambiguationData":[OD(1.0)],"derivedFrom":[subQ1,subQ0]});Q224=makeQuery(id+"F0.imprint","IMPRINT",FACE,{"disambiguationData":[TD([[makeQuery(id+"F0.imprint","IMPRINT",EDGE,{"disambiguationData":[TD([[subQ2,1.0]])],"derivedFrom":subQ1}),1.0]])]});}
            var Q225;
            {var subQ0=sQuery(id+"F0.wireOp",EDGE,"E21.trimOffspring");var subQ1=sQuery(id+"F0.wireOp",EDGE,"E13.18.0");var subQ2=makeQuery(id+"F0.imprint","INTERSECT",VERTEX,{"disambiguationData":[OD(0.0)],"derivedFrom":[subQ1,subQ0]});Q225=makeQuery(id+"F0.imprint","IMPRINT",FACE,{"disambiguationData":[TD([[makeQuery(id+"F0.imprint","IMPRINT",EDGE,{"disambiguationData":[TD([[subQ2,-1.0]])],"derivedFrom":subQ1}),-1.0]])]});}
            var Q226;
            {var subQ0=sQuery(id+"F0.wireOp",EDGE,"E21.trimOffspring");var subQ1=sQuery(id+"F0.wireOp",EDGE,"E13.18.0");var subQ2=makeQuery(id+"F0.imprint","INTERSECT",VERTEX,{"disambiguationData":[OD(0.0)],"derivedFrom":[subQ1,subQ0]});Q226=makeQuery(id+"F0.imprint","IMPRINT",FACE,{"disambiguationData":[TD([[makeQuery(id+"F0.imprint","IMPRINT",EDGE,{"disambiguationData":[TD([[subQ2,-1.0]])],"derivedFrom":subQ1}),1.0]])]});}
            var Q227;
            {var subQ0=sQuery(id+"F0.wireOp",EDGE,"E21.trimOffspring");var subQ1=sQuery(id+"F0.wireOp",EDGE,"E13.18.0");var subQ2=makeQuery(id+"F0.imprint","INTERSECT",VERTEX,{"disambiguationData":[OD(1.0)],"derivedFrom":[subQ1,subQ0]});Q227=makeQuery(id+"F0.imprint","IMPRINT",FACE,{"disambiguationData":[TD([[makeQuery(id+"F0.imprint","IMPRINT",EDGE,{"disambiguationData":[TD([[subQ2,1.0]])],"derivedFrom":subQ1}),1.0]])]});}
            var Q228;
            {var subQ0=sQuery(id+"F0.wireOp",EDGE,"E22.trimOffspring");var subQ1=sQuery(id+"F0.wireOp",EDGE,"E13.19.0");var subQ2=makeQuery(id+"F0.imprint","INTERSECT",VERTEX,{"disambiguationData":[OD(0.0)],"derivedFrom":[subQ1,subQ0]});Q228=makeQuery(id+"F0.imprint","IMPRINT",FACE,{"disambiguationData":[TD([[makeQuery(id+"F0.imprint","IMPRINT",EDGE,{"disambiguationData":[TD([[subQ2,-1.0]])],"derivedFrom":subQ1}),-1.0]])]});}
            var Q229;
            {var subQ0=sQuery(id+"F0.wireOp",EDGE,"E22.trimOffspring");var subQ1=sQuery(id+"F0.wireOp",EDGE,"E13.19.0");var subQ2=makeQuery(id+"F0.imprint","INTERSECT",VERTEX,{"disambiguationData":[OD(0.0)],"derivedFrom":[subQ1,subQ0]});Q229=makeQuery(id+"F0.imprint","IMPRINT",FACE,{"disambiguationData":[TD([[makeQuery(id+"F0.imprint","IMPRINT",EDGE,{"disambiguationData":[TD([[subQ2,-1.0]])],"derivedFrom":subQ1}),1.0]])]});}
            var Q230;
            {var subQ0=sQuery(id+"F0.wireOp",EDGE,"E22.trimOffspring");var subQ1=sQuery(id+"F0.wireOp",EDGE,"E13.19.0");var subQ2=makeQuery(id+"F0.imprint","INTERSECT",VERTEX,{"disambiguationData":[OD(1.0)],"derivedFrom":[subQ1,subQ0]});Q230=makeQuery(id+"F0.imprint","IMPRINT",FACE,{"disambiguationData":[TD([[makeQuery(id+"F0.imprint","IMPRINT",EDGE,{"disambiguationData":[TD([[subQ2,1.0]])],"derivedFrom":subQ1}),1.0]])]});}
            var Q231;
            {var subQ0=sQuery(id+"F0.wireOp",EDGE,"E20.trimOffspring");var subQ1=sQuery(id+"F0.wireOp",EDGE,"E13.20.0");var subQ2=makeQuery(id+"F0.imprint","INTERSECT",VERTEX,{"disambiguationData":[OD(0.0)],"derivedFrom":[subQ1,subQ0]});Q231=makeQuery(id+"F0.imprint","IMPRINT",FACE,{"disambiguationData":[TD([[makeQuery(id+"F0.imprint","IMPRINT",EDGE,{"disambiguationData":[TD([[subQ2,-1.0]])],"derivedFrom":subQ1}),-1.0]])]});}
            var Q232;
            {var subQ0=sQuery(id+"F0.wireOp",EDGE,"E20.trimOffspring");var subQ1=sQuery(id+"F0.wireOp",EDGE,"E13.20.0");var subQ2=makeQuery(id+"F0.imprint","INTERSECT",VERTEX,{"disambiguationData":[OD(0.0)],"derivedFrom":[subQ1,subQ0]});Q232=makeQuery(id+"F0.imprint","IMPRINT",FACE,{"disambiguationData":[TD([[makeQuery(id+"F0.imprint","IMPRINT",EDGE,{"disambiguationData":[TD([[subQ2,-1.0]])],"derivedFrom":subQ1}),1.0]])]});}
            var Q233;
            {var subQ0=sQuery(id+"F0.wireOp",EDGE,"E20.trimOffspring");var subQ1=sQuery(id+"F0.wireOp",EDGE,"E13.20.0");var subQ2=makeQuery(id+"F0.imprint","INTERSECT",VERTEX,{"disambiguationData":[OD(1.0)],"derivedFrom":[subQ1,subQ0]});Q233=makeQuery(id+"F0.imprint","IMPRINT",FACE,{"disambiguationData":[TD([[makeQuery(id+"F0.imprint","IMPRINT",EDGE,{"disambiguationData":[TD([[subQ2,1.0]])],"derivedFrom":subQ1}),1.0]])]});}
            var Q234;
            {var subQ0=sQuery(id+"F0.wireOp",EDGE,"E19.trimOffspring");var subQ1=sQuery(id+"F0.wireOp",EDGE,"E13.21.0");var subQ2=makeQuery(id+"F0.imprint","INTERSECT",VERTEX,{"disambiguationData":[OD(0.0)],"derivedFrom":[subQ1,subQ0]});Q234=makeQuery(id+"F0.imprint","IMPRINT",FACE,{"disambiguationData":[TD([[makeQuery(id+"F0.imprint","IMPRINT",EDGE,{"disambiguationData":[TD([[subQ2,-1.0]])],"derivedFrom":subQ1}),-1.0]])]});}
            var Q235;
            {var subQ0=sQuery(id+"F0.wireOp",EDGE,"E19.trimOffspring");var subQ1=sQuery(id+"F0.wireOp",EDGE,"E13.21.0");var subQ2=makeQuery(id+"F0.imprint","INTERSECT",VERTEX,{"disambiguationData":[OD(0.0)],"derivedFrom":[subQ1,subQ0]});Q235=makeQuery(id+"F0.imprint","IMPRINT",FACE,{"disambiguationData":[TD([[makeQuery(id+"F0.imprint","IMPRINT",EDGE,{"disambiguationData":[TD([[subQ2,-1.0]])],"derivedFrom":subQ1}),1.0]])]});}
            var Q236;
            {var subQ0=sQuery(id+"F0.wireOp",EDGE,"E19.trimOffspring");var subQ1=sQuery(id+"F0.wireOp",EDGE,"E13.21.0");var subQ2=makeQuery(id+"F0.imprint","INTERSECT",VERTEX,{"disambiguationData":[OD(1.0)],"derivedFrom":[subQ1,subQ0]});Q236=makeQuery(id+"F0.imprint","IMPRINT",FACE,{"disambiguationData":[TD([[makeQuery(id+"F0.imprint","IMPRINT",EDGE,{"disambiguationData":[TD([[subQ2,1.0]])],"derivedFrom":subQ1}),1.0]])]});}
            var Q237;
            {var subQ0=sQuery(id+"F0.wireOp",EDGE,"E18.trimOffspring");var subQ1=sQuery(id+"F0.wireOp",EDGE,"E13.22.0");var subQ2=makeQuery(id+"F0.imprint","INTERSECT",VERTEX,{"disambiguationData":[OD(0.0)],"derivedFrom":[subQ1,subQ0]});Q237=makeQuery(id+"F0.imprint","IMPRINT",FACE,{"disambiguationData":[TD([[makeQuery(id+"F0.imprint","IMPRINT",EDGE,{"disambiguationData":[TD([[subQ2,-1.0]])],"derivedFrom":subQ1}),-1.0]])]});}
            var Q238;
            {var subQ0=sQuery(id+"F0.wireOp",EDGE,"E18.trimOffspring");var subQ1=sQuery(id+"F0.wireOp",EDGE,"E13.22.0");var subQ2=makeQuery(id+"F0.imprint","INTERSECT",VERTEX,{"disambiguationData":[OD(0.0)],"derivedFrom":[subQ1,subQ0]});Q238=makeQuery(id+"F0.imprint","IMPRINT",FACE,{"disambiguationData":[TD([[makeQuery(id+"F0.imprint","IMPRINT",EDGE,{"disambiguationData":[TD([[subQ2,-1.0]])],"derivedFrom":subQ1}),1.0]])]});}
            var Q239;
            {var subQ0=sQuery(id+"F0.wireOp",EDGE,"E18.trimOffspring");var subQ1=sQuery(id+"F0.wireOp",EDGE,"E13.22.0");var subQ2=makeQuery(id+"F0.imprint","INTERSECT",VERTEX,{"disambiguationData":[OD(1.0)],"derivedFrom":[subQ1,subQ0]});Q239=makeQuery(id+"F0.imprint","IMPRINT",FACE,{"disambiguationData":[TD([[makeQuery(id+"F0.imprint","IMPRINT",EDGE,{"disambiguationData":[TD([[subQ2,1.0]])],"derivedFrom":subQ1}),1.0]])]});}
            var Q240;
            {var subQ137=sQuery(id+"F0.wireOp",EDGE,"E1");Q240=makeQuery(id+"F0.imprint","IMPRINT",FACE,{"disambiguationData":[TD([[makeQuery(id+"F0.imprint","IMPRINT",EDGE,{"derivedFrom":subQ137}),1.0]])]});}
            extrude(context, id + "F1", {"entities" : qUnion([Q0, Q1, Q2, Q3, Q4, Q5, Q6, Q7, Q8, Q9, Q10, Q11, Q12, Q13, Q14, Q15, Q16, Q17, Q18, Q19, Q20, Q21, Q22, Q23, Q24, Q25, Q26, Q27, Q28, Q29, Q30, Q31, Q32, Q33, Q34, Q35, Q36, Q37, Q38, Q39, Q40, Q41, Q42, Q43, Q44, Q45, Q46, Q47, Q48, Q49, Q50, Q51, Q52, Q53, Q54, Q55, Q56, Q57, Q58, Q59, Q60, Q61, Q62, Q63, Q64, Q65, Q66, Q67, Q68, Q69, Q70, Q71, Q72, Q73, Q74, Q75, Q76, Q77, Q78, Q79, Q80, Q81, Q82, Q83, Q84, Q85, Q86, Q87, Q88, Q89, Q90, Q91, Q92, Q93, Q94, Q95, Q96, Q97, Q98, Q99, Q100, Q101, Q102, Q103, Q104, Q105, Q106, Q107, Q108, Q109, Q110, Q111, Q112, Q113, Q114, Q115, Q116, Q117, Q118, Q119, Q120, Q121, Q122, Q123, Q124, Q125, Q126, Q127, Q128, Q129, Q130, Q131, Q132, Q133, Q134, Q135, Q136, Q137, Q138, Q139, Q140, Q141, Q142, Q143, Q144, Q145, Q146, Q147, Q148, Q149, Q150, Q151, Q152, Q153, Q154, Q155, Q156, Q157, Q158, Q159, Q160, Q161, Q162, Q163, Q164, Q165, Q166, Q167, Q168, Q169, Q170, Q171, Q172, Q173, Q174, Q175, Q176, Q177, Q178, Q179, Q180, Q181, Q182, Q183, Q184, Q185, Q186, Q187, Q188, Q189, Q190, Q191, Q192, Q193, Q194, Q195, Q196, Q197, Q198, Q199, Q200, Q201, Q202, Q203, Q204, Q205, Q206, Q207, Q208, Q209, Q210, Q211, Q212, Q213, Q214, Q215, Q216, Q217, Q218, Q219, Q220, Q221, Q222, Q223, Q224, Q225, Q226, Q227, Q228, Q229, Q230, Q231, Q232, Q233, Q234, Q235, Q236, Q237, Q238, Q239, Q240]), "depth" : 6.35 * mm});
        }
        {
            var Q0;
            Q0=makeQuery(id+"F1.opExtrude","CAP_FACE",FACE,{"disambiguationData":[OSD([sQuery(id+"F0.wireOp",EDGE,"E0"),sQuery(id+"F0.wireOp",EDGE,"E1"),sQuery(id+"F0.wireOp",EDGE,"E2"),sQuery(id+"F0.wireOp",EDGE,"E3"),sQuery(id+"F0.wireOp",EDGE,"E4.MirrorCS"),sQuery(id+"F0.wireOp",EDGE,"E5.MirrorCS"),sQuery(id+"F0.wireOp",EDGE,"E6.MirrorCS"),sQuery(id+"F0.wireOp",EDGE,"E9.filletArc"),sQuery(id+"F0.wireOp",EDGE,"E10.filletArc"),sQuery(id+"F0.wireOp",EDGE,"E11"),sQuery(id+"F0.wireOp",EDGE,"E12"),sQuery(id+"F0.wireOp",EDGE,"E13.1.0"),sQuery(id+"F0.wireOp",EDGE,"E13.1.1"),sQuery(id+"F0.wireOp",EDGE,"E13.1.3"),sQuery(id+"F0.wireOp",EDGE,"E13.1.4"),sQuery(id+"F0.wireOp",EDGE,"E13.1.5"),sQuery(id+"F0.wireOp",EDGE,"E13.1.6"),sQuery(id+"F0.wireOp",EDGE,"E13.1.7"),sQuery(id+"F0.wireOp",EDGE,"E13.1.8"),sQuery(id+"F0.wireOp",EDGE,"E13.1.9"),sQuery(id+"F0.wireOp",EDGE,"E13.1.10"),sQuery(id+"F0.wireOp",EDGE,"E13.2.0"),sQuery(id+"F0.wireOp",EDGE,"E13.2.1"),sQuery(id+"F0.wireOp",EDGE,"E13.2.3"),sQuery(id+"F0.wireOp",EDGE,"E13.2.4"),sQuery(id+"F0.wireOp",EDGE,"E13.2.5"),sQuery(id+"F0.wireOp",EDGE,"E13.2.6"),sQuery(id+"F0.wireOp",EDGE,"E13.2.7"),sQuery(id+"F0.wireOp",EDGE,"E13.2.8"),sQuery(id+"F0.wireOp",EDGE,"E13.2.9"),sQuery(id+"F0.wireOp",EDGE,"E13.2.10"),sQuery(id+"F0.wireOp",EDGE,"E13.3.0"),sQuery(id+"F0.wireOp",EDGE,"E13.3.1"),sQuery(id+"F0.wireOp",EDGE,"E13.3.3"),sQuery(id+"F0.wireOp",EDGE,"E13.3.4"),sQuery(id+"F0.wireOp",EDGE,"E13.3.5"),sQuery(id+"F0.wireOp",EDGE,"E13.3.6"),sQuery(id+"F0.wireOp",EDGE,"E13.3.7"),sQuery(id+"F0.wireOp",EDGE,"E13.3.8"),sQuery(id+"F0.wireOp",EDGE,"E13.3.9"),sQuery(id+"F0.wireOp",EDGE,"E13.3.10"),sQuery(id+"F0.wireOp",EDGE,"E13.4.0"),sQuery(id+"F0.wireOp",EDGE,"E13.4.1"),sQuery(id+"F0.wireOp",EDGE,"E13.4.3"),sQuery(id+"F0.wireOp",EDGE,"E13.4.4"),sQuery(id+"F0.wireOp",EDGE,"E13.4.5"),sQuery(id+"F0.wireOp",EDGE,"E13.4.6"),sQuery(id+"F0.wireOp",EDGE,"E13.4.7"),sQuery(id+"F0.wireOp",EDGE,"E13.4.8"),sQuery(id+"F0.wireOp",EDGE,"E13.4.9"),sQuery(id+"F0.wireOp",EDGE,"E13.4.10"),sQuery(id+"F0.wireOp",EDGE,"E13.5.0"),sQuery(id+"F0.wireOp",EDGE,"E13.5.1"),sQuery(id+"F0.wireOp",EDGE,"E13.5.3"),sQuery(id+"F0.wireOp",EDGE,"E13.5.4"),sQuery(id+"F0.wireOp",EDGE,"E13.5.5"),sQuery(id+"F0.wireOp",EDGE,"E13.5.6"),sQuery(id+"F0.wireOp",EDGE,"E13.5.7"),sQuery(id+"F0.wireOp",EDGE,"E13.5.8"),sQuery(id+"F0.wireOp",EDGE,"E13.5.9"),sQuery(id+"F0.wireOp",EDGE,"E13.5.10"),sQuery(id+"F0.wireOp",EDGE,"E13.6.0"),sQuery(id+"F0.wireOp",EDGE,"E13.6.1"),sQuery(id+"F0.wireOp",EDGE,"E13.6.3"),sQuery(id+"F0.wireOp",EDGE,"E13.6.4"),sQuery(id+"F0.wireOp",EDGE,"E13.6.5"),sQuery(id+"F0.wireOp",EDGE,"E13.6.6"),sQuery(id+"F0.wireOp",EDGE,"E13.6.7"),sQuery(id+"F0.wireOp",EDGE,"E13.6.8"),sQuery(id+"F0.wireOp",EDGE,"E13.6.9"),sQuery(id+"F0.wireOp",EDGE,"E13.6.10"),sQuery(id+"F0.wireOp",EDGE,"E13.7.0"),sQuery(id+"F0.wireOp",EDGE,"E13.7.1"),sQuery(id+"F0.wireOp",EDGE,"E13.7.3"),sQuery(id+"F0.wireOp",EDGE,"E13.7.4"),sQuery(id+"F0.wireOp",EDGE,"E13.7.5"),sQuery(id+"F0.wireOp",EDGE,"E13.7.6"),sQuery(id+"F0.wireOp",EDGE,"E13.7.7"),sQuery(id+"F0.wireOp",EDGE,"E13.7.8"),sQuery(id+"F0.wireOp",EDGE,"E13.7.9"),sQuery(id+"F0.wireOp",EDGE,"E13.7.10"),sQuery(id+"F0.wireOp",EDGE,"E13.8.0"),sQuery(id+"F0.wireOp",EDGE,"E13.8.1"),sQuery(id+"F0.wireOp",EDGE,"E13.8.3"),sQuery(id+"F0.wireOp",EDGE,"E13.8.4"),sQuery(id+"F0.wireOp",EDGE,"E13.8.5"),sQuery(id+"F0.wireOp",EDGE,"E13.8.6"),sQuery(id+"F0.wireOp",EDGE,"E13.8.7"),sQuery(id+"F0.wireOp",EDGE,"E13.8.8"),sQuery(id+"F0.wireOp",EDGE,"E13.8.9"),sQuery(id+"F0.wireOp",EDGE,"E13.8.10"),sQuery(id+"F0.wireOp",EDGE,"E13.9.0"),sQuery(id+"F0.wireOp",EDGE,"E13.9.1"),sQuery(id+"F0.wireOp",EDGE,"E13.9.3"),sQuery(id+"F0.wireOp",EDGE,"E13.9.4"),sQuery(id+"F0.wireOp",EDGE,"E13.9.5"),sQuery(id+"F0.wireOp",EDGE,"E13.9.6"),sQuery(id+"F0.wireOp",EDGE,"E13.9.7"),sQuery(id+"F0.wireOp",EDGE,"E13.9.8"),sQuery(id+"F0.wireOp",EDGE,"E13.9.9"),sQuery(id+"F0.wireOp",EDGE,"E13.9.10"),sQuery(id+"F0.wireOp",EDGE,"E13.10.0"),sQuery(id+"F0.wireOp",EDGE,"E13.10.1"),sQuery(id+"F0.wireOp",EDGE,"E13.10.3"),sQuery(id+"F0.wireOp",EDGE,"E13.10.4"),sQuery(id+"F0.wireOp",EDGE,"E13.10.5"),sQuery(id+"F0.wireOp",EDGE,"E13.10.6"),sQuery(id+"F0.wireOp",EDGE,"E13.10.7"),sQuery(id+"F0.wireOp",EDGE,"E13.10.8"),sQuery(id+"F0.wireOp",EDGE,"E13.10.9"),sQuery(id+"F0.wireOp",EDGE,"E13.10.10"),sQuery(id+"F0.wireOp",EDGE,"E13.11.0"),sQuery(id+"F0.wireOp",EDGE,"E13.11.1"),sQuery(id+"F0.wireOp",EDGE,"E13.11.3"),sQuery(id+"F0.wireOp",EDGE,"E13.11.4"),sQuery(id+"F0.wireOp",EDGE,"E13.11.5"),sQuery(id+"F0.wireOp",EDGE,"E13.11.6"),sQuery(id+"F0.wireOp",EDGE,"E13.11.7"),sQuery(id+"F0.wireOp",EDGE,"E13.11.8"),sQuery(id+"F0.wireOp",EDGE,"E13.11.9"),sQuery(id+"F0.wireOp",EDGE,"E13.11.10"),sQuery(id+"F0.wireOp",EDGE,"E13.12.0"),sQuery(id+"F0.wireOp",EDGE,"E13.12.1"),sQuery(id+"F0.wireOp",EDGE,"E13.12.3"),sQuery(id+"F0.wireOp",EDGE,"E13.12.4"),sQuery(id+"F0.wireOp",EDGE,"E13.12.5"),sQuery(id+"F0.wireOp",EDGE,"E13.12.6"),sQuery(id+"F0.wireOp",EDGE,"E13.12.7"),sQuery(id+"F0.wireOp",EDGE,"E13.12.8"),sQuery(id+"F0.wireOp",EDGE,"E13.12.9"),sQuery(id+"F0.wireOp",EDGE,"E13.12.10"),sQuery(id+"F0.wireOp",EDGE,"E13.13.0"),sQuery(id+"F0.wireOp",EDGE,"E13.13.1"),sQuery(id+"F0.wireOp",EDGE,"E13.13.3"),sQuery(id+"F0.wireOp",EDGE,"E13.13.4"),sQuery(id+"F0.wireOp",EDGE,"E13.13.5"),sQuery(id+"F0.wireOp",EDGE,"E13.13.6"),sQuery(id+"F0.wireOp",EDGE,"E13.13.7"),sQuery(id+"F0.wireOp",EDGE,"E13.13.8"),sQuery(id+"F0.wireOp",EDGE,"E13.13.9"),sQuery(id+"F0.wireOp",EDGE,"E13.13.10"),sQuery(id+"F0.wireOp",EDGE,"E13.14.0"),sQuery(id+"F0.wireOp",EDGE,"E13.14.1"),sQuery(id+"F0.wireOp",EDGE,"E13.14.3"),sQuery(id+"F0.wireOp",EDGE,"E13.14.4"),sQuery(id+"F0.wireOp",EDGE,"E13.14.5"),sQuery(id+"F0.wireOp",EDGE,"E13.14.6"),sQuery(id+"F0.wireOp",EDGE,"E13.14.7"),sQuery(id+"F0.wireOp",EDGE,"E13.14.8"),sQuery(id+"F0.wireOp",EDGE,"E13.14.9"),sQuery(id+"F0.wireOp",EDGE,"E13.14.10"),sQuery(id+"F0.wireOp",EDGE,"E13.15.0"),sQuery(id+"F0.wireOp",EDGE,"E13.15.1"),sQuery(id+"F0.wireOp",EDGE,"E13.15.3"),sQuery(id+"F0.wireOp",EDGE,"E13.15.4"),sQuery(id+"F0.wireOp",EDGE,"E13.15.5"),sQuery(id+"F0.wireOp",EDGE,"E13.15.6"),sQuery(id+"F0.wireOp",EDGE,"E13.15.7"),sQuery(id+"F0.wireOp",EDGE,"E13.15.8"),sQuery(id+"F0.wireOp",EDGE,"E13.15.9"),sQuery(id+"F0.wireOp",EDGE,"E13.15.10"),sQuery(id+"F0.wireOp",EDGE,"E13.16.0"),sQuery(id+"F0.wireOp",EDGE,"E13.16.1"),sQuery(id+"F0.wireOp",EDGE,"E13.16.3"),sQuery(id+"F0.wireOp",EDGE,"E13.16.4"),sQuery(id+"F0.wireOp",EDGE,"E13.16.5"),sQuery(id+"F0.wireOp",EDGE,"E13.16.6"),sQuery(id+"F0.wireOp",EDGE,"E13.16.7"),sQuery(id+"F0.wireOp",EDGE,"E13.16.8"),sQuery(id+"F0.wireOp",EDGE,"E13.16.9"),sQuery(id+"F0.wireOp",EDGE,"E13.16.10"),sQuery(id+"F0.wireOp",EDGE,"E13.17.0"),sQuery(id+"F0.wireOp",EDGE,"E13.17.1"),sQuery(id+"F0.wireOp",EDGE,"E13.17.3"),sQuery(id+"F0.wireOp",EDGE,"E13.17.4"),sQuery(id+"F0.wireOp",EDGE,"E13.17.5"),sQuery(id+"F0.wireOp",EDGE,"E13.17.6"),sQuery(id+"F0.wireOp",EDGE,"E13.17.7"),sQuery(id+"F0.wireOp",EDGE,"E13.17.8"),sQuery(id+"F0.wireOp",EDGE,"E13.17.9"),sQuery(id+"F0.wireOp",EDGE,"E13.17.10"),sQuery(id+"F0.wireOp",EDGE,"E13.18.0"),sQuery(id+"F0.wireOp",EDGE,"E13.18.1"),sQuery(id+"F0.wireOp",EDGE,"E13.18.3"),sQuery(id+"F0.wireOp",EDGE,"E13.18.4"),sQuery(id+"F0.wireOp",EDGE,"E13.18.5"),sQuery(id+"F0.wireOp",EDGE,"E13.18.6"),sQuery(id+"F0.wireOp",EDGE,"E13.18.7"),sQuery(id+"F0.wireOp",EDGE,"E13.18.8"),sQuery(id+"F0.wireOp",EDGE,"E13.18.9"),sQuery(id+"F0.wireOp",EDGE,"E13.18.10"),sQuery(id+"F0.wireOp",EDGE,"E13.19.0"),sQuery(id+"F0.wireOp",EDGE,"E13.19.1"),sQuery(id+"F0.wireOp",EDGE,"E13.19.3"),sQuery(id+"F0.wireOp",EDGE,"E13.19.4"),sQuery(id+"F0.wireOp",EDGE,"E13.19.5"),sQuery(id+"F0.wireOp",EDGE,"E13.19.6"),sQuery(id+"F0.wireOp",EDGE,"E13.19.7"),sQuery(id+"F0.wireOp",EDGE,"E13.19.8"),sQuery(id+"F0.wireOp",EDGE,"E13.19.9"),sQuery(id+"F0.wireOp",EDGE,"E13.19.10"),sQuery(id+"F0.wireOp",EDGE,"E13.20.0"),sQuery(id+"F0.wireOp",EDGE,"E13.20.1"),sQuery(id+"F0.wireOp",EDGE,"E13.20.3"),sQuery(id+"F0.wireOp",EDGE,"E13.20.4"),sQuery(id+"F0.wireOp",EDGE,"E13.20.5"),sQuery(id+"F0.wireOp",EDGE,"E13.20.6"),sQuery(id+"F0.wireOp",EDGE,"E13.20.7"),sQuery(id+"F0.wireOp",EDGE,"E13.20.8"),sQuery(id+"F0.wireOp",EDGE,"E13.20.9"),sQuery(id+"F0.wireOp",EDGE,"E13.20.10"),sQuery(id+"F0.wireOp",EDGE,"E13.21.0"),sQuery(id+"F0.wireOp",EDGE,"E13.21.1"),sQuery(id+"F0.wireOp",EDGE,"E13.21.3"),sQuery(id+"F0.wireOp",EDGE,"E13.21.4"),sQuery(id+"F0.wireOp",EDGE,"E13.21.5"),sQuery(id+"F0.wireOp",EDGE,"E13.21.6"),sQuery(id+"F0.wireOp",EDGE,"E13.21.7"),sQuery(id+"F0.wireOp",EDGE,"E13.21.8"),sQuery(id+"F0.wireOp",EDGE,"E13.21.9"),sQuery(id+"F0.wireOp",EDGE,"E13.21.10"),sQuery(id+"F0.wireOp",EDGE,"E13.22.0"),sQuery(id+"F0.wireOp",EDGE,"E13.22.1"),sQuery(id+"F0.wireOp",EDGE,"E13.22.3"),sQuery(id+"F0.wireOp",EDGE,"E13.22.4"),sQuery(id+"F0.wireOp",EDGE,"E13.22.5"),sQuery(id+"F0.wireOp",EDGE,"E13.22.6"),sQuery(id+"F0.wireOp",EDGE,"E13.22.7"),sQuery(id+"F0.wireOp",EDGE,"E13.22.8"),sQuery(id+"F0.wireOp",EDGE,"E13.22.9"),sQuery(id+"F0.wireOp",EDGE,"E13.22.10"),sQuery(id+"F0.wireOp",EDGE,"E13.23.0"),sQuery(id+"F0.wireOp",EDGE,"E13.23.1"),sQuery(id+"F0.wireOp",EDGE,"E13.23.3"),sQuery(id+"F0.wireOp",EDGE,"E13.23.4"),sQuery(id+"F0.wireOp",EDGE,"E13.23.5"),sQuery(id+"F0.wireOp",EDGE,"E13.23.6"),sQuery(id+"F0.wireOp",EDGE,"E13.23.7"),sQuery(id+"F0.wireOp",EDGE,"E13.23.8"),sQuery(id+"F0.wireOp",EDGE,"E13.23.9"),sQuery(id+"F0.wireOp",EDGE,"E13.23.10"),sQuery(id+"F0.wireOp",EDGE,"E14.trimOffspring"),sQuery(id+"F0.wireOp",EDGE,"E15.trimOffspring"),sQuery(id+"F0.wireOp",EDGE,"E16.trimOffspring"),sQuery(id+"F0.wireOp",EDGE,"E17.trimOffspring"),sQuery(id+"F0.wireOp",EDGE,"E18.trimOffspring"),sQuery(id+"F0.wireOp",EDGE,"E19.trimOffspring"),sQuery(id+"F0.wireOp",EDGE,"E20.trimOffspring"),sQuery(id+"F0.wireOp",EDGE,"E21.trimOffspring"),sQuery(id+"F0.wireOp",EDGE,"E22.trimOffspring"),sQuery(id+"F0.wireOp",EDGE,"E23.trimOffspring"),sQuery(id+"F0.wireOp",EDGE,"E24.trimOffspring"),sQuery(id+"F0.wireOp",EDGE,"E25.trimOffspring"),sQuery(id+"F0.wireOp",EDGE,"E26.trimOffspring"),sQuery(id+"F0.wireOp",EDGE,"E27.trimOffspring"),sQuery(id+"F0.wireOp",EDGE,"E28.trimOffspring"),sQuery(id+"F0.wireOp",EDGE,"E29.trimOffspring"),sQuery(id+"F0.wireOp",EDGE,"E30.trimOffspring"),sQuery(id+"F0.wireOp",EDGE,"E31.trimOffspring"),sQuery(id+"F0.wireOp",EDGE,"E32.trimOffspring"),sQuery(id+"F0.wireOp",EDGE,"E33.trimOffspring"),sQuery(id+"F0.wireOp",EDGE,"E34.trimOffspring"),sQuery(id+"F0.wireOp",EDGE,"E35.trimOffspring"),sQuery(id+"F0.wireOp",EDGE,"E36.trimOffspring"),sQuery(id+"F0.wireOp",EDGE,"E37"),sQuery(id+"F0.wireOp",EDGE,"E38"),sQuery(id+"F0.wireOp",EDGE,"E39"),sQuery(id+"F0.wireOp",EDGE,"E40.MirrorCS"),sQuery(id+"F0.wireOp",EDGE,"E41.1.0"),sQuery(id+"F0.wireOp",EDGE,"E41.1.1"),sQuery(id+"F0.wireOp",EDGE,"E41.1.2"),sQuery(id+"F0.wireOp",EDGE,"E41.1.3"),sQuery(id+"F0.wireOp",EDGE,"E41.2.0"),sQuery(id+"F0.wireOp",EDGE,"E41.2.1"),sQuery(id+"F0.wireOp",EDGE,"E41.2.2"),sQuery(id+"F0.wireOp",EDGE,"E41.2.3"),sQuery(id+"F0.wireOp",EDGE,"E41.3.0"),sQuery(id+"F0.wireOp",EDGE,"E41.3.1"),sQuery(id+"F0.wireOp",EDGE,"E41.3.2"),sQuery(id+"F0.wireOp",EDGE,"E41.3.3"),sQuery(id+"F0.wireOp",EDGE,"E41.4.0"),sQuery(id+"F0.wireOp",EDGE,"E41.4.1"),sQuery(id+"F0.wireOp",EDGE,"E41.4.2"),sQuery(id+"F0.wireOp",EDGE,"E41.4.3"),sQuery(id+"F0.wireOp",EDGE,"E41.5.0"),sQuery(id+"F0.wireOp",EDGE,"E41.5.1"),sQuery(id+"F0.wireOp",EDGE,"E41.5.2"),sQuery(id+"F0.wireOp",EDGE,"E41.5.3"),sQuery(id+"F0.wireOp",EDGE,"E41.6.0"),sQuery(id+"F0.wireOp",EDGE,"E41.6.1"),sQuery(id+"F0.wireOp",EDGE,"E41.6.2"),sQuery(id+"F0.wireOp",EDGE,"E41.6.3"),sQuery(id+"F0.wireOp",EDGE,"E41.7.0"),sQuery(id+"F0.wireOp",EDGE,"E41.7.1"),sQuery(id+"F0.wireOp",EDGE,"E41.7.2"),sQuery(id+"F0.wireOp",EDGE,"E41.7.3"),sQuery(id+"F0.wireOp",EDGE,"E41.8.0"),sQuery(id+"F0.wireOp",EDGE,"E41.8.1"),sQuery(id+"F0.wireOp",EDGE,"E41.8.2"),sQuery(id+"F0.wireOp",EDGE,"E41.8.3"),sQuery(id+"F0.wireOp",EDGE,"E41.9.0"),sQuery(id+"F0.wireOp",EDGE,"E41.9.1"),sQuery(id+"F0.wireOp",EDGE,"E41.9.2"),sQuery(id+"F0.wireOp",EDGE,"E41.9.3"),sQuery(id+"F0.wireOp",EDGE,"E41.10.0"),sQuery(id+"F0.wireOp",EDGE,"E41.10.1"),sQuery(id+"F0.wireOp",EDGE,"E41.10.2"),sQuery(id+"F0.wireOp",EDGE,"E41.10.3"),sQuery(id+"F0.wireOp",EDGE,"E41.11.0"),sQuery(id+"F0.wireOp",EDGE,"E41.11.1"),sQuery(id+"F0.wireOp",EDGE,"E41.11.2"),sQuery(id+"F0.wireOp",EDGE,"E41.11.3")])],"isStart":false});
            var sketch = newSketch(context, id + "F2", { "sketchPlane" : qUnion([Q0])});
            skCircle(sketch, "E42", {"center": v(0, 0) * mm, "radius": 12.7 * mm});
            skSolve(sketch);
        }
        {
            var Q0;
            Q0=makeQuery(id+"F2.imprint","IMPRINT",FACE,{"disambiguationData":[TD([[makeQuery(id+"F2.imprint","IMPRINT",EDGE,{"derivedFrom":sQuery(id+"F2.wireOp",EDGE,"E42")}),1.0]])]});
            extrude(context, id + "F3", {"entities" : qUnion([Q0]), "operationType" : NewBodyOperationType.ADD, "depth" : 6.35 * mm});
        }
        {
            var Q0;
            Q0=makeQuery(id+"F3.opExtrude","CAP_FACE",FACE,{"disambiguationData":[OSD([sQuery(id+"F2.wireOp",EDGE,"E42")])],"isStart":false});
            var sketch = newSketch(context, id + "F4", { "sketchPlane" : qUnion([Q0])});
            skLineSegment(sketch, "E43", {"start": v(0, 0) * mm, "end": v(0, 9.53) * mm});
            skPoint(sketch, "E44", {"position": v(0, 9.53) * mm});
            skPoint(sketch, "E45", {"position": v(-28.4, 18.6) * mm});
            skPoint(sketch, "E46.1.0", {"position": v(-8.25, 4.76) * mm});
            skPoint(sketch, "E46.2.0", {"position": v(-8.25, -4.76) * mm});
            skPoint(sketch, "E46.3.0", {"position": v(0, -9.53) * mm});
            skPoint(sketch, "E46.4.0", {"position": v(8.25, -4.76) * mm});
            skPoint(sketch, "E46.5.0", {"position": v(8.25, 4.76) * mm});
            skPoint(sketch, "E46.center", {"position": v(0, 0) * mm});
            skSolve(sketch);
        }
        {
            var Q0;
            Q0=sQuery(id+"F4.wireOp",VERTEX,"E44");
            var Q1;
            Q1=sQuery(id+"F4.wireOp",VERTEX,"E46.1.0");
            var Q2;
            Q2=sQuery(id+"F4.wireOp",VERTEX,"E46.2.0");
            var Q3;
            Q3=sQuery(id+"F4.wireOp",VERTEX,"E46.3.0");
            var Q4;
            Q4=sQuery(id+"F4.wireOp",VERTEX,"E46.4.0");
            var Q5;
            Q5=sQuery(id+"F4.wireOp",VERTEX,"E46.5.0");
            var Q6;
            Q6=makeQuery(id+"F1.opExtrude","SWEPT_BODY",BODY,{"disambiguationData":[OSD([sQuery(id+"F0.wireOp",EDGE,"E0"),sQuery(id+"F0.wireOp",EDGE,"E1"),sQuery(id+"F0.wireOp",EDGE,"E2"),sQuery(id+"F0.wireOp",EDGE,"E3"),sQuery(id+"F0.wireOp",EDGE,"E4.MirrorCS"),sQuery(id+"F0.wireOp",EDGE,"E5.MirrorCS"),sQuery(id+"F0.wireOp",EDGE,"E6.MirrorCS"),sQuery(id+"F0.wireOp",EDGE,"E9.filletArc"),sQuery(id+"F0.wireOp",EDGE,"E10.filletArc"),sQuery(id+"F0.wireOp",EDGE,"E11"),sQuery(id+"F0.wireOp",EDGE,"E12"),sQuery(id+"F0.wireOp",EDGE,"E13.1.0"),sQuery(id+"F0.wireOp",EDGE,"E13.1.1"),sQuery(id+"F0.wireOp",EDGE,"E13.1.3"),sQuery(id+"F0.wireOp",EDGE,"E13.1.4"),sQuery(id+"F0.wireOp",EDGE,"E13.1.5"),sQuery(id+"F0.wireOp",EDGE,"E13.1.6"),sQuery(id+"F0.wireOp",EDGE,"E13.1.7"),sQuery(id+"F0.wireOp",EDGE,"E13.1.8"),sQuery(id+"F0.wireOp",EDGE,"E13.1.9"),sQuery(id+"F0.wireOp",EDGE,"E13.1.10"),sQuery(id+"F0.wireOp",EDGE,"E13.2.0"),sQuery(id+"F0.wireOp",EDGE,"E13.2.1"),sQuery(id+"F0.wireOp",EDGE,"E13.2.3"),sQuery(id+"F0.wireOp",EDGE,"E13.2.4"),sQuery(id+"F0.wireOp",EDGE,"E13.2.5"),sQuery(id+"F0.wireOp",EDGE,"E13.2.6"),sQuery(id+"F0.wireOp",EDGE,"E13.2.7"),sQuery(id+"F0.wireOp",EDGE,"E13.2.8"),sQuery(id+"F0.wireOp",EDGE,"E13.2.9"),sQuery(id+"F0.wireOp",EDGE,"E13.2.10"),sQuery(id+"F0.wireOp",EDGE,"E13.3.0"),sQuery(id+"F0.wireOp",EDGE,"E13.3.1"),sQuery(id+"F0.wireOp",EDGE,"E13.3.3"),sQuery(id+"F0.wireOp",EDGE,"E13.3.4"),sQuery(id+"F0.wireOp",EDGE,"E13.3.5"),sQuery(id+"F0.wireOp",EDGE,"E13.3.6"),sQuery(id+"F0.wireOp",EDGE,"E13.3.7"),sQuery(id+"F0.wireOp",EDGE,"E13.3.8"),sQuery(id+"F0.wireOp",EDGE,"E13.3.9"),sQuery(id+"F0.wireOp",EDGE,"E13.3.10"),sQuery(id+"F0.wireOp",EDGE,"E13.4.0"),sQuery(id+"F0.wireOp",EDGE,"E13.4.1"),sQuery(id+"F0.wireOp",EDGE,"E13.4.3"),sQuery(id+"F0.wireOp",EDGE,"E13.4.4"),sQuery(id+"F0.wireOp",EDGE,"E13.4.5"),sQuery(id+"F0.wireOp",EDGE,"E13.4.6"),sQuery(id+"F0.wireOp",EDGE,"E13.4.7"),sQuery(id+"F0.wireOp",EDGE,"E13.4.8"),sQuery(id+"F0.wireOp",EDGE,"E13.4.9"),sQuery(id+"F0.wireOp",EDGE,"E13.4.10"),sQuery(id+"F0.wireOp",EDGE,"E13.5.0"),sQuery(id+"F0.wireOp",EDGE,"E13.5.1"),sQuery(id+"F0.wireOp",EDGE,"E13.5.3"),sQuery(id+"F0.wireOp",EDGE,"E13.5.4"),sQuery(id+"F0.wireOp",EDGE,"E13.5.5"),sQuery(id+"F0.wireOp",EDGE,"E13.5.6"),sQuery(id+"F0.wireOp",EDGE,"E13.5.7"),sQuery(id+"F0.wireOp",EDGE,"E13.5.8"),sQuery(id+"F0.wireOp",EDGE,"E13.5.9"),sQuery(id+"F0.wireOp",EDGE,"E13.5.10"),sQuery(id+"F0.wireOp",EDGE,"E13.6.0"),sQuery(id+"F0.wireOp",EDGE,"E13.6.1"),sQuery(id+"F0.wireOp",EDGE,"E13.6.3"),sQuery(id+"F0.wireOp",EDGE,"E13.6.4"),sQuery(id+"F0.wireOp",EDGE,"E13.6.5"),sQuery(id+"F0.wireOp",EDGE,"E13.6.6"),sQuery(id+"F0.wireOp",EDGE,"E13.6.7"),sQuery(id+"F0.wireOp",EDGE,"E13.6.8"),sQuery(id+"F0.wireOp",EDGE,"E13.6.9"),sQuery(id+"F0.wireOp",EDGE,"E13.6.10"),sQuery(id+"F0.wireOp",EDGE,"E13.7.0"),sQuery(id+"F0.wireOp",EDGE,"E13.7.1"),sQuery(id+"F0.wireOp",EDGE,"E13.7.3"),sQuery(id+"F0.wireOp",EDGE,"E13.7.4"),sQuery(id+"F0.wireOp",EDGE,"E13.7.5"),sQuery(id+"F0.wireOp",EDGE,"E13.7.6"),sQuery(id+"F0.wireOp",EDGE,"E13.7.7"),sQuery(id+"F0.wireOp",EDGE,"E13.7.8"),sQuery(id+"F0.wireOp",EDGE,"E13.7.9"),sQuery(id+"F0.wireOp",EDGE,"E13.7.10"),sQuery(id+"F0.wireOp",EDGE,"E13.8.0"),sQuery(id+"F0.wireOp",EDGE,"E13.8.1"),sQuery(id+"F0.wireOp",EDGE,"E13.8.3"),sQuery(id+"F0.wireOp",EDGE,"E13.8.4"),sQuery(id+"F0.wireOp",EDGE,"E13.8.5"),sQuery(id+"F0.wireOp",EDGE,"E13.8.6"),sQuery(id+"F0.wireOp",EDGE,"E13.8.7"),sQuery(id+"F0.wireOp",EDGE,"E13.8.8"),sQuery(id+"F0.wireOp",EDGE,"E13.8.9"),sQuery(id+"F0.wireOp",EDGE,"E13.8.10"),sQuery(id+"F0.wireOp",EDGE,"E13.9.0"),sQuery(id+"F0.wireOp",EDGE,"E13.9.1"),sQuery(id+"F0.wireOp",EDGE,"E13.9.3"),sQuery(id+"F0.wireOp",EDGE,"E13.9.4"),sQuery(id+"F0.wireOp",EDGE,"E13.9.5"),sQuery(id+"F0.wireOp",EDGE,"E13.9.6"),sQuery(id+"F0.wireOp",EDGE,"E13.9.7"),sQuery(id+"F0.wireOp",EDGE,"E13.9.8"),sQuery(id+"F0.wireOp",EDGE,"E13.9.9"),sQuery(id+"F0.wireOp",EDGE,"E13.9.10"),sQuery(id+"F0.wireOp",EDGE,"E13.10.0"),sQuery(id+"F0.wireOp",EDGE,"E13.10.1"),sQuery(id+"F0.wireOp",EDGE,"E13.10.3"),sQuery(id+"F0.wireOp",EDGE,"E13.10.4"),sQuery(id+"F0.wireOp",EDGE,"E13.10.5"),sQuery(id+"F0.wireOp",EDGE,"E13.10.6"),sQuery(id+"F0.wireOp",EDGE,"E13.10.7"),sQuery(id+"F0.wireOp",EDGE,"E13.10.8"),sQuery(id+"F0.wireOp",EDGE,"E13.10.9"),sQuery(id+"F0.wireOp",EDGE,"E13.10.10"),sQuery(id+"F0.wireOp",EDGE,"E13.11.0"),sQuery(id+"F0.wireOp",EDGE,"E13.11.1"),sQuery(id+"F0.wireOp",EDGE,"E13.11.3"),sQuery(id+"F0.wireOp",EDGE,"E13.11.4"),sQuery(id+"F0.wireOp",EDGE,"E13.11.5"),sQuery(id+"F0.wireOp",EDGE,"E13.11.6"),sQuery(id+"F0.wireOp",EDGE,"E13.11.7"),sQuery(id+"F0.wireOp",EDGE,"E13.11.8"),sQuery(id+"F0.wireOp",EDGE,"E13.11.9"),sQuery(id+"F0.wireOp",EDGE,"E13.11.10"),sQuery(id+"F0.wireOp",EDGE,"E13.12.0"),sQuery(id+"F0.wireOp",EDGE,"E13.12.1"),sQuery(id+"F0.wireOp",EDGE,"E13.12.3"),sQuery(id+"F0.wireOp",EDGE,"E13.12.4"),sQuery(id+"F0.wireOp",EDGE,"E13.12.5"),sQuery(id+"F0.wireOp",EDGE,"E13.12.6"),sQuery(id+"F0.wireOp",EDGE,"E13.12.7"),sQuery(id+"F0.wireOp",EDGE,"E13.12.8"),sQuery(id+"F0.wireOp",EDGE,"E13.12.9"),sQuery(id+"F0.wireOp",EDGE,"E13.12.10"),sQuery(id+"F0.wireOp",EDGE,"E13.13.0"),sQuery(id+"F0.wireOp",EDGE,"E13.13.1"),sQuery(id+"F0.wireOp",EDGE,"E13.13.3"),sQuery(id+"F0.wireOp",EDGE,"E13.13.4"),sQuery(id+"F0.wireOp",EDGE,"E13.13.5"),sQuery(id+"F0.wireOp",EDGE,"E13.13.6"),sQuery(id+"F0.wireOp",EDGE,"E13.13.7"),sQuery(id+"F0.wireOp",EDGE,"E13.13.8"),sQuery(id+"F0.wireOp",EDGE,"E13.13.9"),sQuery(id+"F0.wireOp",EDGE,"E13.13.10"),sQuery(id+"F0.wireOp",EDGE,"E13.14.0"),sQuery(id+"F0.wireOp",EDGE,"E13.14.1"),sQuery(id+"F0.wireOp",EDGE,"E13.14.3"),sQuery(id+"F0.wireOp",EDGE,"E13.14.4"),sQuery(id+"F0.wireOp",EDGE,"E13.14.5"),sQuery(id+"F0.wireOp",EDGE,"E13.14.6"),sQuery(id+"F0.wireOp",EDGE,"E13.14.7"),sQuery(id+"F0.wireOp",EDGE,"E13.14.8"),sQuery(id+"F0.wireOp",EDGE,"E13.14.9"),sQuery(id+"F0.wireOp",EDGE,"E13.14.10"),sQuery(id+"F0.wireOp",EDGE,"E13.15.0"),sQuery(id+"F0.wireOp",EDGE,"E13.15.1"),sQuery(id+"F0.wireOp",EDGE,"E13.15.3"),sQuery(id+"F0.wireOp",EDGE,"E13.15.4"),sQuery(id+"F0.wireOp",EDGE,"E13.15.5"),sQuery(id+"F0.wireOp",EDGE,"E13.15.6"),sQuery(id+"F0.wireOp",EDGE,"E13.15.7"),sQuery(id+"F0.wireOp",EDGE,"E13.15.8"),sQuery(id+"F0.wireOp",EDGE,"E13.15.9"),sQuery(id+"F0.wireOp",EDGE,"E13.15.10"),sQuery(id+"F0.wireOp",EDGE,"E13.16.0"),sQuery(id+"F0.wireOp",EDGE,"E13.16.1"),sQuery(id+"F0.wireOp",EDGE,"E13.16.3"),sQuery(id+"F0.wireOp",EDGE,"E13.16.4"),sQuery(id+"F0.wireOp",EDGE,"E13.16.5"),sQuery(id+"F0.wireOp",EDGE,"E13.16.6"),sQuery(id+"F0.wireOp",EDGE,"E13.16.7"),sQuery(id+"F0.wireOp",EDGE,"E13.16.8"),sQuery(id+"F0.wireOp",EDGE,"E13.16.9"),sQuery(id+"F0.wireOp",EDGE,"E13.16.10"),sQuery(id+"F0.wireOp",EDGE,"E13.17.0"),sQuery(id+"F0.wireOp",EDGE,"E13.17.1"),sQuery(id+"F0.wireOp",EDGE,"E13.17.3"),sQuery(id+"F0.wireOp",EDGE,"E13.17.4"),sQuery(id+"F0.wireOp",EDGE,"E13.17.5"),sQuery(id+"F0.wireOp",EDGE,"E13.17.6"),sQuery(id+"F0.wireOp",EDGE,"E13.17.7"),sQuery(id+"F0.wireOp",EDGE,"E13.17.8"),sQuery(id+"F0.wireOp",EDGE,"E13.17.9"),sQuery(id+"F0.wireOp",EDGE,"E13.17.10"),sQuery(id+"F0.wireOp",EDGE,"E13.18.0"),sQuery(id+"F0.wireOp",EDGE,"E13.18.1"),sQuery(id+"F0.wireOp",EDGE,"E13.18.3"),sQuery(id+"F0.wireOp",EDGE,"E13.18.4"),sQuery(id+"F0.wireOp",EDGE,"E13.18.5"),sQuery(id+"F0.wireOp",EDGE,"E13.18.6"),sQuery(id+"F0.wireOp",EDGE,"E13.18.7"),sQuery(id+"F0.wireOp",EDGE,"E13.18.8"),sQuery(id+"F0.wireOp",EDGE,"E13.18.9"),sQuery(id+"F0.wireOp",EDGE,"E13.18.10"),sQuery(id+"F0.wireOp",EDGE,"E13.19.0"),sQuery(id+"F0.wireOp",EDGE,"E13.19.1"),sQuery(id+"F0.wireOp",EDGE,"E13.19.3"),sQuery(id+"F0.wireOp",EDGE,"E13.19.4"),sQuery(id+"F0.wireOp",EDGE,"E13.19.5"),sQuery(id+"F0.wireOp",EDGE,"E13.19.6"),sQuery(id+"F0.wireOp",EDGE,"E13.19.7"),sQuery(id+"F0.wireOp",EDGE,"E13.19.8"),sQuery(id+"F0.wireOp",EDGE,"E13.19.9"),sQuery(id+"F0.wireOp",EDGE,"E13.19.10"),sQuery(id+"F0.wireOp",EDGE,"E13.20.0"),sQuery(id+"F0.wireOp",EDGE,"E13.20.1"),sQuery(id+"F0.wireOp",EDGE,"E13.20.3"),sQuery(id+"F0.wireOp",EDGE,"E13.20.4"),sQuery(id+"F0.wireOp",EDGE,"E13.20.5"),sQuery(id+"F0.wireOp",EDGE,"E13.20.6"),sQuery(id+"F0.wireOp",EDGE,"E13.20.7"),sQuery(id+"F0.wireOp",EDGE,"E13.20.8"),sQuery(id+"F0.wireOp",EDGE,"E13.20.9"),sQuery(id+"F0.wireOp",EDGE,"E13.20.10"),sQuery(id+"F0.wireOp",EDGE,"E13.21.0"),sQuery(id+"F0.wireOp",EDGE,"E13.21.1"),sQuery(id+"F0.wireOp",EDGE,"E13.21.3"),sQuery(id+"F0.wireOp",EDGE,"E13.21.4"),sQuery(id+"F0.wireOp",EDGE,"E13.21.5"),sQuery(id+"F0.wireOp",EDGE,"E13.21.6"),sQuery(id+"F0.wireOp",EDGE,"E13.21.7"),sQuery(id+"F0.wireOp",EDGE,"E13.21.8"),sQuery(id+"F0.wireOp",EDGE,"E13.21.9"),sQuery(id+"F0.wireOp",EDGE,"E13.21.10"),sQuery(id+"F0.wireOp",EDGE,"E13.22.0"),sQuery(id+"F0.wireOp",EDGE,"E13.22.1"),sQuery(id+"F0.wireOp",EDGE,"E13.22.3"),sQuery(id+"F0.wireOp",EDGE,"E13.22.4"),sQuery(id+"F0.wireOp",EDGE,"E13.22.5"),sQuery(id+"F0.wireOp",EDGE,"E13.22.6"),sQuery(id+"F0.wireOp",EDGE,"E13.22.7"),sQuery(id+"F0.wireOp",EDGE,"E13.22.8"),sQuery(id+"F0.wireOp",EDGE,"E13.22.9"),sQuery(id+"F0.wireOp",EDGE,"E13.22.10"),sQuery(id+"F0.wireOp",EDGE,"E13.23.0"),sQuery(id+"F0.wireOp",EDGE,"E13.23.1"),sQuery(id+"F0.wireOp",EDGE,"E13.23.3"),sQuery(id+"F0.wireOp",EDGE,"E13.23.4"),sQuery(id+"F0.wireOp",EDGE,"E13.23.5"),sQuery(id+"F0.wireOp",EDGE,"E13.23.6"),sQuery(id+"F0.wireOp",EDGE,"E13.23.7"),sQuery(id+"F0.wireOp",EDGE,"E13.23.8"),sQuery(id+"F0.wireOp",EDGE,"E13.23.9"),sQuery(id+"F0.wireOp",EDGE,"E13.23.10"),sQuery(id+"F0.wireOp",EDGE,"E14.trimOffspring"),sQuery(id+"F0.wireOp",EDGE,"E15.trimOffspring"),sQuery(id+"F0.wireOp",EDGE,"E16.trimOffspring"),sQuery(id+"F0.wireOp",EDGE,"E17.trimOffspring"),sQuery(id+"F0.wireOp",EDGE,"E18.trimOffspring"),sQuery(id+"F0.wireOp",EDGE,"E19.trimOffspring"),sQuery(id+"F0.wireOp",EDGE,"E20.trimOffspring"),sQuery(id+"F0.wireOp",EDGE,"E21.trimOffspring"),sQuery(id+"F0.wireOp",EDGE,"E22.trimOffspring"),sQuery(id+"F0.wireOp",EDGE,"E23.trimOffspring"),sQuery(id+"F0.wireOp",EDGE,"E24.trimOffspring"),sQuery(id+"F0.wireOp",EDGE,"E25.trimOffspring"),sQuery(id+"F0.wireOp",EDGE,"E26.trimOffspring"),sQuery(id+"F0.wireOp",EDGE,"E27.trimOffspring"),sQuery(id+"F0.wireOp",EDGE,"E28.trimOffspring"),sQuery(id+"F0.wireOp",EDGE,"E29.trimOffspring"),sQuery(id+"F0.wireOp",EDGE,"E30.trimOffspring"),sQuery(id+"F0.wireOp",EDGE,"E31.trimOffspring"),sQuery(id+"F0.wireOp",EDGE,"E32.trimOffspring"),sQuery(id+"F0.wireOp",EDGE,"E33.trimOffspring"),sQuery(id+"F0.wireOp",EDGE,"E34.trimOffspring"),sQuery(id+"F0.wireOp",EDGE,"E35.trimOffspring"),sQuery(id+"F0.wireOp",EDGE,"E36.trimOffspring"),sQuery(id+"F0.wireOp",EDGE,"E37"),sQuery(id+"F0.wireOp",EDGE,"E38"),sQuery(id+"F0.wireOp",EDGE,"E39"),sQuery(id+"F0.wireOp",EDGE,"E40.MirrorCS"),sQuery(id+"F0.wireOp",EDGE,"E41.1.0"),sQuery(id+"F0.wireOp",EDGE,"E41.1.1"),sQuery(id+"F0.wireOp",EDGE,"E41.1.2"),sQuery(id+"F0.wireOp",EDGE,"E41.1.3"),sQuery(id+"F0.wireOp",EDGE,"E41.2.0"),sQuery(id+"F0.wireOp",EDGE,"E41.2.1"),sQuery(id+"F0.wireOp",EDGE,"E41.2.2"),sQuery(id+"F0.wireOp",EDGE,"E41.2.3"),sQuery(id+"F0.wireOp",EDGE,"E41.3.0"),sQuery(id+"F0.wireOp",EDGE,"E41.3.1"),sQuery(id+"F0.wireOp",EDGE,"E41.3.2"),sQuery(id+"F0.wireOp",EDGE,"E41.3.3"),sQuery(id+"F0.wireOp",EDGE,"E41.4.0"),sQuery(id+"F0.wireOp",EDGE,"E41.4.1"),sQuery(id+"F0.wireOp",EDGE,"E41.4.2"),sQuery(id+"F0.wireOp",EDGE,"E41.4.3"),sQuery(id+"F0.wireOp",EDGE,"E41.5.0"),sQuery(id+"F0.wireOp",EDGE,"E41.5.1"),sQuery(id+"F0.wireOp",EDGE,"E41.5.2"),sQuery(id+"F0.wireOp",EDGE,"E41.5.3"),sQuery(id+"F0.wireOp",EDGE,"E41.6.0"),sQuery(id+"F0.wireOp",EDGE,"E41.6.1"),sQuery(id+"F0.wireOp",EDGE,"E41.6.2"),sQuery(id+"F0.wireOp",EDGE,"E41.6.3"),sQuery(id+"F0.wireOp",EDGE,"E41.7.0"),sQuery(id+"F0.wireOp",EDGE,"E41.7.1"),sQuery(id+"F0.wireOp",EDGE,"E41.7.2"),sQuery(id+"F0.wireOp",EDGE,"E41.7.3"),sQuery(id+"F0.wireOp",EDGE,"E41.8.0"),sQuery(id+"F0.wireOp",EDGE,"E41.8.1"),sQuery(id+"F0.wireOp",EDGE,"E41.8.2"),sQuery(id+"F0.wireOp",EDGE,"E41.8.3"),sQuery(id+"F0.wireOp",EDGE,"E41.9.0"),sQuery(id+"F0.wireOp",EDGE,"E41.9.1"),sQuery(id+"F0.wireOp",EDGE,"E41.9.2"),sQuery(id+"F0.wireOp",EDGE,"E41.9.3"),sQuery(id+"F0.wireOp",EDGE,"E41.10.0"),sQuery(id+"F0.wireOp",EDGE,"E41.10.1"),sQuery(id+"F0.wireOp",EDGE,"E41.10.2"),sQuery(id+"F0.wireOp",EDGE,"E41.10.3"),sQuery(id+"F0.wireOp",EDGE,"E41.11.0"),sQuery(id+"F0.wireOp",EDGE,"E41.11.1"),sQuery(id+"F0.wireOp",EDGE,"E41.11.2"),sQuery(id+"F0.wireOp",EDGE,"E41.11.3")])]});
            hole(context, id + "F5", {"style" : HoleStyle.C_BORE, "endStyle" : HoleEndStyle.THROUGH, "holeDiameter" : 3.17 * mm, "cBoreDiameter" : 4.44 * mm, "cBoreDepth" : 3.17 * mm, "locations" : qUnion([Q0, Q1, Q2, Q3, Q4, Q5]), "scope" : qUnion([Q6]), "isTappedThrough" : true});
        }
        {
            var Q0;
            Q0=makeQuery(id+"F3.opExtrude","CAP_FACE",FACE,{"disambiguationData":[OSD([sQuery(id+"F2.wireOp",EDGE,"E42")])],"isStart":false});
            var sketch = newSketch(context, id + "F6", { "sketchPlane" : qUnion([Q0])});
            skPoint(sketch, "E47", {"position": v(0, 0) * mm});
            skSolve(sketch);
        }
        {
            var Q0;
            Q0=sQuery(id+"F6.wireOp",VERTEX,"E47");
            var Q1;
            Q1=makeQuery(id+"F1.opExtrude","SWEPT_BODY",BODY,{"disambiguationData":[OSD([sQuery(id+"F0.wireOp",EDGE,"E0"),sQuery(id+"F0.wireOp",EDGE,"E1"),sQuery(id+"F0.wireOp",EDGE,"E2"),sQuery(id+"F0.wireOp",EDGE,"E3"),sQuery(id+"F0.wireOp",EDGE,"E4.MirrorCS"),sQuery(id+"F0.wireOp",EDGE,"E5.MirrorCS"),sQuery(id+"F0.wireOp",EDGE,"E6.MirrorCS"),sQuery(id+"F0.wireOp",EDGE,"E9.filletArc"),sQuery(id+"F0.wireOp",EDGE,"E10.filletArc"),sQuery(id+"F0.wireOp",EDGE,"E11"),sQuery(id+"F0.wireOp",EDGE,"E12"),sQuery(id+"F0.wireOp",EDGE,"E13.1.0"),sQuery(id+"F0.wireOp",EDGE,"E13.1.1"),sQuery(id+"F0.wireOp",EDGE,"E13.1.3"),sQuery(id+"F0.wireOp",EDGE,"E13.1.4"),sQuery(id+"F0.wireOp",EDGE,"E13.1.5"),sQuery(id+"F0.wireOp",EDGE,"E13.1.6"),sQuery(id+"F0.wireOp",EDGE,"E13.1.7"),sQuery(id+"F0.wireOp",EDGE,"E13.1.8"),sQuery(id+"F0.wireOp",EDGE,"E13.1.9"),sQuery(id+"F0.wireOp",EDGE,"E13.1.10"),sQuery(id+"F0.wireOp",EDGE,"E13.2.0"),sQuery(id+"F0.wireOp",EDGE,"E13.2.1"),sQuery(id+"F0.wireOp",EDGE,"E13.2.3"),sQuery(id+"F0.wireOp",EDGE,"E13.2.4"),sQuery(id+"F0.wireOp",EDGE,"E13.2.5"),sQuery(id+"F0.wireOp",EDGE,"E13.2.6"),sQuery(id+"F0.wireOp",EDGE,"E13.2.7"),sQuery(id+"F0.wireOp",EDGE,"E13.2.8"),sQuery(id+"F0.wireOp",EDGE,"E13.2.9"),sQuery(id+"F0.wireOp",EDGE,"E13.2.10"),sQuery(id+"F0.wireOp",EDGE,"E13.3.0"),sQuery(id+"F0.wireOp",EDGE,"E13.3.1"),sQuery(id+"F0.wireOp",EDGE,"E13.3.3"),sQuery(id+"F0.wireOp",EDGE,"E13.3.4"),sQuery(id+"F0.wireOp",EDGE,"E13.3.5"),sQuery(id+"F0.wireOp",EDGE,"E13.3.6"),sQuery(id+"F0.wireOp",EDGE,"E13.3.7"),sQuery(id+"F0.wireOp",EDGE,"E13.3.8"),sQuery(id+"F0.wireOp",EDGE,"E13.3.9"),sQuery(id+"F0.wireOp",EDGE,"E13.3.10"),sQuery(id+"F0.wireOp",EDGE,"E13.4.0"),sQuery(id+"F0.wireOp",EDGE,"E13.4.1"),sQuery(id+"F0.wireOp",EDGE,"E13.4.3"),sQuery(id+"F0.wireOp",EDGE,"E13.4.4"),sQuery(id+"F0.wireOp",EDGE,"E13.4.5"),sQuery(id+"F0.wireOp",EDGE,"E13.4.6"),sQuery(id+"F0.wireOp",EDGE,"E13.4.7"),sQuery(id+"F0.wireOp",EDGE,"E13.4.8"),sQuery(id+"F0.wireOp",EDGE,"E13.4.9"),sQuery(id+"F0.wireOp",EDGE,"E13.4.10"),sQuery(id+"F0.wireOp",EDGE,"E13.5.0"),sQuery(id+"F0.wireOp",EDGE,"E13.5.1"),sQuery(id+"F0.wireOp",EDGE,"E13.5.3"),sQuery(id+"F0.wireOp",EDGE,"E13.5.4"),sQuery(id+"F0.wireOp",EDGE,"E13.5.5"),sQuery(id+"F0.wireOp",EDGE,"E13.5.6"),sQuery(id+"F0.wireOp",EDGE,"E13.5.7"),sQuery(id+"F0.wireOp",EDGE,"E13.5.8"),sQuery(id+"F0.wireOp",EDGE,"E13.5.9"),sQuery(id+"F0.wireOp",EDGE,"E13.5.10"),sQuery(id+"F0.wireOp",EDGE,"E13.6.0"),sQuery(id+"F0.wireOp",EDGE,"E13.6.1"),sQuery(id+"F0.wireOp",EDGE,"E13.6.3"),sQuery(id+"F0.wireOp",EDGE,"E13.6.4"),sQuery(id+"F0.wireOp",EDGE,"E13.6.5"),sQuery(id+"F0.wireOp",EDGE,"E13.6.6"),sQuery(id+"F0.wireOp",EDGE,"E13.6.7"),sQuery(id+"F0.wireOp",EDGE,"E13.6.8"),sQuery(id+"F0.wireOp",EDGE,"E13.6.9"),sQuery(id+"F0.wireOp",EDGE,"E13.6.10"),sQuery(id+"F0.wireOp",EDGE,"E13.7.0"),sQuery(id+"F0.wireOp",EDGE,"E13.7.1"),sQuery(id+"F0.wireOp",EDGE,"E13.7.3"),sQuery(id+"F0.wireOp",EDGE,"E13.7.4"),sQuery(id+"F0.wireOp",EDGE,"E13.7.5"),sQuery(id+"F0.wireOp",EDGE,"E13.7.6"),sQuery(id+"F0.wireOp",EDGE,"E13.7.7"),sQuery(id+"F0.wireOp",EDGE,"E13.7.8"),sQuery(id+"F0.wireOp",EDGE,"E13.7.9"),sQuery(id+"F0.wireOp",EDGE,"E13.7.10"),sQuery(id+"F0.wireOp",EDGE,"E13.8.0"),sQuery(id+"F0.wireOp",EDGE,"E13.8.1"),sQuery(id+"F0.wireOp",EDGE,"E13.8.3"),sQuery(id+"F0.wireOp",EDGE,"E13.8.4"),sQuery(id+"F0.wireOp",EDGE,"E13.8.5"),sQuery(id+"F0.wireOp",EDGE,"E13.8.6"),sQuery(id+"F0.wireOp",EDGE,"E13.8.7"),sQuery(id+"F0.wireOp",EDGE,"E13.8.8"),sQuery(id+"F0.wireOp",EDGE,"E13.8.9"),sQuery(id+"F0.wireOp",EDGE,"E13.8.10"),sQuery(id+"F0.wireOp",EDGE,"E13.9.0"),sQuery(id+"F0.wireOp",EDGE,"E13.9.1"),sQuery(id+"F0.wireOp",EDGE,"E13.9.3"),sQuery(id+"F0.wireOp",EDGE,"E13.9.4"),sQuery(id+"F0.wireOp",EDGE,"E13.9.5"),sQuery(id+"F0.wireOp",EDGE,"E13.9.6"),sQuery(id+"F0.wireOp",EDGE,"E13.9.7"),sQuery(id+"F0.wireOp",EDGE,"E13.9.8"),sQuery(id+"F0.wireOp",EDGE,"E13.9.9"),sQuery(id+"F0.wireOp",EDGE,"E13.9.10"),sQuery(id+"F0.wireOp",EDGE,"E13.10.0"),sQuery(id+"F0.wireOp",EDGE,"E13.10.1"),sQuery(id+"F0.wireOp",EDGE,"E13.10.3"),sQuery(id+"F0.wireOp",EDGE,"E13.10.4"),sQuery(id+"F0.wireOp",EDGE,"E13.10.5"),sQuery(id+"F0.wireOp",EDGE,"E13.10.6"),sQuery(id+"F0.wireOp",EDGE,"E13.10.7"),sQuery(id+"F0.wireOp",EDGE,"E13.10.8"),sQuery(id+"F0.wireOp",EDGE,"E13.10.9"),sQuery(id+"F0.wireOp",EDGE,"E13.10.10"),sQuery(id+"F0.wireOp",EDGE,"E13.11.0"),sQuery(id+"F0.wireOp",EDGE,"E13.11.1"),sQuery(id+"F0.wireOp",EDGE,"E13.11.3"),sQuery(id+"F0.wireOp",EDGE,"E13.11.4"),sQuery(id+"F0.wireOp",EDGE,"E13.11.5"),sQuery(id+"F0.wireOp",EDGE,"E13.11.6"),sQuery(id+"F0.wireOp",EDGE,"E13.11.7"),sQuery(id+"F0.wireOp",EDGE,"E13.11.8"),sQuery(id+"F0.wireOp",EDGE,"E13.11.9"),sQuery(id+"F0.wireOp",EDGE,"E13.11.10"),sQuery(id+"F0.wireOp",EDGE,"E13.12.0"),sQuery(id+"F0.wireOp",EDGE,"E13.12.1"),sQuery(id+"F0.wireOp",EDGE,"E13.12.3"),sQuery(id+"F0.wireOp",EDGE,"E13.12.4"),sQuery(id+"F0.wireOp",EDGE,"E13.12.5"),sQuery(id+"F0.wireOp",EDGE,"E13.12.6"),sQuery(id+"F0.wireOp",EDGE,"E13.12.7"),sQuery(id+"F0.wireOp",EDGE,"E13.12.8"),sQuery(id+"F0.wireOp",EDGE,"E13.12.9"),sQuery(id+"F0.wireOp",EDGE,"E13.12.10"),sQuery(id+"F0.wireOp",EDGE,"E13.13.0"),sQuery(id+"F0.wireOp",EDGE,"E13.13.1"),sQuery(id+"F0.wireOp",EDGE,"E13.13.3"),sQuery(id+"F0.wireOp",EDGE,"E13.13.4"),sQuery(id+"F0.wireOp",EDGE,"E13.13.5"),sQuery(id+"F0.wireOp",EDGE,"E13.13.6"),sQuery(id+"F0.wireOp",EDGE,"E13.13.7"),sQuery(id+"F0.wireOp",EDGE,"E13.13.8"),sQuery(id+"F0.wireOp",EDGE,"E13.13.9"),sQuery(id+"F0.wireOp",EDGE,"E13.13.10"),sQuery(id+"F0.wireOp",EDGE,"E13.14.0"),sQuery(id+"F0.wireOp",EDGE,"E13.14.1"),sQuery(id+"F0.wireOp",EDGE,"E13.14.3"),sQuery(id+"F0.wireOp",EDGE,"E13.14.4"),sQuery(id+"F0.wireOp",EDGE,"E13.14.5"),sQuery(id+"F0.wireOp",EDGE,"E13.14.6"),sQuery(id+"F0.wireOp",EDGE,"E13.14.7"),sQuery(id+"F0.wireOp",EDGE,"E13.14.8"),sQuery(id+"F0.wireOp",EDGE,"E13.14.9"),sQuery(id+"F0.wireOp",EDGE,"E13.14.10"),sQuery(id+"F0.wireOp",EDGE,"E13.15.0"),sQuery(id+"F0.wireOp",EDGE,"E13.15.1"),sQuery(id+"F0.wireOp",EDGE,"E13.15.3"),sQuery(id+"F0.wireOp",EDGE,"E13.15.4"),sQuery(id+"F0.wireOp",EDGE,"E13.15.5"),sQuery(id+"F0.wireOp",EDGE,"E13.15.6"),sQuery(id+"F0.wireOp",EDGE,"E13.15.7"),sQuery(id+"F0.wireOp",EDGE,"E13.15.8"),sQuery(id+"F0.wireOp",EDGE,"E13.15.9"),sQuery(id+"F0.wireOp",EDGE,"E13.15.10"),sQuery(id+"F0.wireOp",EDGE,"E13.16.0"),sQuery(id+"F0.wireOp",EDGE,"E13.16.1"),sQuery(id+"F0.wireOp",EDGE,"E13.16.3"),sQuery(id+"F0.wireOp",EDGE,"E13.16.4"),sQuery(id+"F0.wireOp",EDGE,"E13.16.5"),sQuery(id+"F0.wireOp",EDGE,"E13.16.6"),sQuery(id+"F0.wireOp",EDGE,"E13.16.7"),sQuery(id+"F0.wireOp",EDGE,"E13.16.8"),sQuery(id+"F0.wireOp",EDGE,"E13.16.9"),sQuery(id+"F0.wireOp",EDGE,"E13.16.10"),sQuery(id+"F0.wireOp",EDGE,"E13.17.0"),sQuery(id+"F0.wireOp",EDGE,"E13.17.1"),sQuery(id+"F0.wireOp",EDGE,"E13.17.3"),sQuery(id+"F0.wireOp",EDGE,"E13.17.4"),sQuery(id+"F0.wireOp",EDGE,"E13.17.5"),sQuery(id+"F0.wireOp",EDGE,"E13.17.6"),sQuery(id+"F0.wireOp",EDGE,"E13.17.7"),sQuery(id+"F0.wireOp",EDGE,"E13.17.8"),sQuery(id+"F0.wireOp",EDGE,"E13.17.9"),sQuery(id+"F0.wireOp",EDGE,"E13.17.10"),sQuery(id+"F0.wireOp",EDGE,"E13.18.0"),sQuery(id+"F0.wireOp",EDGE,"E13.18.1"),sQuery(id+"F0.wireOp",EDGE,"E13.18.3"),sQuery(id+"F0.wireOp",EDGE,"E13.18.4"),sQuery(id+"F0.wireOp",EDGE,"E13.18.5"),sQuery(id+"F0.wireOp",EDGE,"E13.18.6"),sQuery(id+"F0.wireOp",EDGE,"E13.18.7"),sQuery(id+"F0.wireOp",EDGE,"E13.18.8"),sQuery(id+"F0.wireOp",EDGE,"E13.18.9"),sQuery(id+"F0.wireOp",EDGE,"E13.18.10"),sQuery(id+"F0.wireOp",EDGE,"E13.19.0"),sQuery(id+"F0.wireOp",EDGE,"E13.19.1"),sQuery(id+"F0.wireOp",EDGE,"E13.19.3"),sQuery(id+"F0.wireOp",EDGE,"E13.19.4"),sQuery(id+"F0.wireOp",EDGE,"E13.19.5"),sQuery(id+"F0.wireOp",EDGE,"E13.19.6"),sQuery(id+"F0.wireOp",EDGE,"E13.19.7"),sQuery(id+"F0.wireOp",EDGE,"E13.19.8"),sQuery(id+"F0.wireOp",EDGE,"E13.19.9"),sQuery(id+"F0.wireOp",EDGE,"E13.19.10"),sQuery(id+"F0.wireOp",EDGE,"E13.20.0"),sQuery(id+"F0.wireOp",EDGE,"E13.20.1"),sQuery(id+"F0.wireOp",EDGE,"E13.20.3"),sQuery(id+"F0.wireOp",EDGE,"E13.20.4"),sQuery(id+"F0.wireOp",EDGE,"E13.20.5"),sQuery(id+"F0.wireOp",EDGE,"E13.20.6"),sQuery(id+"F0.wireOp",EDGE,"E13.20.7"),sQuery(id+"F0.wireOp",EDGE,"E13.20.8"),sQuery(id+"F0.wireOp",EDGE,"E13.20.9"),sQuery(id+"F0.wireOp",EDGE,"E13.20.10"),sQuery(id+"F0.wireOp",EDGE,"E13.21.0"),sQuery(id+"F0.wireOp",EDGE,"E13.21.1"),sQuery(id+"F0.wireOp",EDGE,"E13.21.3"),sQuery(id+"F0.wireOp",EDGE,"E13.21.4"),sQuery(id+"F0.wireOp",EDGE,"E13.21.5"),sQuery(id+"F0.wireOp",EDGE,"E13.21.6"),sQuery(id+"F0.wireOp",EDGE,"E13.21.7"),sQuery(id+"F0.wireOp",EDGE,"E13.21.8"),sQuery(id+"F0.wireOp",EDGE,"E13.21.9"),sQuery(id+"F0.wireOp",EDGE,"E13.21.10"),sQuery(id+"F0.wireOp",EDGE,"E13.22.0"),sQuery(id+"F0.wireOp",EDGE,"E13.22.1"),sQuery(id+"F0.wireOp",EDGE,"E13.22.3"),sQuery(id+"F0.wireOp",EDGE,"E13.22.4"),sQuery(id+"F0.wireOp",EDGE,"E13.22.5"),sQuery(id+"F0.wireOp",EDGE,"E13.22.6"),sQuery(id+"F0.wireOp",EDGE,"E13.22.7"),sQuery(id+"F0.wireOp",EDGE,"E13.22.8"),sQuery(id+"F0.wireOp",EDGE,"E13.22.9"),sQuery(id+"F0.wireOp",EDGE,"E13.22.10"),sQuery(id+"F0.wireOp",EDGE,"E13.23.0"),sQuery(id+"F0.wireOp",EDGE,"E13.23.1"),sQuery(id+"F0.wireOp",EDGE,"E13.23.3"),sQuery(id+"F0.wireOp",EDGE,"E13.23.4"),sQuery(id+"F0.wireOp",EDGE,"E13.23.5"),sQuery(id+"F0.wireOp",EDGE,"E13.23.6"),sQuery(id+"F0.wireOp",EDGE,"E13.23.7"),sQuery(id+"F0.wireOp",EDGE,"E13.23.8"),sQuery(id+"F0.wireOp",EDGE,"E13.23.9"),sQuery(id+"F0.wireOp",EDGE,"E13.23.10"),sQuery(id+"F0.wireOp",EDGE,"E14.trimOffspring"),sQuery(id+"F0.wireOp",EDGE,"E15.trimOffspring"),sQuery(id+"F0.wireOp",EDGE,"E16.trimOffspring"),sQuery(id+"F0.wireOp",EDGE,"E17.trimOffspring"),sQuery(id+"F0.wireOp",EDGE,"E18.trimOffspring"),sQuery(id+"F0.wireOp",EDGE,"E19.trimOffspring"),sQuery(id+"F0.wireOp",EDGE,"E20.trimOffspring"),sQuery(id+"F0.wireOp",EDGE,"E21.trimOffspring"),sQuery(id+"F0.wireOp",EDGE,"E22.trimOffspring"),sQuery(id+"F0.wireOp",EDGE,"E23.trimOffspring"),sQuery(id+"F0.wireOp",EDGE,"E24.trimOffspring"),sQuery(id+"F0.wireOp",EDGE,"E25.trimOffspring"),sQuery(id+"F0.wireOp",EDGE,"E26.trimOffspring"),sQuery(id+"F0.wireOp",EDGE,"E27.trimOffspring"),sQuery(id+"F0.wireOp",EDGE,"E28.trimOffspring"),sQuery(id+"F0.wireOp",EDGE,"E29.trimOffspring"),sQuery(id+"F0.wireOp",EDGE,"E30.trimOffspring"),sQuery(id+"F0.wireOp",EDGE,"E31.trimOffspring"),sQuery(id+"F0.wireOp",EDGE,"E32.trimOffspring"),sQuery(id+"F0.wireOp",EDGE,"E33.trimOffspring"),sQuery(id+"F0.wireOp",EDGE,"E34.trimOffspring"),sQuery(id+"F0.wireOp",EDGE,"E35.trimOffspring"),sQuery(id+"F0.wireOp",EDGE,"E36.trimOffspring"),sQuery(id+"F0.wireOp",EDGE,"E37"),sQuery(id+"F0.wireOp",EDGE,"E38"),sQuery(id+"F0.wireOp",EDGE,"E39"),sQuery(id+"F0.wireOp",EDGE,"E40.MirrorCS"),sQuery(id+"F0.wireOp",EDGE,"E41.1.0"),sQuery(id+"F0.wireOp",EDGE,"E41.1.1"),sQuery(id+"F0.wireOp",EDGE,"E41.1.2"),sQuery(id+"F0.wireOp",EDGE,"E41.1.3"),sQuery(id+"F0.wireOp",EDGE,"E41.2.0"),sQuery(id+"F0.wireOp",EDGE,"E41.2.1"),sQuery(id+"F0.wireOp",EDGE,"E41.2.2"),sQuery(id+"F0.wireOp",EDGE,"E41.2.3"),sQuery(id+"F0.wireOp",EDGE,"E41.3.0"),sQuery(id+"F0.wireOp",EDGE,"E41.3.1"),sQuery(id+"F0.wireOp",EDGE,"E41.3.2"),sQuery(id+"F0.wireOp",EDGE,"E41.3.3"),sQuery(id+"F0.wireOp",EDGE,"E41.4.0"),sQuery(id+"F0.wireOp",EDGE,"E41.4.1"),sQuery(id+"F0.wireOp",EDGE,"E41.4.2"),sQuery(id+"F0.wireOp",EDGE,"E41.4.3"),sQuery(id+"F0.wireOp",EDGE,"E41.5.0"),sQuery(id+"F0.wireOp",EDGE,"E41.5.1"),sQuery(id+"F0.wireOp",EDGE,"E41.5.2"),sQuery(id+"F0.wireOp",EDGE,"E41.5.3"),sQuery(id+"F0.wireOp",EDGE,"E41.6.0"),sQuery(id+"F0.wireOp",EDGE,"E41.6.1"),sQuery(id+"F0.wireOp",EDGE,"E41.6.2"),sQuery(id+"F0.wireOp",EDGE,"E41.6.3"),sQuery(id+"F0.wireOp",EDGE,"E41.7.0"),sQuery(id+"F0.wireOp",EDGE,"E41.7.1"),sQuery(id+"F0.wireOp",EDGE,"E41.7.2"),sQuery(id+"F0.wireOp",EDGE,"E41.7.3"),sQuery(id+"F0.wireOp",EDGE,"E41.8.0"),sQuery(id+"F0.wireOp",EDGE,"E41.8.1"),sQuery(id+"F0.wireOp",EDGE,"E41.8.2"),sQuery(id+"F0.wireOp",EDGE,"E41.8.3"),sQuery(id+"F0.wireOp",EDGE,"E41.9.0"),sQuery(id+"F0.wireOp",EDGE,"E41.9.1"),sQuery(id+"F0.wireOp",EDGE,"E41.9.2"),sQuery(id+"F0.wireOp",EDGE,"E41.9.3"),sQuery(id+"F0.wireOp",EDGE,"E41.10.0"),sQuery(id+"F0.wireOp",EDGE,"E41.10.1"),sQuery(id+"F0.wireOp",EDGE,"E41.10.2"),sQuery(id+"F0.wireOp",EDGE,"E41.10.3"),sQuery(id+"F0.wireOp",EDGE,"E41.11.0"),sQuery(id+"F0.wireOp",EDGE,"E41.11.1"),sQuery(id+"F0.wireOp",EDGE,"E41.11.2"),sQuery(id+"F0.wireOp",EDGE,"E41.11.3")])]});
            hole(context, id + "F7", {"style" : HoleStyle.C_BORE, "endStyle" : HoleEndStyle.THROUGH, "holeDiameter" : 6.35 * mm, "cBoreDiameter" : 12.7 * mm, "cBoreDepth" : 6.35 * mm, "locations" : qUnion([Q0]), "scope" : qUnion([Q1]), "isTappedThrough" : true});
        }
        {
            var Q0;
            Q0=makeQuery(id+"F1.opExtrude","CAP_EDGE",EDGE,{"disambiguationData":[OSD([sQuery(id+"F0.wireOp",EDGE,"E41.2.0")])],"isStart":false});
            var Q1;
            Q1=makeQuery(id+"F1.opExtrude","CAP_EDGE",EDGE,{"disambiguationData":[OSD([sQuery(id+"F0.wireOp",EDGE,"E41.2.3")])],"isStart":false});
            var Q2;
            Q2=makeQuery(id+"F1.opExtrude","CAP_EDGE",EDGE,{"disambiguationData":[OSD([sQuery(id+"F0.wireOp",EDGE,"E41.2.2")])],"isStart":false});
            var Q3;
            Q3=makeQuery(id+"F1.opExtrude","CAP_EDGE",EDGE,{"disambiguationData":[OSD([sQuery(id+"F0.wireOp",EDGE,"E41.2.1")])],"isStart":false});
            var Q4;
            Q4=makeQuery(id+"F1.opExtrude","CAP_EDGE",EDGE,{"disambiguationData":[OSD([sQuery(id+"F0.wireOp",EDGE,"E41.1.2")])],"isStart":false});
            var Q5;
            Q5=makeQuery(id+"F1.opExtrude","CAP_EDGE",EDGE,{"disambiguationData":[OSD([sQuery(id+"F0.wireOp",EDGE,"E41.11.0")])],"isStart":false});
            var Q6;
            Q6=makeQuery(id+"F1.opExtrude","CAP_EDGE",EDGE,{"disambiguationData":[OSD([sQuery(id+"F0.wireOp",EDGE,"E37")])],"isStart":false});
            var Q7;
            Q7=makeQuery(id+"F1.opExtrude","CAP_EDGE",EDGE,{"disambiguationData":[OSD([sQuery(id+"F0.wireOp",EDGE,"E41.1.0")])],"isStart":false});
            var Q8;
            Q8=makeQuery(id+"F1.opExtrude","CAP_EDGE",EDGE,{"disambiguationData":[OSD([sQuery(id+"F0.wireOp",EDGE,"E41.1.3")])],"isStart":false});
            var Q9;
            Q9=makeQuery(id+"F1.opExtrude","CAP_EDGE",EDGE,{"disambiguationData":[OSD([sQuery(id+"F0.wireOp",EDGE,"E41.1.1")])],"isStart":false});
            var Q10;
            Q10=makeQuery(id+"F1.opExtrude","CAP_EDGE",EDGE,{"disambiguationData":[OSD([sQuery(id+"F0.wireOp",EDGE,"E40.MirrorCS")])],"isStart":false});
            var Q11;
            Q11=makeQuery(id+"F1.opExtrude","CAP_EDGE",EDGE,{"disambiguationData":[OSD([sQuery(id+"F0.wireOp",EDGE,"E38")])],"isStart":false});
            var Q12;
            Q12=makeQuery(id+"F1.opExtrude","CAP_EDGE",EDGE,{"disambiguationData":[OSD([sQuery(id+"F0.wireOp",EDGE,"E41.11.1")])],"isStart":false});
            var Q13;
            Q13=makeQuery(id+"F1.opExtrude","CAP_EDGE",EDGE,{"disambiguationData":[OSD([sQuery(id+"F0.wireOp",EDGE,"E41.11.2")])],"isStart":false});
            var Q14;
            Q14=makeQuery(id+"F1.opExtrude","CAP_EDGE",EDGE,{"disambiguationData":[OSD([sQuery(id+"F0.wireOp",EDGE,"E41.10.2")])],"isStart":false});
            var Q15;
            Q15=makeQuery(id+"F1.opExtrude","CAP_EDGE",EDGE,{"disambiguationData":[OSD([sQuery(id+"F0.wireOp",EDGE,"E41.10.1")])],"isStart":false});
            var Q16;
            Q16=makeQuery(id+"F1.opExtrude","CAP_EDGE",EDGE,{"disambiguationData":[OSD([sQuery(id+"F0.wireOp",EDGE,"E41.10.0")])],"isStart":false});
            var Q17;
            Q17=makeQuery(id+"F1.opExtrude","CAP_EDGE",EDGE,{"disambiguationData":[OSD([sQuery(id+"F0.wireOp",EDGE,"E41.10.3")])],"isStart":false});
            var Q18;
            Q18=makeQuery(id+"F1.opExtrude","CAP_EDGE",EDGE,{"disambiguationData":[OSD([sQuery(id+"F0.wireOp",EDGE,"E41.11.3")])],"isStart":false});
            var Q19;
            Q19=makeQuery(id+"F1.opExtrude","CAP_EDGE",EDGE,{"disambiguationData":[OSD([sQuery(id+"F0.wireOp",EDGE,"E39")])],"isStart":false});
            var Q20;
            Q20=makeQuery(id+"F1.opExtrude","CAP_EDGE",EDGE,{"disambiguationData":[OSD([sQuery(id+"F0.wireOp",EDGE,"E41.9.0")])],"isStart":false});
            var Q21;
            Q21=makeQuery(id+"F1.opExtrude","CAP_EDGE",EDGE,{"disambiguationData":[OSD([sQuery(id+"F0.wireOp",EDGE,"E41.3.2")])],"isStart":false});
            var Q22;
            Q22=makeQuery(id+"F1.opExtrude","CAP_EDGE",EDGE,{"disambiguationData":[OSD([sQuery(id+"F0.wireOp",EDGE,"E41.3.1")])],"isStart":false});
            var Q23;
            Q23=makeQuery(id+"F1.opExtrude","CAP_EDGE",EDGE,{"disambiguationData":[OSD([sQuery(id+"F0.wireOp",EDGE,"E41.4.1")])],"isStart":false});
            var Q24;
            Q24=makeQuery(id+"F1.opExtrude","CAP_EDGE",EDGE,{"disambiguationData":[OSD([sQuery(id+"F0.wireOp",EDGE,"E41.4.2")])],"isStart":false});
            var Q25;
            Q25=makeQuery(id+"F1.opExtrude","CAP_EDGE",EDGE,{"disambiguationData":[OSD([sQuery(id+"F0.wireOp",EDGE,"E41.5.1")])],"isStart":false});
            var Q26;
            Q26=makeQuery(id+"F1.opExtrude","CAP_EDGE",EDGE,{"disambiguationData":[OSD([sQuery(id+"F0.wireOp",EDGE,"E41.5.2")])],"isStart":false});
            var Q27;
            Q27=makeQuery(id+"F1.opExtrude","CAP_EDGE",EDGE,{"disambiguationData":[OSD([sQuery(id+"F0.wireOp",EDGE,"E41.5.0")])],"isStart":false});
            var Q28;
            Q28=makeQuery(id+"F1.opExtrude","CAP_EDGE",EDGE,{"disambiguationData":[OSD([sQuery(id+"F0.wireOp",EDGE,"E41.5.3")])],"isStart":false});
            var Q29;
            Q29=makeQuery(id+"F1.opExtrude","CAP_EDGE",EDGE,{"disambiguationData":[OSD([sQuery(id+"F0.wireOp",EDGE,"E41.4.0")])],"isStart":false});
            var Q30;
            Q30=makeQuery(id+"F1.opExtrude","CAP_EDGE",EDGE,{"disambiguationData":[OSD([sQuery(id+"F0.wireOp",EDGE,"E41.3.0")])],"isStart":false});
            var Q31;
            Q31=makeQuery(id+"F1.opExtrude","CAP_EDGE",EDGE,{"disambiguationData":[OSD([sQuery(id+"F0.wireOp",EDGE,"E41.3.3")])],"isStart":false});
            var Q32;
            Q32=makeQuery(id+"F1.opExtrude","CAP_EDGE",EDGE,{"disambiguationData":[OSD([sQuery(id+"F0.wireOp",EDGE,"E41.4.3")])],"isStart":false});
            var Q33;
            Q33=makeQuery(id+"F1.opExtrude","CAP_EDGE",EDGE,{"disambiguationData":[OSD([sQuery(id+"F0.wireOp",EDGE,"E41.6.1")])],"isStart":false});
            var Q34;
            Q34=makeQuery(id+"F1.opExtrude","CAP_EDGE",EDGE,{"disambiguationData":[OSD([sQuery(id+"F0.wireOp",EDGE,"E41.6.2")])],"isStart":false});
            var Q35;
            Q35=makeQuery(id+"F1.opExtrude","CAP_EDGE",EDGE,{"disambiguationData":[OSD([sQuery(id+"F0.wireOp",EDGE,"E41.6.3")])],"isStart":false});
            var Q36;
            Q36=makeQuery(id+"F1.opExtrude","CAP_EDGE",EDGE,{"disambiguationData":[OSD([sQuery(id+"F0.wireOp",EDGE,"E41.6.0")])],"isStart":false});
            var Q37;
            Q37=makeQuery(id+"F1.opExtrude","CAP_EDGE",EDGE,{"disambiguationData":[OSD([sQuery(id+"F0.wireOp",EDGE,"E41.7.2")])],"isStart":false});
            var Q38;
            Q38=makeQuery(id+"F1.opExtrude","CAP_EDGE",EDGE,{"disambiguationData":[OSD([sQuery(id+"F0.wireOp",EDGE,"E41.7.0")])],"isStart":false});
            var Q39;
            Q39=makeQuery(id+"F1.opExtrude","CAP_EDGE",EDGE,{"disambiguationData":[OSD([sQuery(id+"F0.wireOp",EDGE,"E41.7.1")])],"isStart":false});
            var Q40;
            Q40=makeQuery(id+"F1.opExtrude","CAP_EDGE",EDGE,{"disambiguationData":[OSD([sQuery(id+"F0.wireOp",EDGE,"E41.8.1")])],"isStart":false});
            var Q41;
            Q41=makeQuery(id+"F1.opExtrude","CAP_EDGE",EDGE,{"disambiguationData":[OSD([sQuery(id+"F0.wireOp",EDGE,"E41.8.2")])],"isStart":false});
            var Q42;
            Q42=makeQuery(id+"F1.opExtrude","CAP_EDGE",EDGE,{"disambiguationData":[OSD([sQuery(id+"F0.wireOp",EDGE,"E41.8.0")])],"isStart":false});
            var Q43;
            Q43=makeQuery(id+"F1.opExtrude","CAP_EDGE",EDGE,{"disambiguationData":[OSD([sQuery(id+"F0.wireOp",EDGE,"E41.9.1")])],"isStart":false});
            var Q44;
            Q44=makeQuery(id+"F1.opExtrude","CAP_EDGE",EDGE,{"disambiguationData":[OSD([sQuery(id+"F0.wireOp",EDGE,"E41.7.3")])],"isStart":false});
            var Q45;
            Q45=makeQuery(id+"F1.opExtrude","CAP_EDGE",EDGE,{"disambiguationData":[OSD([sQuery(id+"F0.wireOp",EDGE,"E41.8.3")])],"isStart":false});
            var Q46;
            Q46=makeQuery(id+"F1.opExtrude","CAP_EDGE",EDGE,{"disambiguationData":[OSD([sQuery(id+"F0.wireOp",EDGE,"E41.9.3")])],"isStart":false});
            var Q47;
            Q47=makeQuery(id+"F1.opExtrude","CAP_EDGE",EDGE,{"disambiguationData":[OSD([sQuery(id+"F0.wireOp",EDGE,"E41.9.2")])],"isStart":false});
            chamfer(context, id + "F8", {"entities" : qUnion([Q0, Q1, Q2, Q3, Q4, Q5, Q6, Q7, Q8, Q9, Q10, Q11, Q12, Q13, Q14, Q15, Q16, Q17, Q18, Q19, Q20, Q21, Q22, Q23, Q24, Q25, Q26, Q27, Q28, Q29, Q30, Q31, Q32, Q33, Q34, Q35, Q36, Q37, Q38, Q39, Q40, Q41, Q42, Q43, Q44, Q45, Q46, Q47]), "width" : 0.38 * mm, "tangentPropagation" : true});
        }
        {
            var Q0;
            Q0=makeQuery(id+"F3.opExtrude","CAP_EDGE",EDGE,{"disambiguationData":[OSD([sQuery(id+"F2.wireOp",EDGE,"E42")])],"isStart":false});
            chamfer(context, id + "F9", {"entities" : qUnion([Q0]), "width" : 0.38 * mm, "tangentPropagation" : true});
        }
    });
